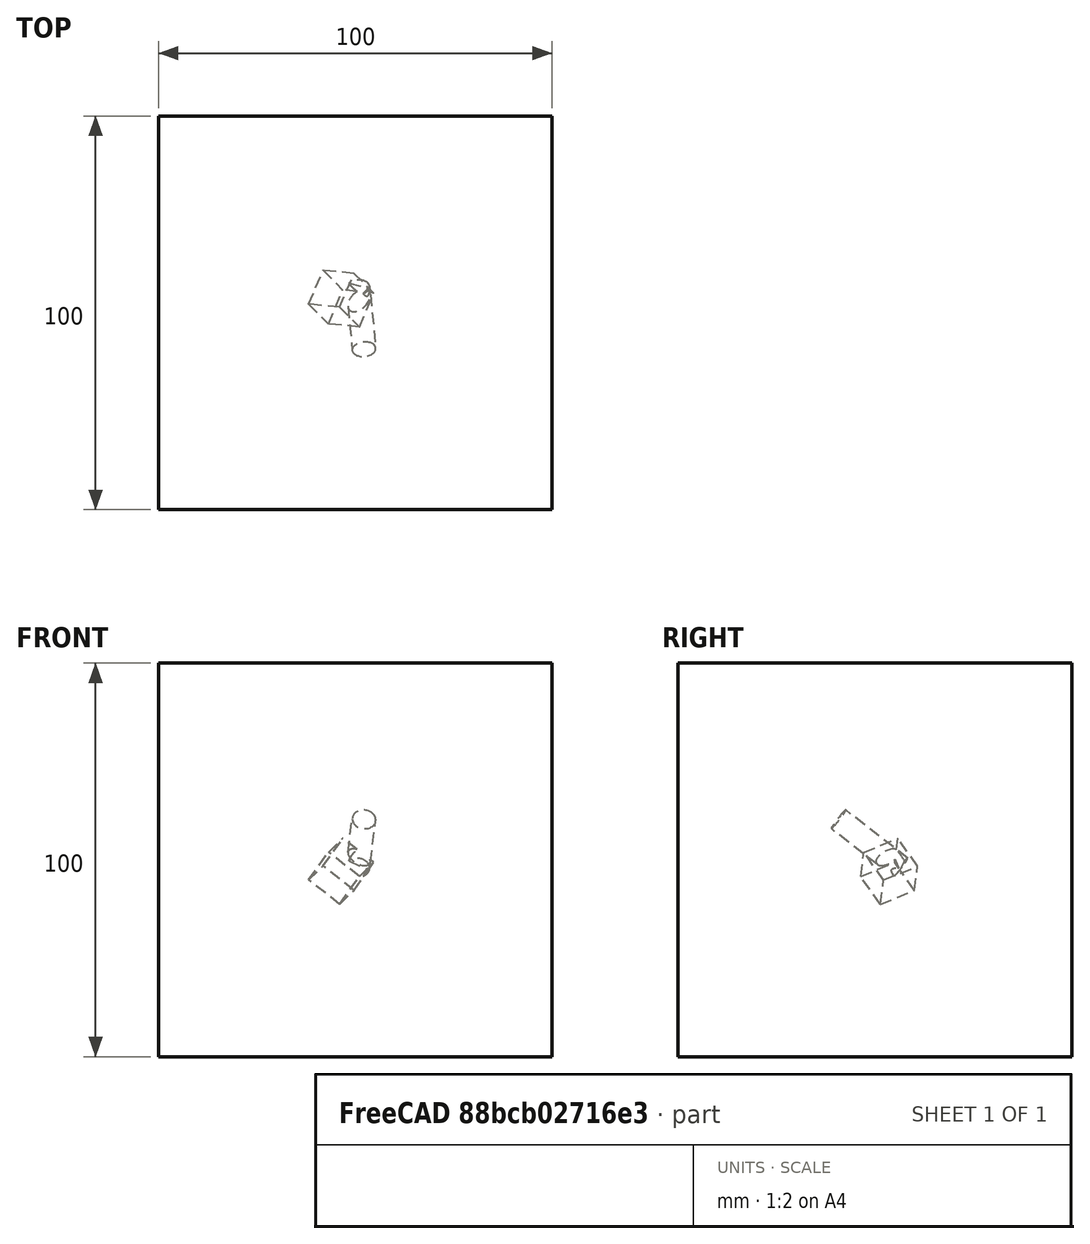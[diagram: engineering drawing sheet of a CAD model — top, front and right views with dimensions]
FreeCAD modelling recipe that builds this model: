
FCSTD DOCUMENT  (FreeCAD 0.21R33694 (Git))
Label: UnionTest
License: All rights reserved
objects: App::DocumentObjectGroupPython×1251, Part::FeaturePython×3, App::Part×2, Part::Fuse×1
note: 4 computed .brp shape members not serialized (recipe doc carries the construction recipe); baked Part::Feature solids carry a one-line shape summary decoded from their .brp

FEATURE [App::DocumentObjectGroupPython] HALFPI  # scripted group (container) (typed FeaturePython)
  name = HALFPI
  value = pi/2.
FEATURE [App::DocumentObjectGroupPython] PI  # scripted group (container) (typed FeaturePython)
  name = PI
  value = 1.*pi
FEATURE [App::DocumentObjectGroupPython] TWOPI  # scripted group (container) (typed FeaturePython)
  name = TWOPI
  value = 2.*pi
FEATURE [App::DocumentObjectGroupPython] Constants  # scripted group (container) (typed FeaturePython)
  Group = -> [HALFPI,PI,TWOPI]
FEATURE [App::DocumentObjectGroupPython] Variables  # scripted group (container) (typed FeaturePython)
FEATURE [App::DocumentObjectGroupPython] Quantities  # scripted group (container) (typed FeaturePython)
FEATURE [App::DocumentObjectGroupPython] Isotopes  # scripted group (container) (typed FeaturePython)
FEATURE [App::DocumentObjectGroupPython] Elements  # scripted group (container) (typed FeaturePython)
FEATURE [App::DocumentObjectGroupPython] Matrix  # scripted group (container) (typed FeaturePython)
FEATURE [App::DocumentObjectGroupPython] Surfaces  # scripted group (container) (typed FeaturePython)
FEATURE [App::DocumentObjectGroupPython] Opticals  # scripted group (container) (typed FeaturePython)
  Group = -> [Matrix,Surfaces]
FEATURE [App::DocumentObjectGroupPython] G4Isotopes  # scripted group (container) (typed FeaturePython)
FEATURE [App::DocumentObjectGroupPython] H_element  # scripted group (container) (typed FeaturePython)
  Z = 1
  atom_value = 1.008
  formula = H
  name = H_element
FEATURE [App::DocumentObjectGroupPython] He_element  # scripted group (container) (typed FeaturePython)
  Z = 2
  atom_value = 4.0026
  formula = He
  name = He_element
FEATURE [App::DocumentObjectGroupPython] Li_element  # scripted group (container) (typed FeaturePython)
  Z = 3
  atom_value = 6.94
  formula = Li
  name = Li_element
FEATURE [App::DocumentObjectGroupPython] Be_element  # scripted group (container) (typed FeaturePython)
  Z = 4
  atom_value = 9.01218
  formula = Be
  name = Be_element
FEATURE [App::DocumentObjectGroupPython] B_element  # scripted group (container) (typed FeaturePython)
  Z = 5
  atom_value = 10.81
  formula = B
  name = B_element
FEATURE [App::DocumentObjectGroupPython] C_element  # scripted group (container) (typed FeaturePython)
  Z = 6
  atom_value = 12.011
  formula = C
  name = C_element
FEATURE [App::DocumentObjectGroupPython] N_element  # scripted group (container) (typed FeaturePython)
  Z = 7
  atom_value = 14.007
  formula = N
  name = N_element
FEATURE [App::DocumentObjectGroupPython] O_element  # scripted group (container) (typed FeaturePython)
  Z = 8
  atom_value = 15.999
  formula = O
  name = O_element
FEATURE [App::DocumentObjectGroupPython] F_element  # scripted group (container) (typed FeaturePython)
  Z = 9
  atom_value = 18.9984
  formula = F
  name = F_element
FEATURE [App::DocumentObjectGroupPython] Ne_element  # scripted group (container) (typed FeaturePython)
  Z = 10
  atom_value = 20.1797
  formula = Ne
  name = Ne_element
FEATURE [App::DocumentObjectGroupPython] Na_element  # scripted group (container) (typed FeaturePython)
  Z = 11
  atom_value = 22.9898
  formula = Na
  name = Na_element
FEATURE [App::DocumentObjectGroupPython] Mg_element  # scripted group (container) (typed FeaturePython)
  Z = 12
  atom_value = 24.305
  formula = Mg
  name = Mg_element
FEATURE [App::DocumentObjectGroupPython] Al_element  # scripted group (container) (typed FeaturePython)
  Z = 13
  atom_value = 26.9815
  formula = Al
  name = Al_element
FEATURE [App::DocumentObjectGroupPython] Si_element  # scripted group (container) (typed FeaturePython)
  Z = 14
  atom_value = 28.085
  formula = Si
  name = Si_element
FEATURE [App::DocumentObjectGroupPython] P_element  # scripted group (container) (typed FeaturePython)
  Z = 15
  atom_value = 30.9738
  formula = P
  name = P_element
FEATURE [App::DocumentObjectGroupPython] S_element  # scripted group (container) (typed FeaturePython)
  Z = 16
  atom_value = 32.06
  formula = S
  name = S_element
FEATURE [App::DocumentObjectGroupPython] Cl_element  # scripted group (container) (typed FeaturePython)
  Z = 17
  atom_value = 35.45
  formula = Cl
  name = Cl_element
FEATURE [App::DocumentObjectGroupPython] Ar_element  # scripted group (container) (typed FeaturePython)
  Z = 18
  atom_value = 39.95
  formula = Ar
  name = Ar_element
FEATURE [App::DocumentObjectGroupPython] K_element  # scripted group (container) (typed FeaturePython)
  Z = 19
  atom_value = 39.0983
  formula = K
  name = K_element
FEATURE [App::DocumentObjectGroupPython] Ca_element  # scripted group (container) (typed FeaturePython)
  Z = 20
  atom_value = 40.078
  formula = Ca
  name = Ca_element
FEATURE [App::DocumentObjectGroupPython] Sc_element  # scripted group (container) (typed FeaturePython)
  Z = 21
  atom_value = 44.9559
  formula = Sc
  name = Sc_element
FEATURE [App::DocumentObjectGroupPython] Ti_element  # scripted group (container) (typed FeaturePython)
  Z = 22
  atom_value = 47.867
  formula = Ti
  name = Ti_element
FEATURE [App::DocumentObjectGroupPython] V_element  # scripted group (container) (typed FeaturePython)
  Z = 23
  atom_value = 50.9415
  formula = V
  name = V_element
FEATURE [App::DocumentObjectGroupPython] Cr_element  # scripted group (container) (typed FeaturePython)
  Z = 24
  atom_value = 51.9961
  formula = Cr
  name = Cr_element
FEATURE [App::DocumentObjectGroupPython] Mn_element  # scripted group (container) (typed FeaturePython)
  Z = 25
  atom_value = 54.938
  formula = Mn
  name = Mn_element
FEATURE [App::DocumentObjectGroupPython] Fe_element  # scripted group (container) (typed FeaturePython)
  Z = 26
  atom_value = 55.845
  formula = Fe
  name = Fe_element
FEATURE [App::DocumentObjectGroupPython] Co_element  # scripted group (container) (typed FeaturePython)
  Z = 27
  atom_value = 58.9332
  formula = Co
  name = Co_element
FEATURE [App::DocumentObjectGroupPython] Ni_element  # scripted group (container) (typed FeaturePython)
  Z = 28
  atom_value = 58.6934
  formula = Ni
  name = Ni_element
FEATURE [App::DocumentObjectGroupPython] Cu_element  # scripted group (container) (typed FeaturePython)
  Z = 29
  atom_value = 63.546
  formula = Cu
  name = Cu_element
FEATURE [App::DocumentObjectGroupPython] Zn_element  # scripted group (container) (typed FeaturePython)
  Z = 30
  atom_value = 65.38
  formula = Zn
  name = Zn_element
FEATURE [App::DocumentObjectGroupPython] Ga_element  # scripted group (container) (typed FeaturePython)
  Z = 31
  atom_value = 69.723
  formula = Ga
  name = Ga_element
FEATURE [App::DocumentObjectGroupPython] Ge_element  # scripted group (container) (typed FeaturePython)
  Z = 32
  atom_value = 72.63
  formula = Ge
  name = Ge_element
FEATURE [App::DocumentObjectGroupPython] As_element  # scripted group (container) (typed FeaturePython)
  Z = 33
  atom_value = 74.9216
  formula = As
  name = As_element
FEATURE [App::DocumentObjectGroupPython] Se_element  # scripted group (container) (typed FeaturePython)
  Z = 34
  atom_value = 78.971
  formula = Se
  name = Se_element
FEATURE [App::DocumentObjectGroupPython] Br_element  # scripted group (container) (typed FeaturePython)
  Z = 35
  atom_value = 79.904
  formula = Br
  name = Br_element
FEATURE [App::DocumentObjectGroupPython] Kr_element  # scripted group (container) (typed FeaturePython)
  Z = 36
  atom_value = 83.798
  formula = Kr
  name = Kr_element
FEATURE [App::DocumentObjectGroupPython] Rb_element  # scripted group (container) (typed FeaturePython)
  Z = 37
  atom_value = 85.4678
  formula = Rb
  name = Rb_element
FEATURE [App::DocumentObjectGroupPython] Sr_element  # scripted group (container) (typed FeaturePython)
  Z = 38
  atom_value = 87.62
  formula = Sr
  name = Sr_element
FEATURE [App::DocumentObjectGroupPython] Y_element  # scripted group (container) (typed FeaturePython)
  Z = 39
  atom_value = 88.9058
  formula = Y
  name = Y_element
FEATURE [App::DocumentObjectGroupPython] Zr_element  # scripted group (container) (typed FeaturePython)
  Z = 40
  atom_value = 91.224
  formula = Zr
  name = Zr_element
FEATURE [App::DocumentObjectGroupPython] Nb_element  # scripted group (container) (typed FeaturePython)
  Z = 41
  atom_value = 92.9064
  formula = Nb
  name = Nb_element
FEATURE [App::DocumentObjectGroupPython] Mo_element  # scripted group (container) (typed FeaturePython)
  Z = 42
  atom_value = 95.95
  formula = Mo
  name = Mo_element
FEATURE [App::DocumentObjectGroupPython] Tc_element  # scripted group (container) (typed FeaturePython)
  Z = 43
  atom_value = 97
  formula = Tc
  name = Tc_element
FEATURE [App::DocumentObjectGroupPython] Ru_element  # scripted group (container) (typed FeaturePython)
  Z = 44
  atom_value = 101.07
  formula = Ru
  name = Ru_element
FEATURE [App::DocumentObjectGroupPython] Rh_element  # scripted group (container) (typed FeaturePython)
  Z = 45
  atom_value = 102.905
  formula = Rh
  name = Rh_element
FEATURE [App::DocumentObjectGroupPython] Pd_element  # scripted group (container) (typed FeaturePython)
  Z = 46
  atom_value = 106.42
  formula = Pd
  name = Pd_element
FEATURE [App::DocumentObjectGroupPython] Ag_element  # scripted group (container) (typed FeaturePython)
  Z = 47
  atom_value = 107.868
  formula = Ag
  name = Ag_element
FEATURE [App::DocumentObjectGroupPython] Cd_element  # scripted group (container) (typed FeaturePython)
  Z = 48
  atom_value = 112.414
  formula = Cd
  name = Cd_element
FEATURE [App::DocumentObjectGroupPython] In_element  # scripted group (container) (typed FeaturePython)
  Z = 49
  atom_value = 114.818
  formula = In
  name = In_element
FEATURE [App::DocumentObjectGroupPython] Sn_element  # scripted group (container) (typed FeaturePython)
  Z = 50
  atom_value = 118.71
  formula = Sn
  name = Sn_element
FEATURE [App::DocumentObjectGroupPython] Sb_element  # scripted group (container) (typed FeaturePython)
  Z = 51
  atom_value = 121.76
  formula = Sb
  name = Sb_element
FEATURE [App::DocumentObjectGroupPython] Te_element  # scripted group (container) (typed FeaturePython)
  Z = 52
  atom_value = 127.6
  formula = Te
  name = Te_element
FEATURE [App::DocumentObjectGroupPython] I_element  # scripted group (container) (typed FeaturePython)
  Z = 53
  atom_value = 126.904
  formula = I
  name = I_element
FEATURE [App::DocumentObjectGroupPython] Xe_element  # scripted group (container) (typed FeaturePython)
  Z = 54
  atom_value = 131.293
  formula = Xe
  name = Xe_element
FEATURE [App::DocumentObjectGroupPython] Cs_element  # scripted group (container) (typed FeaturePython)
  Z = 55
  atom_value = 132.905
  formula = Cs
  name = Cs_element
FEATURE [App::DocumentObjectGroupPython] Ba_element  # scripted group (container) (typed FeaturePython)
  Z = 56
  atom_value = 137.327
  formula = Ba
  name = Ba_element
FEATURE [App::DocumentObjectGroupPython] La_element  # scripted group (container) (typed FeaturePython)
  Z = 57
  atom_value = 138.905
  formula = La
  name = La_element
FEATURE [App::DocumentObjectGroupPython] Ce_element  # scripted group (container) (typed FeaturePython)
  Z = 58
  atom_value = 140.116
  formula = Ce
  name = Ce_element
FEATURE [App::DocumentObjectGroupPython] Pr_element  # scripted group (container) (typed FeaturePython)
  Z = 59
  atom_value = 140.908
  formula = Pr
  name = Pr_element
FEATURE [App::DocumentObjectGroupPython] Nd_element  # scripted group (container) (typed FeaturePython)
  Z = 60
  atom_value = 144.242
  formula = Nd
  name = Nd_element
FEATURE [App::DocumentObjectGroupPython] Pm_element  # scripted group (container) (typed FeaturePython)
  Z = 61
  atom_value = 145
  formula = Pm
  name = Pm_element
FEATURE [App::DocumentObjectGroupPython] Sm_element  # scripted group (container) (typed FeaturePython)
  Z = 62
  atom_value = 150.36
  formula = Sm
  name = Sm_element
FEATURE [App::DocumentObjectGroupPython] Eu_element  # scripted group (container) (typed FeaturePython)
  Z = 63
  atom_value = 151.964
  formula = Eu
  name = Eu_element
FEATURE [App::DocumentObjectGroupPython] Gd_element  # scripted group (container) (typed FeaturePython)
  Z = 64
  atom_value = 157.25
  formula = Gd
  name = Gd_element
FEATURE [App::DocumentObjectGroupPython] Tb_element  # scripted group (container) (typed FeaturePython)
  Z = 65
  atom_value = 158.925
  formula = Tb
  name = Tb_element
FEATURE [App::DocumentObjectGroupPython] Dy_element  # scripted group (container) (typed FeaturePython)
  Z = 66
  atom_value = 162.5
  formula = Dy
  name = Dy_element
FEATURE [App::DocumentObjectGroupPython] Ho_element  # scripted group (container) (typed FeaturePython)
  Z = 67
  atom_value = 164.93
  formula = Ho
  name = Ho_element
FEATURE [App::DocumentObjectGroupPython] Er_element  # scripted group (container) (typed FeaturePython)
  Z = 68
  atom_value = 167.259
  formula = Er
  name = Er_element
FEATURE [App::DocumentObjectGroupPython] Tm_element  # scripted group (container) (typed FeaturePython)
  Z = 69
  atom_value = 168.934
  formula = Tm
  name = Tm_element
FEATURE [App::DocumentObjectGroupPython] Yb_element  # scripted group (container) (typed FeaturePython)
  Z = 70
  atom_value = 173.045
  formula = Yb
  name = Yb_element
FEATURE [App::DocumentObjectGroupPython] Lu_element  # scripted group (container) (typed FeaturePython)
  Z = 71
  atom_value = 174.967
  formula = Lu
  name = Lu_element
FEATURE [App::DocumentObjectGroupPython] Hf_element  # scripted group (container) (typed FeaturePython)
  Z = 72
  atom_value = 178.49
  formula = Hf
  name = Hf_element
FEATURE [App::DocumentObjectGroupPython] Ta_element  # scripted group (container) (typed FeaturePython)
  Z = 73
  atom_value = 180.948
  formula = Ta
  name = Ta_element
FEATURE [App::DocumentObjectGroupPython] W_element  # scripted group (container) (typed FeaturePython)
  Z = 74
  atom_value = 183.84
  formula = W
  name = W_element
FEATURE [App::DocumentObjectGroupPython] Re_element  # scripted group (container) (typed FeaturePython)
  Z = 75
  atom_value = 186.207
  formula = Re
  name = Re_element
FEATURE [App::DocumentObjectGroupPython] Os_element  # scripted group (container) (typed FeaturePython)
  Z = 76
  atom_value = 190.23
  formula = Os
  name = Os_element
FEATURE [App::DocumentObjectGroupPython] Ir_element  # scripted group (container) (typed FeaturePython)
  Z = 77
  atom_value = 192.217
  formula = Ir
  name = Ir_element
FEATURE [App::DocumentObjectGroupPython] Pt_element  # scripted group (container) (typed FeaturePython)
  Z = 78
  atom_value = 195.084
  formula = Pt
  name = Pt_element
FEATURE [App::DocumentObjectGroupPython] Au_element  # scripted group (container) (typed FeaturePython)
  Z = 79
  atom_value = 196.967
  formula = Au
  name = Au_element
FEATURE [App::DocumentObjectGroupPython] Hg_element  # scripted group (container) (typed FeaturePython)
  Z = 80
  atom_value = 200.592
  formula = Hg
  name = Hg_element
FEATURE [App::DocumentObjectGroupPython] Tl_element  # scripted group (container) (typed FeaturePython)
  Z = 81
  atom_value = 204.38
  formula = Tl
  name = Tl_element
FEATURE [App::DocumentObjectGroupPython] Pb_element  # scripted group (container) (typed FeaturePython)
  Z = 82
  atom_value = 207.2
  formula = Pb
  name = Pb_element
FEATURE [App::DocumentObjectGroupPython] Bi_element  # scripted group (container) (typed FeaturePython)
  Z = 83
  atom_value = 208.98
  formula = Bi
  name = Bi_element
FEATURE [App::DocumentObjectGroupPython] Po_element  # scripted group (container) (typed FeaturePython)
  Z = 84
  atom_value = 209
  formula = Po
  name = Po_element
FEATURE [App::DocumentObjectGroupPython] At_element  # scripted group (container) (typed FeaturePython)
  Z = 85
  atom_value = 210
  formula = At
  name = At_element
FEATURE [App::DocumentObjectGroupPython] Rn_element  # scripted group (container) (typed FeaturePython)
  Z = 86
  atom_value = 222
  formula = Rn
  name = Rn_element
FEATURE [App::DocumentObjectGroupPython] Fr_element  # scripted group (container) (typed FeaturePython)
  Z = 87
  atom_value = 223
  formula = Fr
  name = Fr_element
FEATURE [App::DocumentObjectGroupPython] Ra_element  # scripted group (container) (typed FeaturePython)
  Z = 88
  atom_value = 226
  formula = Ra
  name = Ra_element
FEATURE [App::DocumentObjectGroupPython] Ac_element  # scripted group (container) (typed FeaturePython)
  Z = 89
  atom_value = 227
  formula = Ac
  name = Ac_element
FEATURE [App::DocumentObjectGroupPython] Th_element  # scripted group (container) (typed FeaturePython)
  Z = 90
  atom_value = 232.038
  formula = Th
  name = Th_element
FEATURE [App::DocumentObjectGroupPython] Pa_element  # scripted group (container) (typed FeaturePython)
  Z = 91
  atom_value = 231.036
  formula = Pa
  name = Pa_element
FEATURE [App::DocumentObjectGroupPython] U_element  # scripted group (container) (typed FeaturePython)
  Z = 92
  atom_value = 238.029
  formula = U
  name = U_element
FEATURE [App::DocumentObjectGroupPython] Np_element  # scripted group (container) (typed FeaturePython)
  Z = 93
  atom_value = 237
  formula = Np
  name = Np_element
FEATURE [App::DocumentObjectGroupPython] Pu_element  # scripted group (container) (typed FeaturePython)
  Z = 94
  atom_value = 244
  formula = Pu
  name = Pu_element
FEATURE [App::DocumentObjectGroupPython] Am_element  # scripted group (container) (typed FeaturePython)
  Z = 95
  atom_value = 243
  formula = Am
  name = Am_element
FEATURE [App::DocumentObjectGroupPython] Cm_element  # scripted group (container) (typed FeaturePython)
  Z = 96
  atom_value = 247
  formula = Cm
  name = Cm_element
FEATURE [App::DocumentObjectGroupPython] Bk_element  # scripted group (container) (typed FeaturePython)
  Z = 97
  atom_value = 247
  formula = Bk
  name = Bk_element
FEATURE [App::DocumentObjectGroupPython] Cf_element  # scripted group (container) (typed FeaturePython)
  Z = 98
  atom_value = 251
  formula = Cf
  name = Cf_element
FEATURE [App::DocumentObjectGroupPython] G4Elements  # scripted group (container) (typed FeaturePython)
  Group = -> [H_element,He_element,Li_element,Be_element,B_element,C_element,N_element,O_element,F_element,Ne_element,Na_element,Mg_element,Al_element,Si_element,P_element,S_element,Cl_element,Ar_element,K_element,Ca_element,Sc_element,Ti_element,V_element,Cr_element,Mn_element,Fe_element,Co_element,Ni_element,Cu_element,Zn_element,Ga_element,Ge_element,As_element,Se_element,Br_element,Kr_element,Rb_element,+61 more]
FEATURE [App::DocumentObjectGroupPython] H_element001  label="H_element : 0.101"  # scripted group (container) (typed FeaturePython)
  n = 0.101327
FEATURE [App::DocumentObjectGroupPython] C_element001  label="C_element : 0.775"  # scripted group (container) (typed FeaturePython)
  n = 0.7755
FEATURE [App::DocumentObjectGroupPython] N_element001  label="N_element : 0.035"  # scripted group (container) (typed FeaturePython)
  n = 0.035057
FEATURE [App::DocumentObjectGroupPython] O_element001  label="O_element : 0.052"  # scripted group (container) (typed FeaturePython)
  n = 0.0523159
FEATURE [App::DocumentObjectGroupPython] F_element001  label="F_element : 0.017"  # scripted group (container) (typed FeaturePython)
  n = 0.017422
FEATURE [App::DocumentObjectGroupPython] Ca_element001  label="Ca_element : 0.018"  # scripted group (container) (typed FeaturePython)
  n = 0.018378
FEATURE [App::DocumentObjectGroupPython] G4_A_150_TISSUE  label="G4_A-150_TISSUE"  # scripted group (container) (typed FeaturePython)
  Dunit = g/cm3
  Dvalue = 1.127
  Group = -> [H_element001,C_element001,N_element001,O_element001,F_element001,Ca_element001]
  conduct = 2
  density = 1
  expand = 3
  formula = G4_A-150_TISSUE
  name = G4_A-150_TISSUE
  specific = 4
FEATURE [App::DocumentObjectGroupPython] C_element002  label="C_element : 3"  # scripted group (container) (typed FeaturePython)
  n = 3
  ref = C_element
FEATURE [App::DocumentObjectGroupPython] H_element002  label="H_element : 6"  # scripted group (container) (typed FeaturePython)
  n = 6
  ref = H_element
FEATURE [App::DocumentObjectGroupPython] O_element002  label="O_element : 1"  # scripted group (container) (typed FeaturePython)
  n = 1
  ref = O_element
FEATURE [App::DocumentObjectGroupPython] G4_ACETONE  # scripted group (container) (typed FeaturePython)
  Dunit = g/cm3
  Dvalue = 0.7899
  Group = -> [C_element002,H_element002,O_element002]
  conduct = 2
  density = 1
  expand = 3
  formula = G4_ACETONE
  name = G4_ACETONE
  specific = 4
FEATURE [App::DocumentObjectGroupPython] C_element003  label="C_element : 2"  # scripted group (container) (typed FeaturePython)
  n = 2
  ref = C_element
FEATURE [App::DocumentObjectGroupPython] H_element003  label="H_element : 2"  # scripted group (container) (typed FeaturePython)
  n = 2
  ref = H_element
FEATURE [App::DocumentObjectGroupPython] G4_ACETYLENE  # scripted group (container) (typed FeaturePython)
  Dunit = g/cm3
  Dvalue = 0.0010967
  Group = -> [C_element003,H_element003]
  conduct = 2
  density = 1
  expand = 3
  formula = G4_ACETYLENE
  name = G4_ACETYLENE
  specific = 4
FEATURE [App::DocumentObjectGroupPython] C_element004  label="C_element : 5"  # scripted group (container) (typed FeaturePython)
  n = 5
  ref = C_element
FEATURE [App::DocumentObjectGroupPython] H_element004  label="H_element : 5"  # scripted group (container) (typed FeaturePython)
  n = 5
  ref = H_element
FEATURE [App::DocumentObjectGroupPython] N_element002  label="N_element : 5"  # scripted group (container) (typed FeaturePython)
  n = 5
  ref = N_element
FEATURE [App::DocumentObjectGroupPython] G4_ADENINE  # scripted group (container) (typed FeaturePython)
  Dunit = g/cm3
  Dvalue = 1.6
  Group = -> [C_element004,H_element004,N_element002]
  conduct = 2
  density = 1
  expand = 3
  formula = G4_ADENINE
  name = G4_ADENINE
  specific = 4
FEATURE [App::DocumentObjectGroupPython] H_element005  label="H_element : 0.114"  # scripted group (container) (typed FeaturePython)
  n = 0.114
FEATURE [App::DocumentObjectGroupPython] C_element005  label="C_element : 0.598"  # scripted group (container) (typed FeaturePython)
  n = 0.598
FEATURE [App::DocumentObjectGroupPython] N_element003  label="N_element : 0.007"  # scripted group (container) (typed FeaturePython)
  n = 0.007
FEATURE [App::DocumentObjectGroupPython] O_element003  label="O_element : 0.278"  # scripted group (container) (typed FeaturePython)
  n = 0.278
FEATURE [App::DocumentObjectGroupPython] Na_element001  label="Na_element : 0.001"  # scripted group (container) (typed FeaturePython)
  n = 0.001
FEATURE [App::DocumentObjectGroupPython] S_element001  label="S_element : 0.001"  # scripted group (container) (typed FeaturePython)
  n = 0.001
FEATURE [App::DocumentObjectGroupPython] Cl_element001  label="Cl_element : 0.001"  # scripted group (container) (typed FeaturePython)
  n = 0.001
FEATURE [App::DocumentObjectGroupPython] G4_ADIPOSE_TISSUE_ICRP  # scripted group (container) (typed FeaturePython)
  Dunit = g/cm3
  Dvalue = 0.95
  Group = -> [H_element005,C_element005,N_element003,O_element003,Na_element001,S_element001,Cl_element001]
  conduct = 2
  density = 1
  expand = 3
  formula = G4_ADIPOSE_TISSUE_ICRP
  name = G4_ADIPOSE_TISSUE_ICRP
  specific = 4
FEATURE [App::DocumentObjectGroupPython] C_element006  label="C_element : 0.000"  # scripted group (container) (typed FeaturePython)
  n = 0.000124
FEATURE [App::DocumentObjectGroupPython] N_element004  label="N_element : 0.755"  # scripted group (container) (typed FeaturePython)
  n = 0.755268
FEATURE [App::DocumentObjectGroupPython] O_element004  label="O_element : 0.232"  # scripted group (container) (typed FeaturePython)
  n = 0.231781
FEATURE [App::DocumentObjectGroupPython] Ar_element001  label="Ar_element : 0.013"  # scripted group (container) (typed FeaturePython)
  n = 0.012827
FEATURE [App::DocumentObjectGroupPython] G4_AIR  # scripted group (container) (typed FeaturePython)
  Dunit = g/cm3
  Dvalue = 0.00120479
  Group = -> [C_element006,N_element004,O_element004,Ar_element001]
  conduct = 2
  density = 1
  expand = 3
  formula = G4_AIR
  name = G4_AIR
  specific = 4
FEATURE [App::DocumentObjectGroupPython] C_element007  label="C_element : 006"  # scripted group (container) (typed FeaturePython)
  n = 3
  ref = C_element
FEATURE [App::DocumentObjectGroupPython] H_element006  label="H_element : 7"  # scripted group (container) (typed FeaturePython)
  n = 7
  ref = H_element
FEATURE [App::DocumentObjectGroupPython] N_element005  label="N_element : 1"  # scripted group (container) (typed FeaturePython)
  n = 1
  ref = N_element
FEATURE [App::DocumentObjectGroupPython] O_element005  label="O_element : 2"  # scripted group (container) (typed FeaturePython)
  n = 2
  ref = O_element
FEATURE [App::DocumentObjectGroupPython] G4_ALANINE  # scripted group (container) (typed FeaturePython)
  Dunit = g/cm3
  Dvalue = 1.42
  Group = -> [C_element007,H_element006,N_element005,O_element005]
  conduct = 2
  density = 1
  expand = 3
  formula = G4_ALANINE
  name = G4_ALANINE
  specific = 4
FEATURE [App::DocumentObjectGroupPython] Al_element001  label="Al_element : 2"  # scripted group (container) (typed FeaturePython)
  n = 2
  ref = Al_element
FEATURE [App::DocumentObjectGroupPython] O_element006  label="O_element : 3"  # scripted group (container) (typed FeaturePython)
  n = 3
  ref = O_element
FEATURE [App::DocumentObjectGroupPython] G4_ALUMINUM_OXIDE  # scripted group (container) (typed FeaturePython)
  Dunit = g/cm3
  Dvalue = 3.97
  Group = -> [Al_element001,O_element006]
  conduct = 2
  density = 1
  expand = 3
  formula = G4_ALUMINUM_OXIDE
  name = G4_ALUMINUM_OXIDE
  specific = 4
FEATURE [App::DocumentObjectGroupPython] H_element007  label="H_element : 0.106"  # scripted group (container) (typed FeaturePython)
  n = 0.10593
FEATURE [App::DocumentObjectGroupPython] C_element008  label="C_element : 0.789"  # scripted group (container) (typed FeaturePython)
  n = 0.788974
FEATURE [App::DocumentObjectGroupPython] O_element007  label="O_element : 0.105"  # scripted group (container) (typed FeaturePython)
  n = 0.105096
FEATURE [App::DocumentObjectGroupPython] G4_AMBER  # scripted group (container) (typed FeaturePython)
  Dunit = g/cm3
  Dvalue = 1.1
  Group = -> [H_element007,C_element008,O_element007]
  conduct = 2
  density = 1
  expand = 3
  formula = G4_AMBER
  name = G4_AMBER
  specific = 4
FEATURE [App::DocumentObjectGroupPython] N_element006  label="N_element : 006"  # scripted group (container) (typed FeaturePython)
  n = 1
  ref = N_element
FEATURE [App::DocumentObjectGroupPython] H_element008  label="H_element : 3"  # scripted group (container) (typed FeaturePython)
  n = 3
  ref = H_element
FEATURE [App::DocumentObjectGroupPython] G4_AMMONIA  # scripted group (container) (typed FeaturePython)
  Dunit = g/cm3
  Dvalue = 0.000826019
  Group = -> [N_element006,H_element008]
  conduct = 2
  density = 1
  expand = 3
  formula = G4_AMMONIA
  name = G4_AMMONIA
  specific = 4
FEATURE [App::DocumentObjectGroupPython] C_element009  label="C_element : 6"  # scripted group (container) (typed FeaturePython)
  n = 6
  ref = C_element
FEATURE [App::DocumentObjectGroupPython] H_element009  label="H_element : 008"  # scripted group (container) (typed FeaturePython)
  n = 7
  ref = H_element
FEATURE [App::DocumentObjectGroupPython] N_element007  label="N_element : 007"  # scripted group (container) (typed FeaturePython)
  n = 1
  ref = N_element
FEATURE [App::DocumentObjectGroupPython] G4_ANILINE  # scripted group (container) (typed FeaturePython)
  Dunit = g/cm3
  Dvalue = 1.0235
  Group = -> [C_element009,H_element009,N_element007]
  conduct = 2
  density = 1
  expand = 3
  formula = G4_ANILINE
  name = G4_ANILINE
  specific = 4
FEATURE [App::DocumentObjectGroupPython] C_element010  label="C_element : 14"  # scripted group (container) (typed FeaturePython)
  n = 14
  ref = C_element
FEATURE [App::DocumentObjectGroupPython] H_element010  label="H_element : 10"  # scripted group (container) (typed FeaturePython)
  n = 10
  ref = H_element
FEATURE [App::DocumentObjectGroupPython] G4_ANTHRACENE  # scripted group (container) (typed FeaturePython)
  Dunit = g/cm3
  Dvalue = 1.283
  Group = -> [C_element010,H_element010]
  conduct = 2
  density = 1
  expand = 3
  formula = G4_ANTHRACENE
  name = G4_ANTHRACENE
  specific = 4
FEATURE [App::DocumentObjectGroupPython] H_element011  label="H_element : 0.065"  # scripted group (container) (typed FeaturePython)
  n = 0.0654709
FEATURE [App::DocumentObjectGroupPython] C_element011  label="C_element : 0.537"  # scripted group (container) (typed FeaturePython)
  n = 0.536944
FEATURE [App::DocumentObjectGroupPython] N_element008  label="N_element : 0.021"  # scripted group (container) (typed FeaturePython)
  n = 0.0215
FEATURE [App::DocumentObjectGroupPython] O_element008  label="O_element : 0.032"  # scripted group (container) (typed FeaturePython)
  n = 0.032085
FEATURE [App::DocumentObjectGroupPython] F_element002  label="F_element : 0.167"  # scripted group (container) (typed FeaturePython)
  n = 0.167411
FEATURE [App::DocumentObjectGroupPython] Ca_element002  label="Ca_element : 0.177"  # scripted group (container) (typed FeaturePython)
  n = 0.176589
FEATURE [App::DocumentObjectGroupPython] G4_B_100_BONE  label="G4_B-100_BONE"  # scripted group (container) (typed FeaturePython)
  Dunit = g/cm3
  Dvalue = 1.45
  Group = -> [H_element011,C_element011,N_element008,O_element008,F_element002,Ca_element002]
  conduct = 2
  density = 1
  expand = 3
  formula = G4_B-100_BONE
  name = G4_B-100_BONE
  specific = 4
FEATURE [App::DocumentObjectGroupPython] H_element012  label="H_element : 0.057"  # scripted group (container) (typed FeaturePython)
  n = 0.057441
FEATURE [App::DocumentObjectGroupPython] C_element012  label="C_element : 0.790"  # scripted group (container) (typed FeaturePython)
  n = 0.774591
FEATURE [App::DocumentObjectGroupPython] O_element009  label="O_element : 0.168"  # scripted group (container) (typed FeaturePython)
  n = 0.167968
FEATURE [App::DocumentObjectGroupPython] G4_BAKELITE  # scripted group (container) (typed FeaturePython)
  Dunit = g/cm3
  Dvalue = 1.25
  Group = -> [H_element012,C_element012,O_element009]
  conduct = 2
  density = 1
  expand = 3
  formula = G4_BAKELITE
  name = G4_BAKELITE
  specific = 4
FEATURE [App::DocumentObjectGroupPython] Ba_element001  label="Ba_element : 1"  # scripted group (container) (typed FeaturePython)
  n = 1
  ref = Ba_element
FEATURE [App::DocumentObjectGroupPython] F_element003  label="F_element : 2"  # scripted group (container) (typed FeaturePython)
  n = 2
  ref = F_element
FEATURE [App::DocumentObjectGroupPython] G4_BARIUM_FLUORIDE  # scripted group (container) (typed FeaturePython)
  Dunit = g/cm3
  Dvalue = 4.89
  Group = -> [Ba_element001,F_element003]
  conduct = 2
  density = 1
  expand = 3
  formula = G4_BARIUM_FLUORIDE
  name = G4_BARIUM_FLUORIDE
  specific = 4
FEATURE [App::DocumentObjectGroupPython] Ba_element002  label="Ba_element : 002"  # scripted group (container) (typed FeaturePython)
  n = 1
  ref = Ba_element
FEATURE [App::DocumentObjectGroupPython] S_element002  label="S_element : 1"  # scripted group (container) (typed FeaturePython)
  n = 1
  ref = S_element
FEATURE [App::DocumentObjectGroupPython] O_element010  label="O_element : 4"  # scripted group (container) (typed FeaturePython)
  n = 4
  ref = O_element
FEATURE [App::DocumentObjectGroupPython] G4_BARIUM_SULFATE  # scripted group (container) (typed FeaturePython)
  Dunit = g/cm3
  Dvalue = 4.5
  Group = -> [Ba_element002,S_element002,O_element010]
  conduct = 2
  density = 1
  expand = 3
  formula = G4_BARIUM_SULFATE
  name = G4_BARIUM_SULFATE
  specific = 4
FEATURE [App::DocumentObjectGroupPython] C_element013  label="C_element : 007"  # scripted group (container) (typed FeaturePython)
  n = 6
  ref = C_element
FEATURE [App::DocumentObjectGroupPython] H_element013  label="H_element : 009"  # scripted group (container) (typed FeaturePython)
  n = 6
  ref = H_element
FEATURE [App::DocumentObjectGroupPython] G4_BENZENE  # scripted group (container) (typed FeaturePython)
  Dunit = g/cm3
  Dvalue = 0.87865
  Group = -> [C_element013,H_element013]
  conduct = 2
  density = 1
  expand = 3
  formula = G4_BENZENE
  name = G4_BENZENE
  specific = 4
FEATURE [App::DocumentObjectGroupPython] Be_element001  label="Be_element : 1"  # scripted group (container) (typed FeaturePython)
  n = 1
  ref = Be_element
FEATURE [App::DocumentObjectGroupPython] O_element011  label="O_element : 005"  # scripted group (container) (typed FeaturePython)
  n = 1
  ref = O_element
FEATURE [App::DocumentObjectGroupPython] G4_BERYLLIUM_OXIDE  # scripted group (container) (typed FeaturePython)
  Dunit = g/cm3
  Dvalue = 3.01
  Group = -> [Be_element001,O_element011]
  conduct = 2
  density = 1
  expand = 3
  formula = G4_BERYLLIUM_OXIDE
  name = G4_BERYLLIUM_OXIDE
  specific = 4
FEATURE [App::DocumentObjectGroupPython] Bi_element001  label="Bi_element : 4"  # scripted group (container) (typed FeaturePython)
  n = 4
  ref = Bi_element
FEATURE [App::DocumentObjectGroupPython] Ge_element001  label="Ge_element : 3"  # scripted group (container) (typed FeaturePython)
  n = 3
  ref = Ge_element
FEATURE [App::DocumentObjectGroupPython] O_element012  label="O_element : 12"  # scripted group (container) (typed FeaturePython)
  n = 12
  ref = O_element
FEATURE [App::DocumentObjectGroupPython] G4_BGO  # scripted group (container) (typed FeaturePython)
  Dunit = g/cm3
  Dvalue = 7.13
  Group = -> [Bi_element001,Ge_element001,O_element012]
  conduct = 2
  density = 1
  expand = 3
  formula = G4_BGO
  name = G4_BGO
  specific = 4
FEATURE [App::DocumentObjectGroupPython] H_element014  label="H_element : 0.102"  # scripted group (container) (typed FeaturePython)
  n = 0.102
FEATURE [App::DocumentObjectGroupPython] C_element014  label="C_element : 0.110"  # scripted group (container) (typed FeaturePython)
  n = 0.11
FEATURE [App::DocumentObjectGroupPython] N_element009  label="N_element : 0.033"  # scripted group (container) (typed FeaturePython)
  n = 0.033
FEATURE [App::DocumentObjectGroupPython] O_element013  label="O_element : 0.745"  # scripted group (container) (typed FeaturePython)
  n = 0.745
FEATURE [App::DocumentObjectGroupPython] Na_element002  label="Na_element : 0.002"  # scripted group (container) (typed FeaturePython)
  n = 0.001
FEATURE [App::DocumentObjectGroupPython] P_element001  label="P_element : 0.001"  # scripted group (container) (typed FeaturePython)
  n = 0.001
FEATURE [App::DocumentObjectGroupPython] S_element003  label="S_element : 0.002"  # scripted group (container) (typed FeaturePython)
  n = 0.002
FEATURE [App::DocumentObjectGroupPython] Cl_element002  label="Cl_element : 0.003"  # scripted group (container) (typed FeaturePython)
  n = 0.003
FEATURE [App::DocumentObjectGroupPython] K_element001  label="K_element : 0.002"  # scripted group (container) (typed FeaturePython)
  n = 0.002
FEATURE [App::DocumentObjectGroupPython] Fe_element001  label="Fe_element : 0.001"  # scripted group (container) (typed FeaturePython)
  n = 0.001
FEATURE [App::DocumentObjectGroupPython] G4_BLOOD_ICRP  # scripted group (container) (typed FeaturePython)
  Dunit = g/cm3
  Dvalue = 1.06
  Group = -> [H_element014,C_element014,N_element009,O_element013,Na_element002,P_element001,S_element003,Cl_element002,K_element001,Fe_element001]
  conduct = 2
  density = 1
  expand = 3
  formula = G4_BLOOD_ICRP
  name = G4_BLOOD_ICRP
  specific = 4
FEATURE [App::DocumentObjectGroupPython] H_element015  label="H_element : 0.064"  # scripted group (container) (typed FeaturePython)
  n = 0.064
FEATURE [App::DocumentObjectGroupPython] C_element015  label="C_element : 0.278"  # scripted group (container) (typed FeaturePython)
  n = 0.278
FEATURE [App::DocumentObjectGroupPython] N_element010  label="N_element : 0.027"  # scripted group (container) (typed FeaturePython)
  n = 0.027
FEATURE [App::DocumentObjectGroupPython] O_element014  label="O_element : 0.410"  # scripted group (container) (typed FeaturePython)
  n = 0.41
FEATURE [App::DocumentObjectGroupPython] Mg_element001  label="Mg_element : 0.002"  # scripted group (container) (typed FeaturePython)
  n = 0.002
FEATURE [App::DocumentObjectGroupPython] P_element002  label="P_element : 0.070"  # scripted group (container) (typed FeaturePython)
  n = 0.07
FEATURE [App::DocumentObjectGroupPython] S_element004  label="S_element : 0.003"  # scripted group (container) (typed FeaturePython)
  n = 0.002
FEATURE [App::DocumentObjectGroupPython] Ca_element003  label="Ca_element : 0.147"  # scripted group (container) (typed FeaturePython)
  n = 0.147
FEATURE [App::DocumentObjectGroupPython] G4_BONE_COMPACT_ICRU  # scripted group (container) (typed FeaturePython)
  Dunit = g/cm3
  Dvalue = 1.85
  Group = -> [H_element015,C_element015,N_element010,O_element014,Mg_element001,P_element002,S_element004,Ca_element003]
  conduct = 2
  density = 1
  expand = 3
  formula = G4_BONE_COMPACT_ICRU
  name = G4_BONE_COMPACT_ICRU
  specific = 4
FEATURE [App::DocumentObjectGroupPython] H_element016  label="H_element : 0.034"  # scripted group (container) (typed FeaturePython)
  n = 0.034
FEATURE [App::DocumentObjectGroupPython] C_element016  label="C_element : 0.155"  # scripted group (container) (typed FeaturePython)
  n = 0.155
FEATURE [App::DocumentObjectGroupPython] N_element011  label="N_element : 0.042"  # scripted group (container) (typed FeaturePython)
  n = 0.042
FEATURE [App::DocumentObjectGroupPython] O_element015  label="O_element : 0.435"  # scripted group (container) (typed FeaturePython)
  n = 0.435
FEATURE [App::DocumentObjectGroupPython] Na_element003  label="Na_element : 0.003"  # scripted group (container) (typed FeaturePython)
  n = 0.001
FEATURE [App::DocumentObjectGroupPython] Mg_element002  label="Mg_element : 0.003"  # scripted group (container) (typed FeaturePython)
  n = 0.002
FEATURE [App::DocumentObjectGroupPython] P_element003  label="P_element : 0.103"  # scripted group (container) (typed FeaturePython)
  n = 0.103
FEATURE [App::DocumentObjectGroupPython] S_element005  label="S_element : 0.004"  # scripted group (container) (typed FeaturePython)
  n = 0.003
FEATURE [App::DocumentObjectGroupPython] Ca_element004  label="Ca_element : 0.225"  # scripted group (container) (typed FeaturePython)
  n = 0.225
FEATURE [App::DocumentObjectGroupPython] G4_BONE_CORTICAL_ICRP  # scripted group (container) (typed FeaturePython)
  Dunit = g/cm3
  Dvalue = 1.92
  Group = -> [H_element016,C_element016,N_element011,O_element015,Na_element003,Mg_element002,P_element003,S_element005,Ca_element004]
  conduct = 2
  density = 1
  expand = 3
  formula = G4_BONE_CORTICAL_ICRP
  name = G4_BONE_CORTICAL_ICRP
  specific = 4
FEATURE [App::DocumentObjectGroupPython] B_element001  label="B_element : 4"  # scripted group (container) (typed FeaturePython)
  n = 4
  ref = B_element
FEATURE [App::DocumentObjectGroupPython] C_element017  label="C_element : 1"  # scripted group (container) (typed FeaturePython)
  n = 1
  ref = C_element
FEATURE [App::DocumentObjectGroupPython] G4_BORON_CARBIDE  # scripted group (container) (typed FeaturePython)
  Dunit = g/cm3
  Dvalue = 2.52
  Group = -> [B_element001,C_element017]
  conduct = 2
  density = 1
  expand = 3
  formula = G4_BORON_CARBIDE
  name = G4_BORON_CARBIDE
  specific = 4
FEATURE [App::DocumentObjectGroupPython] B_element002  label="B_element : 2"  # scripted group (container) (typed FeaturePython)
  n = 2
  ref = B_element
FEATURE [App::DocumentObjectGroupPython] O_element016  label="O_element : 006"  # scripted group (container) (typed FeaturePython)
  n = 3
  ref = O_element
FEATURE [App::DocumentObjectGroupPython] G4_BORON_OXIDE  # scripted group (container) (typed FeaturePython)
  Dunit = g/cm3
  Dvalue = 1.812
  Group = -> [B_element002,O_element016]
  conduct = 2
  density = 1
  expand = 3
  formula = G4_BORON_OXIDE
  name = G4_BORON_OXIDE
  specific = 4
FEATURE [App::DocumentObjectGroupPython] H_element017  label="H_element : 0.107"  # scripted group (container) (typed FeaturePython)
  n = 0.107
FEATURE [App::DocumentObjectGroupPython] C_element018  label="C_element : 0.145"  # scripted group (container) (typed FeaturePython)
  n = 0.145
FEATURE [App::DocumentObjectGroupPython] N_element012  label="N_element : 0.022"  # scripted group (container) (typed FeaturePython)
  n = 0.022
FEATURE [App::DocumentObjectGroupPython] O_element017  label="O_element : 0.712"  # scripted group (container) (typed FeaturePython)
  n = 0.712
FEATURE [App::DocumentObjectGroupPython] Na_element004  label="Na_element : 0.004"  # scripted group (container) (typed FeaturePython)
  n = 0.002
FEATURE [App::DocumentObjectGroupPython] P_element004  label="P_element : 0.004"  # scripted group (container) (typed FeaturePython)
  n = 0.004
FEATURE [App::DocumentObjectGroupPython] S_element006  label="S_element : 0.005"  # scripted group (container) (typed FeaturePython)
  n = 0.002
FEATURE [App::DocumentObjectGroupPython] Cl_element003  label="Cl_element : 0.004"  # scripted group (container) (typed FeaturePython)
  n = 0.003
FEATURE [App::DocumentObjectGroupPython] K_element002  label="K_element : 0.003"  # scripted group (container) (typed FeaturePython)
  n = 0.003
FEATURE [App::DocumentObjectGroupPython] G4_BRAIN_ICRP  # scripted group (container) (typed FeaturePython)
  Dunit = g/cm3
  Dvalue = 1.04
  Group = -> [H_element017,C_element018,N_element012,O_element017,Na_element004,P_element004,S_element006,Cl_element003,K_element002]
  conduct = 2
  density = 1
  expand = 3
  formula = G4_BRAIN_ICRP
  name = G4_BRAIN_ICRP
  specific = 4
FEATURE [App::DocumentObjectGroupPython] C_element019  label="C_element : 4"  # scripted group (container) (typed FeaturePython)
  n = 4
  ref = C_element
FEATURE [App::DocumentObjectGroupPython] H_element018  label="H_element : 010"  # scripted group (container) (typed FeaturePython)
  n = 10
  ref = H_element
FEATURE [App::DocumentObjectGroupPython] G4_BUTANE  # scripted group (container) (typed FeaturePython)
  Dunit = g/cm3
  Dvalue = 0.00249343
  Group = -> [C_element019,H_element018]
  conduct = 2
  density = 1
  expand = 3
  formula = G4_BUTANE
  name = G4_BUTANE
  specific = 4
FEATURE [App::DocumentObjectGroupPython] C_element020  label="C_element : 008"  # scripted group (container) (typed FeaturePython)
  n = 4
  ref = C_element
FEATURE [App::DocumentObjectGroupPython] H_element019  label="H_element : 011"  # scripted group (container) (typed FeaturePython)
  n = 10
  ref = H_element
FEATURE [App::DocumentObjectGroupPython] O_element018  label="O_element : 007"  # scripted group (container) (typed FeaturePython)
  n = 1
  ref = O_element
FEATURE [App::DocumentObjectGroupPython] G4_N_BUTYL_ALCOHOL  label="G4_N-BUTYL_ALCOHOL"  # scripted group (container) (typed FeaturePython)
  Dunit = g/cm3
  Dvalue = 0.8098
  Group = -> [C_element020,H_element019,O_element018]
  conduct = 2
  density = 1
  expand = 3
  formula = G4_N-BUTYL_ALCOHOL
  name = G4_N-BUTYL_ALCOHOL
  specific = 4
FEATURE [App::DocumentObjectGroupPython] H_element020  label="H_element : 0.025"  # scripted group (container) (typed FeaturePython)
  n = 0.02468
FEATURE [App::DocumentObjectGroupPython] C_element021  label="C_element : 0.502"  # scripted group (container) (typed FeaturePython)
  n = 0.501611
FEATURE [App::DocumentObjectGroupPython] O_element019  label="O_element : 0.005"  # scripted group (container) (typed FeaturePython)
  n = 0.004527
FEATURE [App::DocumentObjectGroupPython] F_element004  label="F_element : 0.465"  # scripted group (container) (typed FeaturePython)
  n = 0.465209
FEATURE [App::DocumentObjectGroupPython] Si_element001  label="Si_element : 0.004"  # scripted group (container) (typed FeaturePython)
  n = 0.003973
FEATURE [App::DocumentObjectGroupPython] G4_C_552  label="G4_C-552"  # scripted group (container) (typed FeaturePython)
  Dunit = g/cm3
  Dvalue = 1.76
  Group = -> [H_element020,C_element021,O_element019,F_element004,Si_element001]
  conduct = 2
  density = 1
  expand = 3
  formula = G4_C-552
  name = G4_C-552
  specific = 4
FEATURE [App::DocumentObjectGroupPython] Cd_element001  label="Cd_element : 1"  # scripted group (container) (typed FeaturePython)
  n = 1
  ref = Cd_element
FEATURE [App::DocumentObjectGroupPython] Te_element001  label="Te_element : 1"  # scripted group (container) (typed FeaturePython)
  n = 1
  ref = Te_element
FEATURE [App::DocumentObjectGroupPython] G4_CADMIUM_TELLURIDE  # scripted group (container) (typed FeaturePython)
  Dunit = g/cm3
  Dvalue = 6.2
  Group = -> [Cd_element001,Te_element001]
  conduct = 2
  density = 1
  expand = 3
  formula = G4_CADMIUM_TELLURIDE
  name = G4_CADMIUM_TELLURIDE
  specific = 4
FEATURE [App::DocumentObjectGroupPython] Cd_element002  label="Cd_element : 002"  # scripted group (container) (typed FeaturePython)
  n = 1
  ref = Cd_element
FEATURE [App::DocumentObjectGroupPython] W_element001  label="W_element : 1"  # scripted group (container) (typed FeaturePython)
  n = 1
  ref = W_element
FEATURE [App::DocumentObjectGroupPython] O_element020  label="O_element : 008"  # scripted group (container) (typed FeaturePython)
  n = 4
  ref = O_element
FEATURE [App::DocumentObjectGroupPython] G4_CADMIUM_TUNGSTATE  # scripted group (container) (typed FeaturePython)
  Dunit = g/cm3
  Dvalue = 7.9
  Group = -> [Cd_element002,W_element001,O_element020]
  conduct = 2
  density = 1
  expand = 3
  formula = G4_CADMIUM_TUNGSTATE
  name = G4_CADMIUM_TUNGSTATE
  specific = 4
FEATURE [App::DocumentObjectGroupPython] Ca_element005  label="Ca_element : 1"  # scripted group (container) (typed FeaturePython)
  n = 1
  ref = Ca_element
FEATURE [App::DocumentObjectGroupPython] C_element022  label="C_element : 009"  # scripted group (container) (typed FeaturePython)
  n = 1
  ref = C_element
FEATURE [App::DocumentObjectGroupPython] O_element021  label="O_element : 009"  # scripted group (container) (typed FeaturePython)
  n = 3
  ref = O_element
FEATURE [App::DocumentObjectGroupPython] G4_CALCIUM_CARBONATE  # scripted group (container) (typed FeaturePython)
  Dunit = g/cm3
  Dvalue = 2.8
  Group = -> [Ca_element005,C_element022,O_element021]
  conduct = 2
  density = 1
  expand = 3
  formula = G4_CALCIUM_CARBONATE
  name = G4_CALCIUM_CARBONATE
  specific = 4
FEATURE [App::DocumentObjectGroupPython] Ca_element006  label="Ca_element : 002"  # scripted group (container) (typed FeaturePython)
  n = 1
  ref = Ca_element
FEATURE [App::DocumentObjectGroupPython] F_element005  label="F_element : 003"  # scripted group (container) (typed FeaturePython)
  n = 2
  ref = F_element
FEATURE [App::DocumentObjectGroupPython] G4_CALCIUM_FLUORIDE  # scripted group (container) (typed FeaturePython)
  Dunit = g/cm3
  Dvalue = 3.18
  Group = -> [Ca_element006,F_element005]
  conduct = 2
  density = 1
  expand = 3
  formula = G4_CALCIUM_FLUORIDE
  name = G4_CALCIUM_FLUORIDE
  specific = 4
FEATURE [App::DocumentObjectGroupPython] Ca_element007  label="Ca_element : 003"  # scripted group (container) (typed FeaturePython)
  n = 1
  ref = Ca_element
FEATURE [App::DocumentObjectGroupPython] O_element022  label="O_element : 010"  # scripted group (container) (typed FeaturePython)
  n = 1
  ref = O_element
FEATURE [App::DocumentObjectGroupPython] G4_CALCIUM_OXIDE  # scripted group (container) (typed FeaturePython)
  Dunit = g/cm3
  Dvalue = 3.3
  Group = -> [Ca_element007,O_element022]
  conduct = 2
  density = 1
  expand = 3
  formula = G4_CALCIUM_OXIDE
  name = G4_CALCIUM_OXIDE
  specific = 4
FEATURE [App::DocumentObjectGroupPython] Ca_element008  label="Ca_element : 004"  # scripted group (container) (typed FeaturePython)
  n = 1
  ref = Ca_element
FEATURE [App::DocumentObjectGroupPython] S_element007  label="S_element : 002"  # scripted group (container) (typed FeaturePython)
  n = 1
  ref = S_element
FEATURE [App::DocumentObjectGroupPython] O_element023  label="O_element : 011"  # scripted group (container) (typed FeaturePython)
  n = 4
  ref = O_element
FEATURE [App::DocumentObjectGroupPython] G4_CALCIUM_SULFATE  # scripted group (container) (typed FeaturePython)
  Dunit = g/cm3
  Dvalue = 2.96
  Group = -> [Ca_element008,S_element007,O_element023]
  conduct = 2
  density = 1
  expand = 3
  formula = G4_CALCIUM_SULFATE
  name = G4_CALCIUM_SULFATE
  specific = 4
FEATURE [App::DocumentObjectGroupPython] Ca_element009  label="Ca_element : 005"  # scripted group (container) (typed FeaturePython)
  n = 1
  ref = Ca_element
FEATURE [App::DocumentObjectGroupPython] W_element002  label="W_element : 002"  # scripted group (container) (typed FeaturePython)
  n = 1
  ref = W_element
FEATURE [App::DocumentObjectGroupPython] O_element024  label="O_element : 012"  # scripted group (container) (typed FeaturePython)
  n = 4
  ref = O_element
FEATURE [App::DocumentObjectGroupPython] G4_CALCIUM_TUNGSTATE  # scripted group (container) (typed FeaturePython)
  Dunit = g/cm3
  Dvalue = 6.062
  Group = -> [Ca_element009,W_element002,O_element024]
  conduct = 2
  density = 1
  expand = 3
  formula = G4_CALCIUM_TUNGSTATE
  name = G4_CALCIUM_TUNGSTATE
  specific = 4
FEATURE [App::DocumentObjectGroupPython] C_element023  label="C_element : 010"  # scripted group (container) (typed FeaturePython)
  n = 1
  ref = C_element
FEATURE [App::DocumentObjectGroupPython] O_element025  label="O_element : 013"  # scripted group (container) (typed FeaturePython)
  n = 2
  ref = O_element
FEATURE [App::DocumentObjectGroupPython] G4_CARBON_DIOXIDE  # scripted group (container) (typed FeaturePython)
  Dunit = g/cm3
  Dvalue = 0.00184212
  Group = -> [C_element023,O_element025]
  conduct = 2
  density = 1
  expand = 3
  formula = G4_CARBON_DIOXIDE
  name = G4_CARBON_DIOXIDE
  specific = 4
FEATURE [App::DocumentObjectGroupPython] C_element024  label="C_element : 011"  # scripted group (container) (typed FeaturePython)
  n = 1
  ref = C_element
FEATURE [App::DocumentObjectGroupPython] Cl_element004  label="Cl_element : 4"  # scripted group (container) (typed FeaturePython)
  n = 4
  ref = Cl_element
FEATURE [App::DocumentObjectGroupPython] G4_CARBON_TETRACHLORIDE  # scripted group (container) (typed FeaturePython)
  Dunit = g/cm3
  Dvalue = 1.594
  Group = -> [C_element024,Cl_element004]
  conduct = 2
  density = 1
  expand = 3
  formula = G4_CARBON_TETRACHLORIDE
  name = G4_CARBON_TETRACHLORIDE
  specific = 4
FEATURE [App::DocumentObjectGroupPython] C_element025  label="C_element : 012"  # scripted group (container) (typed FeaturePython)
  n = 6
  ref = C_element
FEATURE [App::DocumentObjectGroupPython] H_element021  label="H_element : 012"  # scripted group (container) (typed FeaturePython)
  n = 10
  ref = H_element
FEATURE [App::DocumentObjectGroupPython] O_element026  label="O_element : 5"  # scripted group (container) (typed FeaturePython)
  n = 5
  ref = O_element
FEATURE [App::DocumentObjectGroupPython] G4_CELLULOSE_CELLOPHANE  # scripted group (container) (typed FeaturePython)
  Dunit = g/cm3
  Dvalue = 1.42
  Group = -> [C_element025,H_element021,O_element026]
  conduct = 2
  density = 1
  expand = 3
  formula = G4_CELLULOSE_CELLOPHANE
  name = G4_CELLULOSE_CELLOPHANE
  specific = 4
FEATURE [App::DocumentObjectGroupPython] H_element022  label="H_element : 0.067"  # scripted group (container) (typed FeaturePython)
  n = 0.067125
FEATURE [App::DocumentObjectGroupPython] C_element026  label="C_element : 0.545"  # scripted group (container) (typed FeaturePython)
  n = 0.545403
FEATURE [App::DocumentObjectGroupPython] O_element027  label="O_element : 0.387"  # scripted group (container) (typed FeaturePython)
  n = 0.387472
FEATURE [App::DocumentObjectGroupPython] G4_CELLULOSE_BUTYRATE  # scripted group (container) (typed FeaturePython)
  Dunit = g/cm3
  Dvalue = 1.2
  Group = -> [H_element022,C_element026,O_element027]
  conduct = 2
  density = 1
  expand = 3
  formula = G4_CELLULOSE_BUTYRATE
  name = G4_CELLULOSE_BUTYRATE
  specific = 4
FEATURE [App::DocumentObjectGroupPython] H_element023  label="H_element : 0.029"  # scripted group (container) (typed FeaturePython)
  n = 0.029216
FEATURE [App::DocumentObjectGroupPython] C_element027  label="C_element : 0.271"  # scripted group (container) (typed FeaturePython)
  n = 0.271296
FEATURE [App::DocumentObjectGroupPython] N_element013  label="N_element : 0.121"  # scripted group (container) (typed FeaturePython)
  n = 0.121276
FEATURE [App::DocumentObjectGroupPython] O_element028  label="O_element : 0.578"  # scripted group (container) (typed FeaturePython)
  n = 0.578212
FEATURE [App::DocumentObjectGroupPython] G4_CELLULOSE_NITRATE  # scripted group (container) (typed FeaturePython)
  Dunit = g/cm3
  Dvalue = 1.49
  Group = -> [H_element023,C_element027,N_element013,O_element028]
  conduct = 2
  density = 1
  expand = 3
  formula = G4_CELLULOSE_NITRATE
  name = G4_CELLULOSE_NITRATE
  specific = 4
FEATURE [App::DocumentObjectGroupPython] H_element024  label="H_element : 0.108"  # scripted group (container) (typed FeaturePython)
  n = 0.107596
FEATURE [App::DocumentObjectGroupPython] N_element014  label="N_element : 0.001"  # scripted group (container) (typed FeaturePython)
  n = 0.0008
FEATURE [App::DocumentObjectGroupPython] O_element029  label="O_element : 0.875"  # scripted group (container) (typed FeaturePython)
  n = 0.874976
FEATURE [App::DocumentObjectGroupPython] S_element008  label="S_element : 0.015"  # scripted group (container) (typed FeaturePython)
  n = 0.014627
FEATURE [App::DocumentObjectGroupPython] Ce_element001  label="Ce_element : 0.002"  # scripted group (container) (typed FeaturePython)
  n = 0.002001
FEATURE [App::DocumentObjectGroupPython] G4_CERIC_SULFATE  # scripted group (container) (typed FeaturePython)
  Dunit = g/cm3
  Dvalue = 1.03
  Group = -> [H_element024,N_element014,O_element029,S_element008,Ce_element001]
  conduct = 2
  density = 1
  expand = 3
  formula = G4_CERIC_SULFATE
  name = G4_CERIC_SULFATE
  specific = 4
FEATURE [App::DocumentObjectGroupPython] Cs_element001  label="Cs_element : 1"  # scripted group (container) (typed FeaturePython)
  n = 1
  ref = Cs_element
FEATURE [App::DocumentObjectGroupPython] F_element006  label="F_element : 1"  # scripted group (container) (typed FeaturePython)
  n = 1
  ref = F_element
FEATURE [App::DocumentObjectGroupPython] G4_CESIUM_FLUORIDE  # scripted group (container) (typed FeaturePython)
  Dunit = g/cm3
  Dvalue = 4.115
  Group = -> [Cs_element001,F_element006]
  conduct = 2
  density = 1
  expand = 3
  formula = G4_CESIUM_FLUORIDE
  name = G4_CESIUM_FLUORIDE
  specific = 4
FEATURE [App::DocumentObjectGroupPython] Cs_element002  label="Cs_element : 002"  # scripted group (container) (typed FeaturePython)
  n = 1
  ref = Cs_element
FEATURE [App::DocumentObjectGroupPython] I_element001  label="I_element : 1"  # scripted group (container) (typed FeaturePython)
  n = 1
  ref = I_element
FEATURE [App::DocumentObjectGroupPython] G4_CESIUM_IODIDE  # scripted group (container) (typed FeaturePython)
  Dunit = g/cm3
  Dvalue = 4.51
  Group = -> [Cs_element002,I_element001]
  conduct = 2
  density = 1
  expand = 3
  formula = G4_CESIUM_IODIDE
  name = G4_CESIUM_IODIDE
  specific = 4
FEATURE [App::DocumentObjectGroupPython] C_element028  label="C_element : 013"  # scripted group (container) (typed FeaturePython)
  n = 6
  ref = C_element
FEATURE [App::DocumentObjectGroupPython] H_element025  label="H_element : 013"  # scripted group (container) (typed FeaturePython)
  n = 5
  ref = H_element
FEATURE [App::DocumentObjectGroupPython] Cl_element005  label="Cl_element : 1"  # scripted group (container) (typed FeaturePython)
  n = 1
  ref = Cl_element
FEATURE [App::DocumentObjectGroupPython] G4_CHLOROBENZENE  # scripted group (container) (typed FeaturePython)
  Dunit = g/cm3
  Dvalue = 1.1058
  Group = -> [C_element028,H_element025,Cl_element005]
  conduct = 2
  density = 1
  expand = 3
  formula = G4_CHLOROBENZENE
  name = G4_CHLOROBENZENE
  specific = 4
FEATURE [App::DocumentObjectGroupPython] C_element029  label="C_element : 014"  # scripted group (container) (typed FeaturePython)
  n = 1
  ref = C_element
FEATURE [App::DocumentObjectGroupPython] H_element026  label="H_element : 1"  # scripted group (container) (typed FeaturePython)
  n = 1
  ref = H_element
FEATURE [App::DocumentObjectGroupPython] Cl_element006  label="Cl_element : 3"  # scripted group (container) (typed FeaturePython)
  n = 3
  ref = Cl_element
FEATURE [App::DocumentObjectGroupPython] G4_CHLOROFORM  # scripted group (container) (typed FeaturePython)
  Dunit = g/cm3
  Dvalue = 1.4832
  Group = -> [C_element029,H_element026,Cl_element006]
  conduct = 2
  density = 1
  expand = 3
  formula = G4_CHLOROFORM
  name = G4_CHLOROFORM
  specific = 4
FEATURE [App::DocumentObjectGroupPython] H_element027  label="H_element : 0.010"  # scripted group (container) (typed FeaturePython)
  n = 0.01
FEATURE [App::DocumentObjectGroupPython] C_element030  label="C_element : 0.001"  # scripted group (container) (typed FeaturePython)
  n = 0.001
FEATURE [App::DocumentObjectGroupPython] O_element030  label="O_element : 0.529"  # scripted group (container) (typed FeaturePython)
  n = 0.529107
FEATURE [App::DocumentObjectGroupPython] Na_element005  label="Na_element : 0.016"  # scripted group (container) (typed FeaturePython)
  n = 0.016
FEATURE [App::DocumentObjectGroupPython] Mg_element003  label="Mg_element : 0.004"  # scripted group (container) (typed FeaturePython)
  n = 0.002
FEATURE [App::DocumentObjectGroupPython] Al_element002  label="Al_element : 0.034"  # scripted group (container) (typed FeaturePython)
  n = 0.033872
FEATURE [App::DocumentObjectGroupPython] Si_element002  label="Si_element : 0.337"  # scripted group (container) (typed FeaturePython)
  n = 0.337021
FEATURE [App::DocumentObjectGroupPython] K_element003  label="K_element : 0.013"  # scripted group (container) (typed FeaturePython)
  n = 0.013
FEATURE [App::DocumentObjectGroupPython] Ca_element010  label="Ca_element : 0.044"  # scripted group (container) (typed FeaturePython)
  n = 0.044
FEATURE [App::DocumentObjectGroupPython] Fe_element002  label="Fe_element : 0.014"  # scripted group (container) (typed FeaturePython)
  n = 0.014
FEATURE [App::DocumentObjectGroupPython] G4_CONCRETE  # scripted group (container) (typed FeaturePython)
  Dunit = g/cm3
  Dvalue = 2.3
  Group = -> [H_element027,C_element030,O_element030,Na_element005,Mg_element003,Al_element002,Si_element002,K_element003,Ca_element010,Fe_element002]
  conduct = 2
  density = 1
  expand = 3
  formula = G4_CONCRETE
  name = G4_CONCRETE
  specific = 4
FEATURE [App::DocumentObjectGroupPython] C_element031  label="C_element : 015"  # scripted group (container) (typed FeaturePython)
  n = 6
  ref = C_element
FEATURE [App::DocumentObjectGroupPython] H_element028  label="H_element : 12"  # scripted group (container) (typed FeaturePython)
  n = 12
  ref = H_element
FEATURE [App::DocumentObjectGroupPython] G4_CYCLOHEXANE  # scripted group (container) (typed FeaturePython)
  Dunit = g/cm3
  Dvalue = 0.779
  Group = -> [C_element031,H_element028]
  conduct = 2
  density = 1
  expand = 3
  formula = G4_CYCLOHEXANE
  name = G4_CYCLOHEXANE
  specific = 4
FEATURE [App::DocumentObjectGroupPython] C_element032  label="C_element : 016"  # scripted group (container) (typed FeaturePython)
  n = 6
  ref = C_element
FEATURE [App::DocumentObjectGroupPython] H_element029  label="H_element : 4"  # scripted group (container) (typed FeaturePython)
  n = 4
  ref = H_element
FEATURE [App::DocumentObjectGroupPython] Cl_element007  label="Cl_element : 2"  # scripted group (container) (typed FeaturePython)
  n = 2
  ref = Cl_element
FEATURE [App::DocumentObjectGroupPython] G4_1_2_DICHLOROBENZENE  label="G4_1.2-DICHLOROBENZENE"  # scripted group (container) (typed FeaturePython)
  Dunit = g/cm3
  Dvalue = 1.3048
  Group = -> [C_element032,H_element029,Cl_element007]
  conduct = 2
  density = 1
  expand = 3
  formula = G4_1.2-DICHLOROBENZENE
  name = G4_1.2-DICHLOROBENZENE
  specific = 4
FEATURE [App::DocumentObjectGroupPython] C_element033  label="C_element : 017"  # scripted group (container) (typed FeaturePython)
  n = 4
  ref = C_element
FEATURE [App::DocumentObjectGroupPython] H_element030  label="H_element : 8"  # scripted group (container) (typed FeaturePython)
  n = 8
  ref = H_element
FEATURE [App::DocumentObjectGroupPython] O_element031  label="O_element : 014"  # scripted group (container) (typed FeaturePython)
  n = 1
  ref = O_element
FEATURE [App::DocumentObjectGroupPython] Cl_element008  label="Cl_element : 005"  # scripted group (container) (typed FeaturePython)
  n = 2
  ref = Cl_element
FEATURE [App::DocumentObjectGroupPython] G4_DICHLORODIETHYL_ETHER  # scripted group (container) (typed FeaturePython)
  Dunit = g/cm3
  Dvalue = 1.2199
  Group = -> [C_element033,H_element030,O_element031,Cl_element008]
  conduct = 2
  density = 1
  expand = 3
  formula = G4_DICHLORODIETHYL_ETHER
  name = G4_DICHLORODIETHYL_ETHER
  specific = 4
FEATURE [App::DocumentObjectGroupPython] C_element034  label="C_element : 018"  # scripted group (container) (typed FeaturePython)
  n = 2
  ref = C_element
FEATURE [App::DocumentObjectGroupPython] H_element031  label="H_element : 014"  # scripted group (container) (typed FeaturePython)
  n = 4
  ref = H_element
FEATURE [App::DocumentObjectGroupPython] Cl_element009  label="Cl_element : 006"  # scripted group (container) (typed FeaturePython)
  n = 2
  ref = Cl_element
FEATURE [App::DocumentObjectGroupPython] G4_1_2_DICHLOROETHANE  label="G4_1.2-DICHLOROETHANE"  # scripted group (container) (typed FeaturePython)
  Dunit = g/cm3
  Dvalue = 1.2351
  Group = -> [C_element034,H_element031,Cl_element009]
  conduct = 2
  density = 1
  expand = 3
  formula = G4_1.2-DICHLOROETHANE
  name = G4_1.2-DICHLOROETHANE
  specific = 4
FEATURE [App::DocumentObjectGroupPython] C_element035  label="C_element : 019"  # scripted group (container) (typed FeaturePython)
  n = 4
  ref = C_element
FEATURE [App::DocumentObjectGroupPython] H_element032  label="H_element : 015"  # scripted group (container) (typed FeaturePython)
  n = 10
  ref = H_element
FEATURE [App::DocumentObjectGroupPython] O_element032  label="O_element : 015"  # scripted group (container) (typed FeaturePython)
  n = 1
  ref = O_element
FEATURE [App::DocumentObjectGroupPython] G4_DIETHYL_ETHER  # scripted group (container) (typed FeaturePython)
  Dunit = g/cm3
  Dvalue = 0.71378
  Group = -> [C_element035,H_element032,O_element032]
  conduct = 2
  density = 1
  expand = 3
  formula = G4_DIETHYL_ETHER
  name = G4_DIETHYL_ETHER
  specific = 4
FEATURE [App::DocumentObjectGroupPython] C_element036  label="C_element : 020"  # scripted group (container) (typed FeaturePython)
  n = 3
  ref = C_element
FEATURE [App::DocumentObjectGroupPython] H_element033  label="H_element : 016"  # scripted group (container) (typed FeaturePython)
  n = 7
  ref = H_element
FEATURE [App::DocumentObjectGroupPython] N_element015  label="N_element : 008"  # scripted group (container) (typed FeaturePython)
  n = 1
  ref = N_element
FEATURE [App::DocumentObjectGroupPython] O_element033  label="O_element : 016"  # scripted group (container) (typed FeaturePython)
  n = 1
  ref = O_element
FEATURE [App::DocumentObjectGroupPython] G4_N_N_DIMETHYL_FORMAMIDE  label="G4_N.N-DIMETHYL_FORMAMIDE"  # scripted group (container) (typed FeaturePython)
  Dunit = g/cm3
  Dvalue = 0.9487
  Group = -> [C_element036,H_element033,N_element015,O_element033]
  conduct = 2
  density = 1
  expand = 3
  formula = G4_N.N-DIMETHYL_FORMAMIDE
  name = G4_N.N-DIMETHYL_FORMAMIDE
  specific = 4
FEATURE [App::DocumentObjectGroupPython] C_element037  label="C_element : 021"  # scripted group (container) (typed FeaturePython)
  n = 2
  ref = C_element
FEATURE [App::DocumentObjectGroupPython] H_element034  label="H_element : 017"  # scripted group (container) (typed FeaturePython)
  n = 6
  ref = H_element
FEATURE [App::DocumentObjectGroupPython] O_element034  label="O_element : 017"  # scripted group (container) (typed FeaturePython)
  n = 1
  ref = O_element
FEATURE [App::DocumentObjectGroupPython] S_element009  label="S_element : 003"  # scripted group (container) (typed FeaturePython)
  n = 1
  ref = S_element
FEATURE [App::DocumentObjectGroupPython] G4_DIMETHYL_SULFOXIDE  # scripted group (container) (typed FeaturePython)
  Dunit = g/cm3
  Dvalue = 1.1014
  Group = -> [C_element037,H_element034,O_element034,S_element009]
  conduct = 2
  density = 1
  expand = 3
  formula = G4_DIMETHYL_SULFOXIDE
  name = G4_DIMETHYL_SULFOXIDE
  specific = 4
FEATURE [App::DocumentObjectGroupPython] C_element038  label="C_element : 022"  # scripted group (container) (typed FeaturePython)
  n = 2
  ref = C_element
FEATURE [App::DocumentObjectGroupPython] H_element035  label="H_element : 018"  # scripted group (container) (typed FeaturePython)
  n = 6
  ref = H_element
FEATURE [App::DocumentObjectGroupPython] G4_ETHANE  # scripted group (container) (typed FeaturePython)
  Dunit = g/cm3
  Dvalue = 0.00125324
  Group = -> [C_element038,H_element035]
  conduct = 2
  density = 1
  expand = 3
  formula = G4_ETHANE
  name = G4_ETHANE
  specific = 4
FEATURE [App::DocumentObjectGroupPython] C_element039  label="C_element : 023"  # scripted group (container) (typed FeaturePython)
  n = 2
  ref = C_element
FEATURE [App::DocumentObjectGroupPython] H_element036  label="H_element : 019"  # scripted group (container) (typed FeaturePython)
  n = 6
  ref = H_element
FEATURE [App::DocumentObjectGroupPython] O_element035  label="O_element : 018"  # scripted group (container) (typed FeaturePython)
  n = 1
  ref = O_element
FEATURE [App::DocumentObjectGroupPython] G4_ETHYL_ALCOHOL  # scripted group (container) (typed FeaturePython)
  Dunit = g/cm3
  Dvalue = 0.7893
  Group = -> [C_element039,H_element036,O_element035]
  conduct = 2
  density = 1
  expand = 3
  formula = G4_ETHYL_ALCOHOL
  name = G4_ETHYL_ALCOHOL
  specific = 4
FEATURE [App::DocumentObjectGroupPython] H_element037  label="H_element : 0.090"  # scripted group (container) (typed FeaturePython)
  n = 0.090027
FEATURE [App::DocumentObjectGroupPython] C_element040  label="C_element : 0.585"  # scripted group (container) (typed FeaturePython)
  n = 0.585182
FEATURE [App::DocumentObjectGroupPython] O_element036  label="O_element : 0.325"  # scripted group (container) (typed FeaturePython)
  n = 0.324791
FEATURE [App::DocumentObjectGroupPython] G4_ETHYL_CELLULOSE  # scripted group (container) (typed FeaturePython)
  Dunit = g/cm3
  Dvalue = 1.13
  Group = -> [H_element037,C_element040,O_element036]
  conduct = 2
  density = 1
  expand = 3
  formula = G4_ETHYL_CELLULOSE
  name = G4_ETHYL_CELLULOSE
  specific = 4
FEATURE [App::DocumentObjectGroupPython] C_element041  label="C_element : 024"  # scripted group (container) (typed FeaturePython)
  n = 2
  ref = C_element
FEATURE [App::DocumentObjectGroupPython] H_element038  label="H_element : 020"  # scripted group (container) (typed FeaturePython)
  n = 4
  ref = H_element
FEATURE [App::DocumentObjectGroupPython] G4_ETHYLENE  # scripted group (container) (typed FeaturePython)
  Dunit = g/cm3
  Dvalue = 0.00117497
  Group = -> [C_element041,H_element038]
  conduct = 2
  density = 1
  expand = 3
  formula = G4_ETHYLENE
  name = G4_ETHYLENE
  specific = 4
FEATURE [App::DocumentObjectGroupPython] H_element039  label="H_element : 0.096"  # scripted group (container) (typed FeaturePython)
  n = 0.096
FEATURE [App::DocumentObjectGroupPython] C_element042  label="C_element : 0.195"  # scripted group (container) (typed FeaturePython)
  n = 0.195
FEATURE [App::DocumentObjectGroupPython] N_element016  label="N_element : 0.057"  # scripted group (container) (typed FeaturePython)
  n = 0.057
FEATURE [App::DocumentObjectGroupPython] O_element037  label="O_element : 0.646"  # scripted group (container) (typed FeaturePython)
  n = 0.646
FEATURE [App::DocumentObjectGroupPython] Na_element006  label="Na_element : 0.017"  # scripted group (container) (typed FeaturePython)
  n = 0.001
FEATURE [App::DocumentObjectGroupPython] P_element005  label="P_element : 0.104"  # scripted group (container) (typed FeaturePython)
  n = 0.001
FEATURE [App::DocumentObjectGroupPython] S_element010  label="S_element : 0.016"  # scripted group (container) (typed FeaturePython)
  n = 0.003
FEATURE [App::DocumentObjectGroupPython] Cl_element010  label="Cl_element : 0.005"  # scripted group (container) (typed FeaturePython)
  n = 0.001
FEATURE [App::DocumentObjectGroupPython] G4_EYE_LENS_ICRP  # scripted group (container) (typed FeaturePython)
  Dunit = g/cm3
  Dvalue = 1.07
  Group = -> [H_element039,C_element042,N_element016,O_element037,Na_element006,P_element005,S_element010,Cl_element010]
  conduct = 2
  density = 1
  expand = 3
  formula = G4_EYE_LENS_ICRP
  name = G4_EYE_LENS_ICRP
  specific = 4
FEATURE [App::DocumentObjectGroupPython] Fe_element003  label="Fe_element : 2"  # scripted group (container) (typed FeaturePython)
  n = 2
  ref = Fe_element
FEATURE [App::DocumentObjectGroupPython] O_element038  label="O_element : 019"  # scripted group (container) (typed FeaturePython)
  n = 3
  ref = O_element
FEATURE [App::DocumentObjectGroupPython] G4_FERRIC_OXIDE  # scripted group (container) (typed FeaturePython)
  Dunit = g/cm3
  Dvalue = 5.2
  Group = -> [Fe_element003,O_element038]
  conduct = 2
  density = 1
  expand = 3
  formula = G4_FERRIC_OXIDE
  name = G4_FERRIC_OXIDE
  specific = 4
FEATURE [App::DocumentObjectGroupPython] Fe_element004  label="Fe_element : 1"  # scripted group (container) (typed FeaturePython)
  n = 1
  ref = Fe_element
FEATURE [App::DocumentObjectGroupPython] B_element003  label="B_element : 1"  # scripted group (container) (typed FeaturePython)
  n = 1
  ref = B_element
FEATURE [App::DocumentObjectGroupPython] G4_FERROBORIDE  # scripted group (container) (typed FeaturePython)
  Dunit = g/cm3
  Dvalue = 7.15
  Group = -> [Fe_element004,B_element003]
  conduct = 2
  density = 1
  expand = 3
  formula = G4_FERROBORIDE
  name = G4_FERROBORIDE
  specific = 4
FEATURE [App::DocumentObjectGroupPython] Fe_element005  label="Fe_element : 003"  # scripted group (container) (typed FeaturePython)
  n = 1
  ref = Fe_element
FEATURE [App::DocumentObjectGroupPython] O_element039  label="O_element : 020"  # scripted group (container) (typed FeaturePython)
  n = 1
  ref = O_element
FEATURE [App::DocumentObjectGroupPython] G4_FERROUS_OXIDE  # scripted group (container) (typed FeaturePython)
  Dunit = g/cm3
  Dvalue = 5.7
  Group = -> [Fe_element005,O_element039]
  conduct = 2
  density = 1
  expand = 3
  formula = G4_FERROUS_OXIDE
  name = G4_FERROUS_OXIDE
  specific = 4
FEATURE [App::DocumentObjectGroupPython] H_element040  label="H_element : 0.115"  # scripted group (container) (typed FeaturePython)
  n = 0.108259
FEATURE [App::DocumentObjectGroupPython] N_element017  label="N_element : 0.000"  # scripted group (container) (typed FeaturePython)
  n = 2.7e-05
FEATURE [App::DocumentObjectGroupPython] O_element040  label="O_element : 0.879"  # scripted group (container) (typed FeaturePython)
  n = 0.878636
FEATURE [App::DocumentObjectGroupPython] Na_element007  label="Na_element : 0.000"  # scripted group (container) (typed FeaturePython)
  n = 2.2e-05
FEATURE [App::DocumentObjectGroupPython] S_element011  label="S_element : 0.013"  # scripted group (container) (typed FeaturePython)
  n = 0.012968
FEATURE [App::DocumentObjectGroupPython] Cl_element011  label="Cl_element : 0.000"  # scripted group (container) (typed FeaturePython)
  n = 3.4e-05
FEATURE [App::DocumentObjectGroupPython] Fe_element006  label="Fe_element : 0.000"  # scripted group (container) (typed FeaturePython)
  n = 5.4e-05
FEATURE [App::DocumentObjectGroupPython] G4_FERROUS_SULFATE  # scripted group (container) (typed FeaturePython)
  Dunit = g/cm3
  Dvalue = 1.024
  Group = -> [H_element040,N_element017,O_element040,Na_element007,S_element011,Cl_element011,Fe_element006]
  conduct = 2
  density = 1
  expand = 3
  formula = G4_FERROUS_SULFATE
  name = G4_FERROUS_SULFATE
  specific = 4
FEATURE [App::DocumentObjectGroupPython] C_element043  label="C_element : 0.099"  # scripted group (container) (typed FeaturePython)
  n = 0.099335
FEATURE [App::DocumentObjectGroupPython] F_element007  label="F_element : 0.314"  # scripted group (container) (typed FeaturePython)
  n = 0.314247
FEATURE [App::DocumentObjectGroupPython] Cl_element012  label="Cl_element : 0.586"  # scripted group (container) (typed FeaturePython)
  n = 0.586418
FEATURE [App::DocumentObjectGroupPython] G4_FREON_12  label="G4_FREON-12"  # scripted group (container) (typed FeaturePython)
  Dunit = g/cm3
  Dvalue = 1.12
  Group = -> [C_element043,F_element007,Cl_element012]
  conduct = 2
  density = 1
  expand = 3
  formula = G4_FREON-12
  name = G4_FREON-12
  specific = 4
FEATURE [App::DocumentObjectGroupPython] C_element044  label="C_element : 0.057"  # scripted group (container) (typed FeaturePython)
  n = 0.057245
FEATURE [App::DocumentObjectGroupPython] F_element008  label="F_element : 0.181"  # scripted group (container) (typed FeaturePython)
  n = 0.181096
FEATURE [App::DocumentObjectGroupPython] Br_element001  label="Br_element : 0.762"  # scripted group (container) (typed FeaturePython)
  n = 0.761659
FEATURE [App::DocumentObjectGroupPython] G4_FREON_12B2  label="G4_FREON-12B2"  # scripted group (container) (typed FeaturePython)
  Dunit = g/cm3
  Dvalue = 1.8
  Group = -> [C_element044,F_element008,Br_element001]
  conduct = 2
  density = 1
  expand = 3
  formula = G4_FREON-12B2
  name = G4_FREON-12B2
  specific = 4
FEATURE [App::DocumentObjectGroupPython] C_element045  label="C_element : 0.115"  # scripted group (container) (typed FeaturePython)
  n = 0.114983
FEATURE [App::DocumentObjectGroupPython] F_element009  label="F_element : 0.546"  # scripted group (container) (typed FeaturePython)
  n = 0.545621
FEATURE [App::DocumentObjectGroupPython] Cl_element013  label="Cl_element : 0.339"  # scripted group (container) (typed FeaturePython)
  n = 0.339396
FEATURE [App::DocumentObjectGroupPython] G4_FREON_13  label="G4_FREON-13"  # scripted group (container) (typed FeaturePython)
  Dunit = g/cm3
  Dvalue = 0.95
  Group = -> [C_element045,F_element009,Cl_element013]
  conduct = 2
  density = 1
  expand = 3
  formula = G4_FREON-13
  name = G4_FREON-13
  specific = 4
FEATURE [App::DocumentObjectGroupPython] C_element046  label="C_element : 025"  # scripted group (container) (typed FeaturePython)
  n = 1
  ref = C_element
FEATURE [App::DocumentObjectGroupPython] F_element010  label="F_element : 3"  # scripted group (container) (typed FeaturePython)
  n = 3
  ref = F_element
FEATURE [App::DocumentObjectGroupPython] Br_element002  label="Br_element : 1"  # scripted group (container) (typed FeaturePython)
  n = 1
  ref = Br_element
FEATURE [App::DocumentObjectGroupPython] G4_FREON_13B1  label="G4_FREON-13B1"  # scripted group (container) (typed FeaturePython)
  Dunit = g/cm3
  Dvalue = 1.5
  Group = -> [C_element046,F_element010,Br_element002]
  conduct = 2
  density = 1
  expand = 3
  formula = G4_FREON-13B1
  name = G4_FREON-13B1
  specific = 4
FEATURE [App::DocumentObjectGroupPython] C_element047  label="C_element : 0.061"  # scripted group (container) (typed FeaturePython)
  n = 0.061309
FEATURE [App::DocumentObjectGroupPython] F_element011  label="F_element : 0.291"  # scripted group (container) (typed FeaturePython)
  n = 0.290924
FEATURE [App::DocumentObjectGroupPython] I_element002  label="I_element : 0.648"  # scripted group (container) (typed FeaturePython)
  n = 0.647767
FEATURE [App::DocumentObjectGroupPython] G4_FREON_13I1  label="G4_FREON-13I1"  # scripted group (container) (typed FeaturePython)
  Dunit = g/cm3
  Dvalue = 1.8
  Group = -> [C_element047,F_element011,I_element002]
  conduct = 2
  density = 1
  expand = 3
  formula = G4_FREON-13I1
  name = G4_FREON-13I1
  specific = 4
FEATURE [App::DocumentObjectGroupPython] Gd_element001  label="Gd_element : 2"  # scripted group (container) (typed FeaturePython)
  n = 2
  ref = Gd_element
FEATURE [App::DocumentObjectGroupPython] O_element041  label="O_element : 021"  # scripted group (container) (typed FeaturePython)
  n = 2
  ref = O_element
FEATURE [App::DocumentObjectGroupPython] S_element012  label="S_element : 004"  # scripted group (container) (typed FeaturePython)
  n = 1
  ref = S_element
FEATURE [App::DocumentObjectGroupPython] G4_GADOLINIUM_OXYSULFIDE  # scripted group (container) (typed FeaturePython)
  Dunit = g/cm3
  Dvalue = 7.44
  Group = -> [Gd_element001,O_element041,S_element012]
  conduct = 2
  density = 1
  expand = 3
  formula = G4_GADOLINIUM_OXYSULFIDE
  name = G4_GADOLINIUM_OXYSULFIDE
  specific = 4
FEATURE [App::DocumentObjectGroupPython] Ga_element001  label="Ga_element : 1"  # scripted group (container) (typed FeaturePython)
  n = 1
  ref = Ga_element
FEATURE [App::DocumentObjectGroupPython] As_element001  label="As_element : 1"  # scripted group (container) (typed FeaturePython)
  n = 1
  ref = As_element
FEATURE [App::DocumentObjectGroupPython] G4_GALLIUM_ARSENIDE  # scripted group (container) (typed FeaturePython)
  Dunit = g/cm3
  Dvalue = 5.31
  Group = -> [Ga_element001,As_element001]
  conduct = 2
  density = 1
  expand = 3
  formula = G4_GALLIUM_ARSENIDE
  name = G4_GALLIUM_ARSENIDE
  specific = 4
FEATURE [App::DocumentObjectGroupPython] H_element041  label="H_element : 0.081"  # scripted group (container) (typed FeaturePython)
  n = 0.08118
FEATURE [App::DocumentObjectGroupPython] C_element048  label="C_element : 0.416"  # scripted group (container) (typed FeaturePython)
  n = 0.41606
FEATURE [App::DocumentObjectGroupPython] N_element018  label="N_element : 0.111"  # scripted group (container) (typed FeaturePython)
  n = 0.11124
FEATURE [App::DocumentObjectGroupPython] O_element042  label="O_element : 0.381"  # scripted group (container) (typed FeaturePython)
  n = 0.38064
FEATURE [App::DocumentObjectGroupPython] S_element013  label="S_element : 0.011"  # scripted group (container) (typed FeaturePython)
  n = 0.01088
FEATURE [App::DocumentObjectGroupPython] G4_GEL_PHOTO_EMULSION  # scripted group (container) (typed FeaturePython)
  Dunit = g/cm3
  Dvalue = 1.2914
  Group = -> [H_element041,C_element048,N_element018,O_element042,S_element013]
  conduct = 2
  density = 1
  expand = 3
  formula = G4_GEL_PHOTO_EMULSION
  name = G4_GEL_PHOTO_EMULSION
  specific = 4
FEATURE [App::DocumentObjectGroupPython] B_element004  label="B_element : 0.040"  # scripted group (container) (typed FeaturePython)
  n = 0.0400639
FEATURE [App::DocumentObjectGroupPython] O_element043  label="O_element : 0.540"  # scripted group (container) (typed FeaturePython)
  n = 0.539561
FEATURE [App::DocumentObjectGroupPython] Na_element008  label="Na_element : 0.028"  # scripted group (container) (typed FeaturePython)
  n = 0.0281909
FEATURE [App::DocumentObjectGroupPython] Al_element003  label="Al_element : 0.012"  # scripted group (container) (typed FeaturePython)
  n = 0.011644
FEATURE [App::DocumentObjectGroupPython] Si_element003  label="Si_element : 0.377"  # scripted group (container) (typed FeaturePython)
  n = 0.377219
FEATURE [App::DocumentObjectGroupPython] K_element004  label="K_element : 0.014"  # scripted group (container) (typed FeaturePython)
  n = 0.00332099
FEATURE [App::DocumentObjectGroupPython] G4_Pyrex_Glass  # scripted group (container) (typed FeaturePython)
  Dunit = g/cm3
  Dvalue = 2.23
  Group = -> [B_element004,O_element043,Na_element008,Al_element003,Si_element003,K_element004]
  conduct = 2
  density = 1
  expand = 3
  formula = G4_Pyrex_Glass
  name = G4_Pyrex_Glass
  specific = 4
FEATURE [App::DocumentObjectGroupPython] O_element044  label="O_element : 0.156"  # scripted group (container) (typed FeaturePython)
  n = 0.156453
FEATURE [App::DocumentObjectGroupPython] Si_element004  label="Si_element : 0.081"  # scripted group (container) (typed FeaturePython)
  n = 0.080866
FEATURE [App::DocumentObjectGroupPython] Ti_element001  label="Ti_element : 0.008"  # scripted group (container) (typed FeaturePython)
  n = 0.008092
FEATURE [App::DocumentObjectGroupPython] As_element002  label="As_element : 0.003"  # scripted group (container) (typed FeaturePython)
  n = 0.002651
FEATURE [App::DocumentObjectGroupPython] Pb_element001  label="Pb_element : 0.752"  # scripted group (container) (typed FeaturePython)
  n = 0.751938
FEATURE [App::DocumentObjectGroupPython] G4_GLASS_LEAD  # scripted group (container) (typed FeaturePython)
  Dunit = g/cm3
  Dvalue = 6.22
  Group = -> [O_element044,Si_element004,Ti_element001,As_element002,Pb_element001]
  conduct = 2
  density = 1
  expand = 3
  formula = G4_GLASS_LEAD
  name = G4_GLASS_LEAD
  specific = 4
FEATURE [App::DocumentObjectGroupPython] O_element045  label="O_element : 0.460"  # scripted group (container) (typed FeaturePython)
  n = 0.4598
FEATURE [App::DocumentObjectGroupPython] Na_element009  label="Na_element : 0.096"  # scripted group (container) (typed FeaturePython)
  n = 0.0964411
FEATURE [App::DocumentObjectGroupPython] Si_element005  label="Si_element : 0.378"  # scripted group (container) (typed FeaturePython)
  n = 0.336553
FEATURE [App::DocumentObjectGroupPython] Ca_element011  label="Ca_element : 0.107"  # scripted group (container) (typed FeaturePython)
  n = 0.107205
FEATURE [App::DocumentObjectGroupPython] G4_GLASS_PLATE  # scripted group (container) (typed FeaturePython)
  Dunit = g/cm3
  Dvalue = 2.4
  Group = -> [O_element045,Na_element009,Si_element005,Ca_element011]
  conduct = 2
  density = 1
  expand = 3
  formula = G4_GLASS_PLATE
  name = G4_GLASS_PLATE
  specific = 4
FEATURE [App::DocumentObjectGroupPython] C_element049  label="C_element : 026"  # scripted group (container) (typed FeaturePython)
  n = 5
  ref = C_element
FEATURE [App::DocumentObjectGroupPython] H_element042  label="H_element : 021"  # scripted group (container) (typed FeaturePython)
  n = 10
  ref = H_element
FEATURE [App::DocumentObjectGroupPython] N_element019  label="N_element : 2"  # scripted group (container) (typed FeaturePython)
  n = 2
  ref = N_element
FEATURE [App::DocumentObjectGroupPython] O_element046  label="O_element : 022"  # scripted group (container) (typed FeaturePython)
  n = 3
  ref = O_element
FEATURE [App::DocumentObjectGroupPython] G4_GLUTAMINE  # scripted group (container) (typed FeaturePython)
  Dunit = g/cm3
  Dvalue = 1.46
  Group = -> [C_element049,H_element042,N_element019,O_element046]
  conduct = 2
  density = 1
  expand = 3
  formula = G4_GLUTAMINE
  name = G4_GLUTAMINE
  specific = 4
FEATURE [App::DocumentObjectGroupPython] C_element050  label="C_element : 027"  # scripted group (container) (typed FeaturePython)
  n = 3
  ref = C_element
FEATURE [App::DocumentObjectGroupPython] H_element043  label="H_element : 022"  # scripted group (container) (typed FeaturePython)
  n = 8
  ref = H_element
FEATURE [App::DocumentObjectGroupPython] O_element047  label="O_element : 023"  # scripted group (container) (typed FeaturePython)
  n = 3
  ref = O_element
FEATURE [App::DocumentObjectGroupPython] G4_GLYCEROL  # scripted group (container) (typed FeaturePython)
  Dunit = g/cm3
  Dvalue = 1.2613
  Group = -> [C_element050,H_element043,O_element047]
  conduct = 2
  density = 1
  expand = 3
  formula = G4_GLYCEROL
  name = G4_GLYCEROL
  specific = 4
FEATURE [App::DocumentObjectGroupPython] C_element051  label="C_element : 028"  # scripted group (container) (typed FeaturePython)
  n = 5
  ref = C_element
FEATURE [App::DocumentObjectGroupPython] H_element044  label="H_element : 023"  # scripted group (container) (typed FeaturePython)
  n = 5
  ref = H_element
FEATURE [App::DocumentObjectGroupPython] N_element020  label="N_element : 009"  # scripted group (container) (typed FeaturePython)
  n = 5
  ref = N_element
FEATURE [App::DocumentObjectGroupPython] O_element048  label="O_element : 024"  # scripted group (container) (typed FeaturePython)
  n = 1
  ref = O_element
FEATURE [App::DocumentObjectGroupPython] G4_GUANINE  # scripted group (container) (typed FeaturePython)
  Dunit = g/cm3
  Dvalue = 2.2
  Group = -> [C_element051,H_element044,N_element020,O_element048]
  conduct = 2
  density = 1
  expand = 3
  formula = G4_GUANINE
  name = G4_GUANINE
  specific = 4
FEATURE [App::DocumentObjectGroupPython] Ca_element012  label="Ca_element : 006"  # scripted group (container) (typed FeaturePython)
  n = 1
  ref = Ca_element
FEATURE [App::DocumentObjectGroupPython] S_element014  label="S_element : 005"  # scripted group (container) (typed FeaturePython)
  n = 1
  ref = S_element
FEATURE [App::DocumentObjectGroupPython] O_element049  label="O_element : 6"  # scripted group (container) (typed FeaturePython)
  n = 6
  ref = O_element
FEATURE [App::DocumentObjectGroupPython] H_element045  label="H_element : 024"  # scripted group (container) (typed FeaturePython)
  n = 4
  ref = H_element
FEATURE [App::DocumentObjectGroupPython] G4_GYPSUM  # scripted group (container) (typed FeaturePython)
  Dunit = g/cm3
  Dvalue = 2.32
  Group = -> [Ca_element012,S_element014,O_element049,H_element045]
  conduct = 2
  density = 1
  expand = 3
  formula = G4_GYPSUM
  name = G4_GYPSUM
  specific = 4
FEATURE [App::DocumentObjectGroupPython] C_element052  label="C_element : 7"  # scripted group (container) (typed FeaturePython)
  n = 7
  ref = C_element
FEATURE [App::DocumentObjectGroupPython] H_element046  label="H_element : 16"  # scripted group (container) (typed FeaturePython)
  n = 16
  ref = H_element
FEATURE [App::DocumentObjectGroupPython] G4_N_HEPTANE  label="G4_N-HEPTANE"  # scripted group (container) (typed FeaturePython)
  Dunit = g/cm3
  Dvalue = 0.68376
  Group = -> [C_element052,H_element046]
  conduct = 2
  density = 1
  expand = 3
  formula = G4_N-HEPTANE
  name = G4_N-HEPTANE
  specific = 4
FEATURE [App::DocumentObjectGroupPython] C_element053  label="C_element : 029"  # scripted group (container) (typed FeaturePython)
  n = 6
  ref = C_element
FEATURE [App::DocumentObjectGroupPython] H_element047  label="H_element : 14"  # scripted group (container) (typed FeaturePython)
  n = 14
  ref = H_element
FEATURE [App::DocumentObjectGroupPython] G4_N_HEXANE  label="G4_N-HEXANE"  # scripted group (container) (typed FeaturePython)
  Dunit = g/cm3
  Dvalue = 0.6603
  Group = -> [C_element053,H_element047]
  conduct = 2
  density = 1
  expand = 3
  formula = G4_N-HEXANE
  name = G4_N-HEXANE
  specific = 4
FEATURE [App::DocumentObjectGroupPython] C_element054  label="C_element : 22"  # scripted group (container) (typed FeaturePython)
  n = 22
  ref = C_element
FEATURE [App::DocumentObjectGroupPython] H_element048  label="H_element : 025"  # scripted group (container) (typed FeaturePython)
  n = 10
  ref = H_element
FEATURE [App::DocumentObjectGroupPython] N_element021  label="N_element : 010"  # scripted group (container) (typed FeaturePython)
  n = 2
  ref = N_element
FEATURE [App::DocumentObjectGroupPython] O_element050  label="O_element : 025"  # scripted group (container) (typed FeaturePython)
  n = 5
  ref = O_element
FEATURE [App::DocumentObjectGroupPython] G4_KAPTON  # scripted group (container) (typed FeaturePython)
  Dunit = g/cm3
  Dvalue = 1.42
  Group = -> [C_element054,H_element048,N_element021,O_element050]
  conduct = 2
  density = 1
  expand = 3
  formula = G4_KAPTON
  name = G4_KAPTON
  specific = 4
FEATURE [App::DocumentObjectGroupPython] La_element001  label="La_element : 1"  # scripted group (container) (typed FeaturePython)
  n = 1
  ref = La_element
FEATURE [App::DocumentObjectGroupPython] Br_element003  label="Br_element : 002"  # scripted group (container) (typed FeaturePython)
  n = 1
  ref = Br_element
FEATURE [App::DocumentObjectGroupPython] O_element051  label="O_element : 026"  # scripted group (container) (typed FeaturePython)
  n = 1
  ref = O_element
FEATURE [App::DocumentObjectGroupPython] G4_LANTHANUM_OXYBROMIDE  # scripted group (container) (typed FeaturePython)
  Dunit = g/cm3
  Dvalue = 6.28
  Group = -> [La_element001,Br_element003,O_element051]
  conduct = 2
  density = 1
  expand = 3
  formula = G4_LANTHANUM_OXYBROMIDE
  name = G4_LANTHANUM_OXYBROMIDE
  specific = 4
FEATURE [App::DocumentObjectGroupPython] La_element002  label="La_element : 2"  # scripted group (container) (typed FeaturePython)
  n = 2
  ref = La_element
FEATURE [App::DocumentObjectGroupPython] O_element052  label="O_element : 027"  # scripted group (container) (typed FeaturePython)
  n = 2
  ref = O_element
FEATURE [App::DocumentObjectGroupPython] S_element015  label="S_element : 006"  # scripted group (container) (typed FeaturePython)
  n = 1
  ref = S_element
FEATURE [App::DocumentObjectGroupPython] G4_LANTHANUM_OXYSULFIDE  # scripted group (container) (typed FeaturePython)
  Dunit = g/cm3
  Dvalue = 5.86
  Group = -> [La_element002,O_element052,S_element015]
  conduct = 2
  density = 1
  expand = 3
  formula = G4_LANTHANUM_OXYSULFIDE
  name = G4_LANTHANUM_OXYSULFIDE
  specific = 4
FEATURE [App::DocumentObjectGroupPython] O_element053  label="O_element : 0.072"  # scripted group (container) (typed FeaturePython)
  n = 0.071682
FEATURE [App::DocumentObjectGroupPython] Pb_element002  label="Pb_element : 0.928"  # scripted group (container) (typed FeaturePython)
  n = 0.928318
FEATURE [App::DocumentObjectGroupPython] G4_LEAD_OXIDE  # scripted group (container) (typed FeaturePython)
  Dunit = g/cm3
  Dvalue = 9.53
  Group = -> [O_element053,Pb_element002]
  conduct = 2
  density = 1
  expand = 3
  formula = G4_LEAD_OXIDE
  name = G4_LEAD_OXIDE
  specific = 4
FEATURE [App::DocumentObjectGroupPython] Li_element001  label="Li_element : 1"  # scripted group (container) (typed FeaturePython)
  n = 1
  ref = Li_element
FEATURE [App::DocumentObjectGroupPython] N_element022  label="N_element : 011"  # scripted group (container) (typed FeaturePython)
  n = 1
  ref = N_element
FEATURE [App::DocumentObjectGroupPython] H_element049  label="H_element : 026"  # scripted group (container) (typed FeaturePython)
  n = 2
  ref = H_element
FEATURE [App::DocumentObjectGroupPython] G4_LITHIUM_AMIDE  # scripted group (container) (typed FeaturePython)
  Dunit = g/cm3
  Dvalue = 1.178
  Group = -> [Li_element001,N_element022,H_element049]
  conduct = 2
  density = 1
  expand = 3
  formula = G4_LITHIUM_AMIDE
  name = G4_LITHIUM_AMIDE
  specific = 4
FEATURE [App::DocumentObjectGroupPython] Li_element002  label="Li_element : 2"  # scripted group (container) (typed FeaturePython)
  n = 2
  ref = Li_element
FEATURE [App::DocumentObjectGroupPython] C_element055  label="C_element : 030"  # scripted group (container) (typed FeaturePython)
  n = 1
  ref = C_element
FEATURE [App::DocumentObjectGroupPython] O_element054  label="O_element : 028"  # scripted group (container) (typed FeaturePython)
  n = 3
  ref = O_element
FEATURE [App::DocumentObjectGroupPython] G4_LITHIUM_CARBONATE  # scripted group (container) (typed FeaturePython)
  Dunit = g/cm3
  Dvalue = 2.11
  Group = -> [Li_element002,C_element055,O_element054]
  conduct = 2
  density = 1
  expand = 3
  formula = G4_LITHIUM_CARBONATE
  name = G4_LITHIUM_CARBONATE
  specific = 4
FEATURE [App::DocumentObjectGroupPython] Li_element003  label="Li_element : 003"  # scripted group (container) (typed FeaturePython)
  n = 1
  ref = Li_element
FEATURE [App::DocumentObjectGroupPython] F_element012  label="F_element : 004"  # scripted group (container) (typed FeaturePython)
  n = 1
  ref = F_element
FEATURE [App::DocumentObjectGroupPython] G4_LITHIUM_FLUORIDE  # scripted group (container) (typed FeaturePython)
  Dunit = g/cm3
  Dvalue = 2.635
  Group = -> [Li_element003,F_element012]
  conduct = 2
  density = 1
  expand = 3
  formula = G4_LITHIUM_FLUORIDE
  name = G4_LITHIUM_FLUORIDE
  specific = 4
FEATURE [App::DocumentObjectGroupPython] Li_element004  label="Li_element : 004"  # scripted group (container) (typed FeaturePython)
  n = 1
  ref = Li_element
FEATURE [App::DocumentObjectGroupPython] H_element050  label="H_element : 027"  # scripted group (container) (typed FeaturePython)
  n = 1
  ref = H_element
FEATURE [App::DocumentObjectGroupPython] G4_LITHIUM_HYDRIDE  # scripted group (container) (typed FeaturePython)
  Dunit = g/cm3
  Dvalue = 0.82
  Group = -> [Li_element004,H_element050]
  conduct = 2
  density = 1
  expand = 3
  formula = G4_LITHIUM_HYDRIDE
  name = G4_LITHIUM_HYDRIDE
  specific = 4
FEATURE [App::DocumentObjectGroupPython] Li_element005  label="Li_element : 005"  # scripted group (container) (typed FeaturePython)
  n = 1
  ref = Li_element
FEATURE [App::DocumentObjectGroupPython] I_element003  label="I_element : 002"  # scripted group (container) (typed FeaturePython)
  n = 1
  ref = I_element
FEATURE [App::DocumentObjectGroupPython] G4_LITHIUM_IODIDE  # scripted group (container) (typed FeaturePython)
  Dunit = g/cm3
  Dvalue = 3.494
  Group = -> [Li_element005,I_element003]
  conduct = 2
  density = 1
  expand = 3
  formula = G4_LITHIUM_IODIDE
  name = G4_LITHIUM_IODIDE
  specific = 4
FEATURE [App::DocumentObjectGroupPython] Li_element006  label="Li_element : 006"  # scripted group (container) (typed FeaturePython)
  n = 2
  ref = Li_element
FEATURE [App::DocumentObjectGroupPython] O_element055  label="O_element : 029"  # scripted group (container) (typed FeaturePython)
  n = 1
  ref = O_element
FEATURE [App::DocumentObjectGroupPython] G4_LITHIUM_OXIDE  # scripted group (container) (typed FeaturePython)
  Dunit = g/cm3
  Dvalue = 2.013
  Group = -> [Li_element006,O_element055]
  conduct = 2
  density = 1
  expand = 3
  formula = G4_LITHIUM_OXIDE
  name = G4_LITHIUM_OXIDE
  specific = 4
FEATURE [App::DocumentObjectGroupPython] Li_element007  label="Li_element : 007"  # scripted group (container) (typed FeaturePython)
  n = 2
  ref = Li_element
FEATURE [App::DocumentObjectGroupPython] B_element005  label="B_element : 005"  # scripted group (container) (typed FeaturePython)
  n = 4
  ref = B_element
FEATURE [App::DocumentObjectGroupPython] O_element056  label="O_element : 7"  # scripted group (container) (typed FeaturePython)
  n = 7
  ref = O_element
FEATURE [App::DocumentObjectGroupPython] G4_LITHIUM_TETRABORATE  # scripted group (container) (typed FeaturePython)
  Dunit = g/cm3
  Dvalue = 2.44
  Group = -> [Li_element007,B_element005,O_element056]
  conduct = 2
  density = 1
  expand = 3
  formula = G4_LITHIUM_TETRABORATE
  name = G4_LITHIUM_TETRABORATE
  specific = 4
FEATURE [App::DocumentObjectGroupPython] H_element051  label="H_element : 0.105"  # scripted group (container) (typed FeaturePython)
  n = 0.105
FEATURE [App::DocumentObjectGroupPython] C_element056  label="C_element : 0.083"  # scripted group (container) (typed FeaturePython)
  n = 0.083
FEATURE [App::DocumentObjectGroupPython] N_element023  label="N_element : 0.023"  # scripted group (container) (typed FeaturePython)
  n = 0.023
FEATURE [App::DocumentObjectGroupPython] O_element057  label="O_element : 0.779"  # scripted group (container) (typed FeaturePython)
  n = 0.779
FEATURE [App::DocumentObjectGroupPython] Na_element010  label="Na_element : 0.097"  # scripted group (container) (typed FeaturePython)
  n = 0.002
FEATURE [App::DocumentObjectGroupPython] P_element006  label="P_element : 0.105"  # scripted group (container) (typed FeaturePython)
  n = 0.001
FEATURE [App::DocumentObjectGroupPython] S_element016  label="S_element : 0.017"  # scripted group (container) (typed FeaturePython)
  n = 0.002
FEATURE [App::DocumentObjectGroupPython] Cl_element014  label="Cl_element : 0.587"  # scripted group (container) (typed FeaturePython)
  n = 0.003
FEATURE [App::DocumentObjectGroupPython] K_element005  label="K_element : 0.015"  # scripted group (container) (typed FeaturePython)
  n = 0.002
FEATURE [App::DocumentObjectGroupPython] G4_LUNG_ICRP  # scripted group (container) (typed FeaturePython)
  Dunit = g/cm3
  Dvalue = 1.04
  Group = -> [H_element051,C_element056,N_element023,O_element057,Na_element010,P_element006,S_element016,Cl_element014,K_element005]
  conduct = 2
  density = 1
  expand = 3
  formula = G4_LUNG_ICRP
  name = G4_LUNG_ICRP
  specific = 4
FEATURE [App::DocumentObjectGroupPython] H_element052  label="H_element : 0.116"  # scripted group (container) (typed FeaturePython)
  n = 0.114318
FEATURE [App::DocumentObjectGroupPython] C_element057  label="C_element : 0.656"  # scripted group (container) (typed FeaturePython)
  n = 0.655824
FEATURE [App::DocumentObjectGroupPython] O_element058  label="O_element : 0.092"  # scripted group (container) (typed FeaturePython)
  n = 0.0921831
FEATURE [App::DocumentObjectGroupPython] Mg_element004  label="Mg_element : 0.135"  # scripted group (container) (typed FeaturePython)
  n = 0.134792
FEATURE [App::DocumentObjectGroupPython] Ca_element013  label="Ca_element : 0.003"  # scripted group (container) (typed FeaturePython)
  n = 0.002883
FEATURE [App::DocumentObjectGroupPython] G4_M3_WAX  # scripted group (container) (typed FeaturePython)
  Dunit = g/cm3
  Dvalue = 1.05
  Group = -> [H_element052,C_element057,O_element058,Mg_element004,Ca_element013]
  conduct = 2
  density = 1
  expand = 3
  formula = G4_M3_WAX
  name = G4_M3_WAX
  specific = 4
FEATURE [App::DocumentObjectGroupPython] Mg_element005  label="Mg_element : 1"  # scripted group (container) (typed FeaturePython)
  n = 1
  ref = Mg_element
FEATURE [App::DocumentObjectGroupPython] C_element058  label="C_element : 031"  # scripted group (container) (typed FeaturePython)
  n = 1
  ref = C_element
FEATURE [App::DocumentObjectGroupPython] O_element059  label="O_element : 030"  # scripted group (container) (typed FeaturePython)
  n = 3
  ref = O_element
FEATURE [App::DocumentObjectGroupPython] G4_MAGNESIUM_CARBONATE  # scripted group (container) (typed FeaturePython)
  Dunit = g/cm3
  Dvalue = 2.958
  Group = -> [Mg_element005,C_element058,O_element059]
  conduct = 2
  density = 1
  expand = 3
  formula = G4_MAGNESIUM_CARBONATE
  name = G4_MAGNESIUM_CARBONATE
  specific = 4
FEATURE [App::DocumentObjectGroupPython] Mg_element006  label="Mg_element : 002"  # scripted group (container) (typed FeaturePython)
  n = 1
  ref = Mg_element
FEATURE [App::DocumentObjectGroupPython] F_element013  label="F_element : 005"  # scripted group (container) (typed FeaturePython)
  n = 2
  ref = F_element
FEATURE [App::DocumentObjectGroupPython] G4_MAGNESIUM_FLUORIDE  # scripted group (container) (typed FeaturePython)
  Dunit = g/cm3
  Dvalue = 3
  Group = -> [Mg_element006,F_element013]
  conduct = 2
  density = 1
  expand = 3
  formula = G4_MAGNESIUM_FLUORIDE
  name = G4_MAGNESIUM_FLUORIDE
  specific = 4
FEATURE [App::DocumentObjectGroupPython] Mg_element007  label="Mg_element : 003"  # scripted group (container) (typed FeaturePython)
  n = 1
  ref = Mg_element
FEATURE [App::DocumentObjectGroupPython] O_element060  label="O_element : 031"  # scripted group (container) (typed FeaturePython)
  n = 1
  ref = O_element
FEATURE [App::DocumentObjectGroupPython] G4_MAGNESIUM_OXIDE  # scripted group (container) (typed FeaturePython)
  Dunit = g/cm3
  Dvalue = 3.58
  Group = -> [Mg_element007,O_element060]
  conduct = 2
  density = 1
  expand = 3
  formula = G4_MAGNESIUM_OXIDE
  name = G4_MAGNESIUM_OXIDE
  specific = 4
FEATURE [App::DocumentObjectGroupPython] Mg_element008  label="Mg_element : 004"  # scripted group (container) (typed FeaturePython)
  n = 1
  ref = Mg_element
FEATURE [App::DocumentObjectGroupPython] B_element006  label="B_element : 006"  # scripted group (container) (typed FeaturePython)
  n = 4
  ref = B_element
FEATURE [App::DocumentObjectGroupPython] O_element061  label="O_element : 032"  # scripted group (container) (typed FeaturePython)
  n = 7
  ref = O_element
FEATURE [App::DocumentObjectGroupPython] G4_MAGNESIUM_TETRABORATE  # scripted group (container) (typed FeaturePython)
  Dunit = g/cm3
  Dvalue = 2.53
  Group = -> [Mg_element008,B_element006,O_element061]
  conduct = 2
  density = 1
  expand = 3
  formula = G4_MAGNESIUM_TETRABORATE
  name = G4_MAGNESIUM_TETRABORATE
  specific = 4
FEATURE [App::DocumentObjectGroupPython] Hg_element001  label="Hg_element : 1"  # scripted group (container) (typed FeaturePython)
  n = 1
  ref = Hg_element
FEATURE [App::DocumentObjectGroupPython] I_element004  label="I_element : 2"  # scripted group (container) (typed FeaturePython)
  n = 2
  ref = I_element
FEATURE [App::DocumentObjectGroupPython] G4_MERCURIC_IODIDE  # scripted group (container) (typed FeaturePython)
  Dunit = g/cm3
  Dvalue = 6.36
  Group = -> [Hg_element001,I_element004]
  conduct = 2
  density = 1
  expand = 3
  formula = G4_MERCURIC_IODIDE
  name = G4_MERCURIC_IODIDE
  specific = 4
FEATURE [App::DocumentObjectGroupPython] C_element059  label="C_element : 032"  # scripted group (container) (typed FeaturePython)
  n = 1
  ref = C_element
FEATURE [App::DocumentObjectGroupPython] H_element053  label="H_element : 028"  # scripted group (container) (typed FeaturePython)
  n = 4
  ref = H_element
FEATURE [App::DocumentObjectGroupPython] G4_METHANE  # scripted group (container) (typed FeaturePython)
  Dunit = g/cm3
  Dvalue = 0.000667151
  Group = -> [C_element059,H_element053]
  conduct = 2
  density = 1
  expand = 3
  formula = G4_METHANE
  name = G4_METHANE
  specific = 4
FEATURE [App::DocumentObjectGroupPython] C_element060  label="C_element : 033"  # scripted group (container) (typed FeaturePython)
  n = 1
  ref = C_element
FEATURE [App::DocumentObjectGroupPython] H_element054  label="H_element : 029"  # scripted group (container) (typed FeaturePython)
  n = 4
  ref = H_element
FEATURE [App::DocumentObjectGroupPython] O_element062  label="O_element : 033"  # scripted group (container) (typed FeaturePython)
  n = 1
  ref = O_element
FEATURE [App::DocumentObjectGroupPython] G4_METHANOL  # scripted group (container) (typed FeaturePython)
  Dunit = g/cm3
  Dvalue = 0.7914
  Group = -> [C_element060,H_element054,O_element062]
  conduct = 2
  density = 1
  expand = 3
  formula = G4_METHANOL
  name = G4_METHANOL
  specific = 4
FEATURE [App::DocumentObjectGroupPython] H_element055  label="H_element : 0.134"  # scripted group (container) (typed FeaturePython)
  n = 0.13404
FEATURE [App::DocumentObjectGroupPython] C_element061  label="C_element : 0.778"  # scripted group (container) (typed FeaturePython)
  n = 0.77796
FEATURE [App::DocumentObjectGroupPython] O_element063  label="O_element : 0.035"  # scripted group (container) (typed FeaturePython)
  n = 0.03502
FEATURE [App::DocumentObjectGroupPython] Mg_element009  label="Mg_element : 0.039"  # scripted group (container) (typed FeaturePython)
  n = 0.038594
FEATURE [App::DocumentObjectGroupPython] Ti_element002  label="Ti_element : 0.014"  # scripted group (container) (typed FeaturePython)
  n = 0.014386
FEATURE [App::DocumentObjectGroupPython] G4_MIX_D_WAX  # scripted group (container) (typed FeaturePython)
  Dunit = g/cm3
  Dvalue = 0.99
  Group = -> [H_element055,C_element061,O_element063,Mg_element009,Ti_element002]
  conduct = 2
  density = 1
  expand = 3
  formula = G4_MIX_D_WAX
  name = G4_MIX_D_WAX
  specific = 4
FEATURE [App::DocumentObjectGroupPython] H_element056  label="H_element : 0.135"  # scripted group (container) (typed FeaturePython)
  n = 0.081192
FEATURE [App::DocumentObjectGroupPython] C_element062  label="C_element : 0.583"  # scripted group (container) (typed FeaturePython)
  n = 0.583442
FEATURE [App::DocumentObjectGroupPython] N_element024  label="N_element : 0.018"  # scripted group (container) (typed FeaturePython)
  n = 0.017798
FEATURE [App::DocumentObjectGroupPython] O_element064  label="O_element : 0.186"  # scripted group (container) (typed FeaturePython)
  n = 0.186381
FEATURE [App::DocumentObjectGroupPython] Mg_element010  label="Mg_element : 0.130"  # scripted group (container) (typed FeaturePython)
  n = 0.130287
FEATURE [App::DocumentObjectGroupPython] Cl_element015  label="Cl_element : 0.588"  # scripted group (container) (typed FeaturePython)
  n = 0.0009
FEATURE [App::DocumentObjectGroupPython] G4_MS20_TISSUE  # scripted group (container) (typed FeaturePython)
  Dunit = g/cm3
  Dvalue = 1
  Group = -> [H_element056,C_element062,N_element024,O_element064,Mg_element010,Cl_element015]
  conduct = 2
  density = 1
  expand = 3
  formula = G4_MS20_TISSUE
  name = G4_MS20_TISSUE
  specific = 4
FEATURE [App::DocumentObjectGroupPython] H_element057  label="H_element : 0.136"  # scripted group (container) (typed FeaturePython)
  n = 0.102
FEATURE [App::DocumentObjectGroupPython] C_element063  label="C_element : 0.143"  # scripted group (container) (typed FeaturePython)
  n = 0.143
FEATURE [App::DocumentObjectGroupPython] N_element025  label="N_element : 0.034"  # scripted group (container) (typed FeaturePython)
  n = 0.034
FEATURE [App::DocumentObjectGroupPython] O_element065  label="O_element : 0.710"  # scripted group (container) (typed FeaturePython)
  n = 0.71
FEATURE [App::DocumentObjectGroupPython] Na_element011  label="Na_element : 0.098"  # scripted group (container) (typed FeaturePython)
  n = 0.001
FEATURE [App::DocumentObjectGroupPython] P_element007  label="P_element : 0.002"  # scripted group (container) (typed FeaturePython)
  n = 0.002
FEATURE [App::DocumentObjectGroupPython] S_element017  label="S_element : 0.018"  # scripted group (container) (typed FeaturePython)
  n = 0.003
FEATURE [App::DocumentObjectGroupPython] Cl_element016  label="Cl_element : 0.589"  # scripted group (container) (typed FeaturePython)
  n = 0.001
FEATURE [App::DocumentObjectGroupPython] K_element006  label="K_element : 0.004"  # scripted group (container) (typed FeaturePython)
  n = 0.004
FEATURE [App::DocumentObjectGroupPython] G4_MUSCLE_SKELETAL_ICRP  # scripted group (container) (typed FeaturePython)
  Dunit = g/cm3
  Dvalue = 1.05
  Group = -> [H_element057,C_element063,N_element025,O_element065,Na_element011,P_element007,S_element017,Cl_element016,K_element006]
  conduct = 2
  density = 1
  expand = 3
  formula = G4_MUSCLE_SKELETAL_ICRP
  name = G4_MUSCLE_SKELETAL_ICRP
  specific = 4
FEATURE [App::DocumentObjectGroupPython] H_element058  label="H_element : 0.137"  # scripted group (container) (typed FeaturePython)
  n = 0.102102
FEATURE [App::DocumentObjectGroupPython] C_element064  label="C_element : 0.123"  # scripted group (container) (typed FeaturePython)
  n = 0.123123
FEATURE [App::DocumentObjectGroupPython] N_element026  label="N_element : 0.756"  # scripted group (container) (typed FeaturePython)
  n = 0.035035
FEATURE [App::DocumentObjectGroupPython] O_element066  label="O_element : 0.730"  # scripted group (container) (typed FeaturePython)
  n = 0.72973
FEATURE [App::DocumentObjectGroupPython] Na_element012  label="Na_element : 0.099"  # scripted group (container) (typed FeaturePython)
  n = 0.001001
FEATURE [App::DocumentObjectGroupPython] P_element008  label="P_element : 0.106"  # scripted group (container) (typed FeaturePython)
  n = 0.002002
FEATURE [App::DocumentObjectGroupPython] S_element018  label="S_element : 0.019"  # scripted group (container) (typed FeaturePython)
  n = 0.004004
FEATURE [App::DocumentObjectGroupPython] K_element007  label="K_element : 0.016"  # scripted group (container) (typed FeaturePython)
  n = 0.003003
FEATURE [App::DocumentObjectGroupPython] G4_MUSCLE_STRIATED_ICRU  # scripted group (container) (typed FeaturePython)
  Dunit = g/cm3
  Dvalue = 1.04
  Group = -> [H_element058,C_element064,N_element026,O_element066,Na_element012,P_element008,S_element018,K_element007]
  conduct = 2
  density = 1
  expand = 3
  formula = G4_MUSCLE_STRIATED_ICRU
  name = G4_MUSCLE_STRIATED_ICRU
  specific = 4
FEATURE [App::DocumentObjectGroupPython] H_element059  label="H_element : 0.098"  # scripted group (container) (typed FeaturePython)
  n = 0.0982341
FEATURE [App::DocumentObjectGroupPython] C_element065  label="C_element : 0.156"  # scripted group (container) (typed FeaturePython)
  n = 0.156214
FEATURE [App::DocumentObjectGroupPython] N_element027  label="N_element : 0.757"  # scripted group (container) (typed FeaturePython)
  n = 0.035451
FEATURE [App::DocumentObjectGroupPython] O_element067  label="O_element : 0.880"  # scripted group (container) (typed FeaturePython)
  n = 0.710101
FEATURE [App::DocumentObjectGroupPython] G4_MUSCLE_WITH_SUCROSE  # scripted group (container) (typed FeaturePython)
  Dunit = g/cm3
  Dvalue = 1.11
  Group = -> [H_element059,C_element065,N_element027,O_element067]
  conduct = 2
  density = 1
  expand = 3
  formula = G4_MUSCLE_WITH_SUCROSE
  name = G4_MUSCLE_WITH_SUCROSE
  specific = 4
FEATURE [App::DocumentObjectGroupPython] H_element060  label="H_element : 0.138"  # scripted group (container) (typed FeaturePython)
  n = 0.101969
FEATURE [App::DocumentObjectGroupPython] C_element066  label="C_element : 0.120"  # scripted group (container) (typed FeaturePython)
  n = 0.120058
FEATURE [App::DocumentObjectGroupPython] N_element028  label="N_element : 0.758"  # scripted group (container) (typed FeaturePython)
  n = 0.035451
FEATURE [App::DocumentObjectGroupPython] O_element068  label="O_element : 0.743"  # scripted group (container) (typed FeaturePython)
  n = 0.742522
FEATURE [App::DocumentObjectGroupPython] G4_MUSCLE_WITHOUT_SUCROSE  # scripted group (container) (typed FeaturePython)
  Dunit = g/cm3
  Dvalue = 1.07
  Group = -> [H_element060,C_element066,N_element028,O_element068]
  conduct = 2
  density = 1
  expand = 3
  formula = G4_MUSCLE_WITHOUT_SUCROSE
  name = G4_MUSCLE_WITHOUT_SUCROSE
  specific = 4
FEATURE [App::DocumentObjectGroupPython] C_element067  label="C_element : 10"  # scripted group (container) (typed FeaturePython)
  n = 10
  ref = C_element
FEATURE [App::DocumentObjectGroupPython] H_element061  label="H_element : 030"  # scripted group (container) (typed FeaturePython)
  n = 8
  ref = H_element
FEATURE [App::DocumentObjectGroupPython] G4_NAPHTHALENE  # scripted group (container) (typed FeaturePython)
  Dunit = g/cm3
  Dvalue = 1.145
  Group = -> [C_element067,H_element061]
  conduct = 2
  density = 1
  expand = 3
  formula = G4_NAPHTHALENE
  name = G4_NAPHTHALENE
  specific = 4
FEATURE [App::DocumentObjectGroupPython] C_element068  label="C_element : 034"  # scripted group (container) (typed FeaturePython)
  n = 6
  ref = C_element
FEATURE [App::DocumentObjectGroupPython] H_element062  label="H_element : 031"  # scripted group (container) (typed FeaturePython)
  n = 5
  ref = H_element
FEATURE [App::DocumentObjectGroupPython] N_element029  label="N_element : 012"  # scripted group (container) (typed FeaturePython)
  n = 1
  ref = N_element
FEATURE [App::DocumentObjectGroupPython] O_element069  label="O_element : 034"  # scripted group (container) (typed FeaturePython)
  n = 2
  ref = O_element
FEATURE [App::DocumentObjectGroupPython] G4_NITROBENZENE  # scripted group (container) (typed FeaturePython)
  Dunit = g/cm3
  Dvalue = 1.19867
  Group = -> [C_element068,H_element062,N_element029,O_element069]
  conduct = 2
  density = 1
  expand = 3
  formula = G4_NITROBENZENE
  name = G4_NITROBENZENE
  specific = 4
FEATURE [App::DocumentObjectGroupPython] N_element030  label="N_element : 013"  # scripted group (container) (typed FeaturePython)
  n = 2
  ref = N_element
FEATURE [App::DocumentObjectGroupPython] O_element070  label="O_element : 035"  # scripted group (container) (typed FeaturePython)
  n = 1
  ref = O_element
FEATURE [App::DocumentObjectGroupPython] G4_NITROUS_OXIDE  # scripted group (container) (typed FeaturePython)
  Dunit = g/cm3
  Dvalue = 0.00183094
  Group = -> [N_element030,O_element070]
  conduct = 2
  density = 1
  expand = 3
  formula = G4_NITROUS_OXIDE
  name = G4_NITROUS_OXIDE
  specific = 4
FEATURE [App::DocumentObjectGroupPython] H_element063  label="H_element : 0.104"  # scripted group (container) (typed FeaturePython)
  n = 0.103509
FEATURE [App::DocumentObjectGroupPython] C_element069  label="C_element : 0.648"  # scripted group (container) (typed FeaturePython)
  n = 0.648416
FEATURE [App::DocumentObjectGroupPython] N_element031  label="N_element : 0.100"  # scripted group (container) (typed FeaturePython)
  n = 0.0995361
FEATURE [App::DocumentObjectGroupPython] O_element071  label="O_element : 0.149"  # scripted group (container) (typed FeaturePython)
  n = 0.148539
FEATURE [App::DocumentObjectGroupPython] G4_NYLON_8062  label="G4_NYLON-8062"  # scripted group (container) (typed FeaturePython)
  Dunit = g/cm3
  Dvalue = 1.08
  Group = -> [H_element063,C_element069,N_element031,O_element071]
  conduct = 2
  density = 1
  expand = 3
  formula = G4_NYLON-8062
  name = G4_NYLON-8062
  specific = 4
FEATURE [App::DocumentObjectGroupPython] C_element070  label="C_element : 035"  # scripted group (container) (typed FeaturePython)
  n = 6
  ref = C_element
FEATURE [App::DocumentObjectGroupPython] H_element064  label="H_element : 11"  # scripted group (container) (typed FeaturePython)
  n = 11
  ref = H_element
FEATURE [App::DocumentObjectGroupPython] N_element032  label="N_element : 014"  # scripted group (container) (typed FeaturePython)
  n = 1
  ref = N_element
FEATURE [App::DocumentObjectGroupPython] O_element072  label="O_element : 036"  # scripted group (container) (typed FeaturePython)
  n = 1
  ref = O_element
FEATURE [App::DocumentObjectGroupPython] G4_NYLON_6_6  label="G4_NYLON-6-6"  # scripted group (container) (typed FeaturePython)
  Dunit = g/cm3
  Dvalue = 1.14
  Group = -> [C_element070,H_element064,N_element032,O_element072]
  conduct = 2
  density = 1
  expand = 3
  formula = G4_NYLON-6-6
  name = G4_NYLON-6-6
  specific = 4
FEATURE [App::DocumentObjectGroupPython] H_element065  label="H_element : 0.139"  # scripted group (container) (typed FeaturePython)
  n = 0.107062
FEATURE [App::DocumentObjectGroupPython] C_element071  label="C_element : 0.680"  # scripted group (container) (typed FeaturePython)
  n = 0.680449
FEATURE [App::DocumentObjectGroupPython] N_element033  label="N_element : 0.099"  # scripted group (container) (typed FeaturePython)
  n = 0.099189
FEATURE [App::DocumentObjectGroupPython] O_element073  label="O_element : 0.113"  # scripted group (container) (typed FeaturePython)
  n = 0.1133
FEATURE [App::DocumentObjectGroupPython] G4_NYLON_6_10  label="G4_NYLON-6-10"  # scripted group (container) (typed FeaturePython)
  Dunit = g/cm3
  Dvalue = 1.14
  Group = -> [H_element065,C_element071,N_element033,O_element073]
  conduct = 2
  density = 1
  expand = 3
  formula = G4_NYLON-6-10
  name = G4_NYLON-6-10
  specific = 4
FEATURE [App::DocumentObjectGroupPython] H_element066  label="H_element : 0.140"  # scripted group (container) (typed FeaturePython)
  n = 0.115476
FEATURE [App::DocumentObjectGroupPython] C_element072  label="C_element : 0.721"  # scripted group (container) (typed FeaturePython)
  n = 0.720818
FEATURE [App::DocumentObjectGroupPython] N_element034  label="N_element : 0.076"  # scripted group (container) (typed FeaturePython)
  n = 0.0764169
FEATURE [App::DocumentObjectGroupPython] O_element074  label="O_element : 0.087"  # scripted group (container) (typed FeaturePython)
  n = 0.0872889
FEATURE [App::DocumentObjectGroupPython] G4_NYLON_11_RILSAN  label="G4_NYLON-11_RILSAN"  # scripted group (container) (typed FeaturePython)
  Dunit = g/cm3
  Dvalue = 1.425
  Group = -> [H_element066,C_element072,N_element034,O_element074]
  conduct = 2
  density = 1
  expand = 3
  formula = G4_NYLON-11_RILSAN
  name = G4_NYLON-11_RILSAN
  specific = 4
FEATURE [App::DocumentObjectGroupPython] C_element073  label="C_element : 8"  # scripted group (container) (typed FeaturePython)
  n = 8
  ref = C_element
FEATURE [App::DocumentObjectGroupPython] H_element067  label="H_element : 18"  # scripted group (container) (typed FeaturePython)
  n = 18
  ref = H_element
FEATURE [App::DocumentObjectGroupPython] G4_OCTANE  # scripted group (container) (typed FeaturePython)
  Dunit = g/cm3
  Dvalue = 0.7026
  Group = -> [C_element073,H_element067]
  conduct = 2
  density = 1
  expand = 3
  formula = G4_OCTANE
  name = G4_OCTANE
  specific = 4
FEATURE [App::DocumentObjectGroupPython] C_element074  label="C_element : 25"  # scripted group (container) (typed FeaturePython)
  n = 25
  ref = C_element
FEATURE [App::DocumentObjectGroupPython] H_element068  label="H_element : 52"  # scripted group (container) (typed FeaturePython)
  n = 52
  ref = H_element
FEATURE [App::DocumentObjectGroupPython] G4_PARAFFIN  # scripted group (container) (typed FeaturePython)
  Dunit = g/cm3
  Dvalue = 0.93
  Group = -> [C_element074,H_element068]
  conduct = 2
  density = 1
  expand = 3
  formula = G4_PARAFFIN
  name = G4_PARAFFIN
  specific = 4
FEATURE [App::DocumentObjectGroupPython] C_element075  label="C_element : 036"  # scripted group (container) (typed FeaturePython)
  n = 5
  ref = C_element
FEATURE [App::DocumentObjectGroupPython] H_element069  label="H_element : 032"  # scripted group (container) (typed FeaturePython)
  n = 12
  ref = H_element
FEATURE [App::DocumentObjectGroupPython] G4_N_PENTANE  label="G4_N-PENTANE"  # scripted group (container) (typed FeaturePython)
  Dunit = g/cm3
  Dvalue = 0.6262
  Group = -> [C_element075,H_element069]
  conduct = 2
  density = 1
  expand = 3
  formula = G4_N-PENTANE
  name = G4_N-PENTANE
  specific = 4
FEATURE [App::DocumentObjectGroupPython] H_element070  label="H_element : 0.014"  # scripted group (container) (typed FeaturePython)
  n = 0.0141
FEATURE [App::DocumentObjectGroupPython] C_element076  label="C_element : 0.072"  # scripted group (container) (typed FeaturePython)
  n = 0.072261
FEATURE [App::DocumentObjectGroupPython] N_element035  label="N_element : 0.019"  # scripted group (container) (typed FeaturePython)
  n = 0.01932
FEATURE [App::DocumentObjectGroupPython] O_element075  label="O_element : 0.066"  # scripted group (container) (typed FeaturePython)
  n = 0.066101
FEATURE [App::DocumentObjectGroupPython] S_element019  label="S_element : 0.020"  # scripted group (container) (typed FeaturePython)
  n = 0.00189
FEATURE [App::DocumentObjectGroupPython] Br_element004  label="Br_element : 0.349"  # scripted group (container) (typed FeaturePython)
  n = 0.349103
FEATURE [App::DocumentObjectGroupPython] Ag_element001  label="Ag_element : 0.474"  # scripted group (container) (typed FeaturePython)
  n = 0.474105
FEATURE [App::DocumentObjectGroupPython] I_element005  label="I_element : 0.003"  # scripted group (container) (typed FeaturePython)
  n = 0.00312
FEATURE [App::DocumentObjectGroupPython] G4_PHOTO_EMULSION  # scripted group (container) (typed FeaturePython)
  Dunit = g/cm3
  Dvalue = 3.815
  Group = -> [H_element070,C_element076,N_element035,O_element075,S_element019,Br_element004,Ag_element001,I_element005]
  conduct = 2
  density = 1
  expand = 3
  formula = G4_PHOTO_EMULSION
  name = G4_PHOTO_EMULSION
  specific = 4
FEATURE [App::DocumentObjectGroupPython] C_element077  label="C_element : 9"  # scripted group (container) (typed FeaturePython)
  n = 9
  ref = C_element
FEATURE [App::DocumentObjectGroupPython] H_element071  label="H_element : 033"  # scripted group (container) (typed FeaturePython)
  n = 10
  ref = H_element
FEATURE [App::DocumentObjectGroupPython] G4_PLASTIC_SC_VINYLTOLUENE  # scripted group (container) (typed FeaturePython)
  Dunit = g/cm3
  Dvalue = 1.032
  Group = -> [C_element077,H_element071]
  conduct = 2
  density = 1
  expand = 3
  formula = G4_PLASTIC_SC_VINYLTOLUENE
  name = G4_PLASTIC_SC_VINYLTOLUENE
  specific = 4
FEATURE [App::DocumentObjectGroupPython] Pu_element001  label="Pu_element : 1"  # scripted group (container) (typed FeaturePython)
  n = 1
  ref = Pu_element
FEATURE [App::DocumentObjectGroupPython] O_element076  label="O_element : 037"  # scripted group (container) (typed FeaturePython)
  n = 2
  ref = O_element
FEATURE [App::DocumentObjectGroupPython] G4_PLUTONIUM_DIOXIDE  # scripted group (container) (typed FeaturePython)
  Dunit = g/cm3
  Dvalue = 11.46
  Group = -> [Pu_element001,O_element076]
  conduct = 2
  density = 1
  expand = 3
  formula = G4_PLUTONIUM_DIOXIDE
  name = G4_PLUTONIUM_DIOXIDE
  specific = 4
FEATURE [App::DocumentObjectGroupPython] C_element078  label="C_element : 037"  # scripted group (container) (typed FeaturePython)
  n = 3
  ref = C_element
FEATURE [App::DocumentObjectGroupPython] H_element072  label="H_element : 034"  # scripted group (container) (typed FeaturePython)
  n = 3
  ref = H_element
FEATURE [App::DocumentObjectGroupPython] N_element036  label="N_element : 015"  # scripted group (container) (typed FeaturePython)
  n = 1
  ref = N_element
FEATURE [App::DocumentObjectGroupPython] G4_POLYACRYLONITRILE  # scripted group (container) (typed FeaturePython)
  Dunit = g/cm3
  Dvalue = 1.17
  Group = -> [C_element078,H_element072,N_element036]
  conduct = 2
  density = 1
  expand = 3
  formula = G4_POLYACRYLONITRILE
  name = G4_POLYACRYLONITRILE
  specific = 4
FEATURE [App::DocumentObjectGroupPython] C_element079  label="C_element : 16"  # scripted group (container) (typed FeaturePython)
  n = 16
  ref = C_element
FEATURE [App::DocumentObjectGroupPython] H_element073  label="H_element : 035"  # scripted group (container) (typed FeaturePython)
  n = 14
  ref = H_element
FEATURE [App::DocumentObjectGroupPython] O_element077  label="O_element : 038"  # scripted group (container) (typed FeaturePython)
  n = 3
  ref = O_element
FEATURE [App::DocumentObjectGroupPython] G4_POLYCARBONATE  # scripted group (container) (typed FeaturePython)
  Dunit = g/cm3
  Dvalue = 1.2
  Group = -> [C_element079,H_element073,O_element077]
  conduct = 2
  density = 1
  expand = 3
  formula = G4_POLYCARBONATE
  name = G4_POLYCARBONATE
  specific = 4
FEATURE [App::DocumentObjectGroupPython] C_element080  label="C_element : 038"  # scripted group (container) (typed FeaturePython)
  n = 8
  ref = C_element
FEATURE [App::DocumentObjectGroupPython] H_element074  label="H_element : 036"  # scripted group (container) (typed FeaturePython)
  n = 7
  ref = H_element
FEATURE [App::DocumentObjectGroupPython] Cl_element017  label="Cl_element : 007"  # scripted group (container) (typed FeaturePython)
  n = 1
  ref = Cl_element
FEATURE [App::DocumentObjectGroupPython] G4_POLYCHLOROSTYRENE  # scripted group (container) (typed FeaturePython)
  Dunit = g/cm3
  Dvalue = 1.3
  Group = -> [C_element080,H_element074,Cl_element017]
  conduct = 2
  density = 1
  expand = 3
  formula = G4_POLYCHLOROSTYRENE
  name = G4_POLYCHLOROSTYRENE
  specific = 4
FEATURE [App::DocumentObjectGroupPython] C_element081  label="C_element : 039"  # scripted group (container) (typed FeaturePython)
  n = 1
  ref = C_element
FEATURE [App::DocumentObjectGroupPython] H_element075  label="H_element : 037"  # scripted group (container) (typed FeaturePython)
  n = 2
  ref = H_element
FEATURE [App::DocumentObjectGroupPython] G4_POLYETHYLENE  # scripted group (container) (typed FeaturePython)
  Dunit = g/cm3
  Dvalue = 0.94
  Group = -> [C_element081,H_element075]
  conduct = 2
  density = 1
  expand = 3
  formula = G4_POLYETHYLENE
  name = G4_POLYETHYLENE
  specific = 4
FEATURE [App::DocumentObjectGroupPython] C_element082  label="C_element : 040"  # scripted group (container) (typed FeaturePython)
  n = 10
  ref = C_element
FEATURE [App::DocumentObjectGroupPython] H_element076  label="H_element : 038"  # scripted group (container) (typed FeaturePython)
  n = 8
  ref = H_element
FEATURE [App::DocumentObjectGroupPython] O_element078  label="O_element : 039"  # scripted group (container) (typed FeaturePython)
  n = 4
  ref = O_element
FEATURE [App::DocumentObjectGroupPython] G4_MYLAR  # scripted group (container) (typed FeaturePython)
  Dunit = g/cm3
  Dvalue = 1.4
  Group = -> [C_element082,H_element076,O_element078]
  conduct = 2
  density = 1
  expand = 3
  formula = G4_MYLAR
  name = G4_MYLAR
  specific = 4
FEATURE [App::DocumentObjectGroupPython] C_element083  label="C_element : 041"  # scripted group (container) (typed FeaturePython)
  n = 5
  ref = C_element
FEATURE [App::DocumentObjectGroupPython] H_element077  label="H_element : 039"  # scripted group (container) (typed FeaturePython)
  n = 8
  ref = H_element
FEATURE [App::DocumentObjectGroupPython] O_element079  label="O_element : 040"  # scripted group (container) (typed FeaturePython)
  n = 2
  ref = O_element
FEATURE [App::DocumentObjectGroupPython] G4_PLEXIGLASS  # scripted group (container) (typed FeaturePython)
  Dunit = g/cm3
  Dvalue = 1.19
  Group = -> [C_element083,H_element077,O_element079]
  conduct = 2
  density = 1
  expand = 3
  formula = G4_PLEXIGLASS
  name = G4_PLEXIGLASS
  specific = 4
FEATURE [App::DocumentObjectGroupPython] C_element084  label="C_element : 042"  # scripted group (container) (typed FeaturePython)
  n = 1
  ref = C_element
FEATURE [App::DocumentObjectGroupPython] H_element078  label="H_element : 040"  # scripted group (container) (typed FeaturePython)
  n = 2
  ref = H_element
FEATURE [App::DocumentObjectGroupPython] O_element080  label="O_element : 041"  # scripted group (container) (typed FeaturePython)
  n = 1
  ref = O_element
FEATURE [App::DocumentObjectGroupPython] G4_POLYOXYMETHYLENE  # scripted group (container) (typed FeaturePython)
  Dunit = g/cm3
  Dvalue = 1.425
  Group = -> [C_element084,H_element078,O_element080]
  conduct = 2
  density = 1
  expand = 3
  formula = G4_POLYOXYMETHYLENE
  name = G4_POLYOXYMETHYLENE
  specific = 4
FEATURE [App::DocumentObjectGroupPython] C_element085  label="C_element : 043"  # scripted group (container) (typed FeaturePython)
  n = 2
  ref = C_element
FEATURE [App::DocumentObjectGroupPython] H_element079  label="H_element : 041"  # scripted group (container) (typed FeaturePython)
  n = 4
  ref = H_element
FEATURE [App::DocumentObjectGroupPython] G4_POLYPROPYLENE  # scripted group (container) (typed FeaturePython)
  Dunit = g/cm3
  Dvalue = 0.9
  Group = -> [C_element085,H_element079]
  conduct = 2
  density = 1
  expand = 3
  formula = G4_POLYPROPYLENE
  name = G4_POLYPROPYLENE
  specific = 4
FEATURE [App::DocumentObjectGroupPython] C_element086  label="C_element : 044"  # scripted group (container) (typed FeaturePython)
  n = 8
  ref = C_element
FEATURE [App::DocumentObjectGroupPython] H_element080  label="H_element : 042"  # scripted group (container) (typed FeaturePython)
  n = 8
  ref = H_element
FEATURE [App::DocumentObjectGroupPython] G4_POLYSTYRENE  # scripted group (container) (typed FeaturePython)
  Dunit = g/cm3
  Dvalue = 1.06
  Group = -> [C_element086,H_element080]
  conduct = 2
  density = 1
  expand = 3
  formula = G4_POLYSTYRENE
  name = G4_POLYSTYRENE
  specific = 4
FEATURE [App::DocumentObjectGroupPython] C_element087  label="C_element : 045"  # scripted group (container) (typed FeaturePython)
  n = 2
  ref = C_element
FEATURE [App::DocumentObjectGroupPython] F_element014  label="F_element : 4"  # scripted group (container) (typed FeaturePython)
  n = 4
  ref = F_element
FEATURE [App::DocumentObjectGroupPython] G4_TEFLON  # scripted group (container) (typed FeaturePython)
  Dunit = g/cm3
  Dvalue = 2.2
  Group = -> [C_element087,F_element014]
  conduct = 2
  density = 1
  expand = 3
  formula = G4_TEFLON
  name = G4_TEFLON
  specific = 4
FEATURE [App::DocumentObjectGroupPython] C_element088  label="C_element : 046"  # scripted group (container) (typed FeaturePython)
  n = 2
  ref = C_element
FEATURE [App::DocumentObjectGroupPython] F_element015  label="F_element : 006"  # scripted group (container) (typed FeaturePython)
  n = 3
  ref = F_element
FEATURE [App::DocumentObjectGroupPython] Cl_element018  label="Cl_element : 008"  # scripted group (container) (typed FeaturePython)
  n = 1
  ref = Cl_element
FEATURE [App::DocumentObjectGroupPython] G4_POLYTRIFLUOROCHLOROETHYLENE  # scripted group (container) (typed FeaturePython)
  Dunit = g/cm3
  Dvalue = 2.1
  Group = -> [C_element088,F_element015,Cl_element018]
  conduct = 2
  density = 1
  expand = 3
  formula = G4_POLYTRIFLUOROCHLOROETHYLENE
  name = G4_POLYTRIFLUOROCHLOROETHYLENE
  specific = 4
FEATURE [App::DocumentObjectGroupPython] C_element089  label="C_element : 047"  # scripted group (container) (typed FeaturePython)
  n = 4
  ref = C_element
FEATURE [App::DocumentObjectGroupPython] H_element081  label="H_element : 043"  # scripted group (container) (typed FeaturePython)
  n = 6
  ref = H_element
FEATURE [App::DocumentObjectGroupPython] O_element081  label="O_element : 042"  # scripted group (container) (typed FeaturePython)
  n = 2
  ref = O_element
FEATURE [App::DocumentObjectGroupPython] G4_POLYVINYL_ACETATE  # scripted group (container) (typed FeaturePython)
  Dunit = g/cm3
  Dvalue = 1.19
  Group = -> [C_element089,H_element081,O_element081]
  conduct = 2
  density = 1
  expand = 3
  formula = G4_POLYVINYL_ACETATE
  name = G4_POLYVINYL_ACETATE
  specific = 4
FEATURE [App::DocumentObjectGroupPython] C_element090  label="C_element : 048"  # scripted group (container) (typed FeaturePython)
  n = 2
  ref = C_element
FEATURE [App::DocumentObjectGroupPython] H_element082  label="H_element : 044"  # scripted group (container) (typed FeaturePython)
  n = 4
  ref = H_element
FEATURE [App::DocumentObjectGroupPython] O_element082  label="O_element : 043"  # scripted group (container) (typed FeaturePython)
  n = 1
  ref = O_element
FEATURE [App::DocumentObjectGroupPython] G4_POLYVINYL_ALCOHOL  # scripted group (container) (typed FeaturePython)
  Dunit = g/cm3
  Dvalue = 1.3
  Group = -> [C_element090,H_element082,O_element082]
  conduct = 2
  density = 1
  expand = 3
  formula = G4_POLYVINYL_ALCOHOL
  name = G4_POLYVINYL_ALCOHOL
  specific = 4
FEATURE [App::DocumentObjectGroupPython] C_element091  label="C_element : 049"  # scripted group (container) (typed FeaturePython)
  n = 8
  ref = C_element
FEATURE [App::DocumentObjectGroupPython] H_element083  label="H_element : 045"  # scripted group (container) (typed FeaturePython)
  n = 14
  ref = H_element
FEATURE [App::DocumentObjectGroupPython] O_element083  label="O_element : 044"  # scripted group (container) (typed FeaturePython)
  n = 2
  ref = O_element
FEATURE [App::DocumentObjectGroupPython] G4_POLYVINYL_BUTYRAL  # scripted group (container) (typed FeaturePython)
  Dunit = g/cm3
  Dvalue = 1.12
  Group = -> [C_element091,H_element083,O_element083]
  conduct = 2
  density = 1
  expand = 3
  formula = G4_POLYVINYL_BUTYRAL
  name = G4_POLYVINYL_BUTYRAL
  specific = 4
FEATURE [App::DocumentObjectGroupPython] C_element092  label="C_element : 050"  # scripted group (container) (typed FeaturePython)
  n = 2
  ref = C_element
FEATURE [App::DocumentObjectGroupPython] H_element084  label="H_element : 046"  # scripted group (container) (typed FeaturePython)
  n = 3
  ref = H_element
FEATURE [App::DocumentObjectGroupPython] Cl_element019  label="Cl_element : 009"  # scripted group (container) (typed FeaturePython)
  n = 1
  ref = Cl_element
FEATURE [App::DocumentObjectGroupPython] G4_POLYVINYL_CHLORIDE  # scripted group (container) (typed FeaturePython)
  Dunit = g/cm3
  Dvalue = 1.3
  Group = -> [C_element092,H_element084,Cl_element019]
  conduct = 2
  density = 1
  expand = 3
  formula = G4_POLYVINYL_CHLORIDE
  name = G4_POLYVINYL_CHLORIDE
  specific = 4
FEATURE [App::DocumentObjectGroupPython] C_element093  label="C_element : 051"  # scripted group (container) (typed FeaturePython)
  n = 2
  ref = C_element
FEATURE [App::DocumentObjectGroupPython] H_element085  label="H_element : 047"  # scripted group (container) (typed FeaturePython)
  n = 2
  ref = H_element
FEATURE [App::DocumentObjectGroupPython] Cl_element020  label="Cl_element : 010"  # scripted group (container) (typed FeaturePython)
  n = 2
  ref = Cl_element
FEATURE [App::DocumentObjectGroupPython] G4_POLYVINYLIDENE_CHLORIDE  # scripted group (container) (typed FeaturePython)
  Dunit = g/cm3
  Dvalue = 1.7
  Group = -> [C_element093,H_element085,Cl_element020]
  conduct = 2
  density = 1
  expand = 3
  formula = G4_POLYVINYLIDENE_CHLORIDE
  name = G4_POLYVINYLIDENE_CHLORIDE
  specific = 4
FEATURE [App::DocumentObjectGroupPython] C_element094  label="C_element : 052"  # scripted group (container) (typed FeaturePython)
  n = 2
  ref = C_element
FEATURE [App::DocumentObjectGroupPython] H_element086  label="H_element : 048"  # scripted group (container) (typed FeaturePython)
  n = 2
  ref = H_element
FEATURE [App::DocumentObjectGroupPython] F_element016  label="F_element : 007"  # scripted group (container) (typed FeaturePython)
  n = 2
  ref = F_element
FEATURE [App::DocumentObjectGroupPython] G4_POLYVINYLIDENE_FLUORIDE  # scripted group (container) (typed FeaturePython)
  Dunit = g/cm3
  Dvalue = 1.76
  Group = -> [C_element094,H_element086,F_element016]
  conduct = 2
  density = 1
  expand = 3
  formula = G4_POLYVINYLIDENE_FLUORIDE
  name = G4_POLYVINYLIDENE_FLUORIDE
  specific = 4
FEATURE [App::DocumentObjectGroupPython] C_element095  label="C_element : 053"  # scripted group (container) (typed FeaturePython)
  n = 6
  ref = C_element
FEATURE [App::DocumentObjectGroupPython] H_element087  label="H_element : 9"  # scripted group (container) (typed FeaturePython)
  n = 9
  ref = H_element
FEATURE [App::DocumentObjectGroupPython] N_element037  label="N_element : 016"  # scripted group (container) (typed FeaturePython)
  n = 1
  ref = N_element
FEATURE [App::DocumentObjectGroupPython] O_element084  label="O_element : 045"  # scripted group (container) (typed FeaturePython)
  n = 1
  ref = O_element
FEATURE [App::DocumentObjectGroupPython] G4_POLYVINYL_PYRROLIDONE  # scripted group (container) (typed FeaturePython)
  Dunit = g/cm3
  Dvalue = 1.25
  Group = -> [C_element095,H_element087,N_element037,O_element084]
  conduct = 2
  density = 1
  expand = 3
  formula = G4_POLYVINYL_PYRROLIDONE
  name = G4_POLYVINYL_PYRROLIDONE
  specific = 4
FEATURE [App::DocumentObjectGroupPython] K_element008  label="K_element : 1"  # scripted group (container) (typed FeaturePython)
  n = 1
  ref = K_element
FEATURE [App::DocumentObjectGroupPython] I_element006  label="I_element : 003"  # scripted group (container) (typed FeaturePython)
  n = 1
  ref = I_element
FEATURE [App::DocumentObjectGroupPython] G4_POTASSIUM_IODIDE  # scripted group (container) (typed FeaturePython)
  Dunit = g/cm3
  Dvalue = 3.13
  Group = -> [K_element008,I_element006]
  conduct = 2
  density = 1
  expand = 3
  formula = G4_POTASSIUM_IODIDE
  name = G4_POTASSIUM_IODIDE
  specific = 4
FEATURE [App::DocumentObjectGroupPython] K_element009  label="K_element : 2"  # scripted group (container) (typed FeaturePython)
  n = 2
  ref = K_element
FEATURE [App::DocumentObjectGroupPython] O_element085  label="O_element : 046"  # scripted group (container) (typed FeaturePython)
  n = 1
  ref = O_element
FEATURE [App::DocumentObjectGroupPython] G4_POTASSIUM_OXIDE  # scripted group (container) (typed FeaturePython)
  Dunit = g/cm3
  Dvalue = 2.32
  Group = -> [K_element009,O_element085]
  conduct = 2
  density = 1
  expand = 3
  formula = G4_POTASSIUM_OXIDE
  name = G4_POTASSIUM_OXIDE
  specific = 4
FEATURE [App::DocumentObjectGroupPython] C_element096  label="C_element : 054"  # scripted group (container) (typed FeaturePython)
  n = 3
  ref = C_element
FEATURE [App::DocumentObjectGroupPython] H_element088  label="H_element : 049"  # scripted group (container) (typed FeaturePython)
  n = 8
  ref = H_element
FEATURE [App::DocumentObjectGroupPython] G4_PROPANE  # scripted group (container) (typed FeaturePython)
  Dunit = g/cm3
  Dvalue = 0.00187939
  Group = -> [C_element096,H_element088]
  conduct = 2
  density = 1
  expand = 3
  formula = G4_PROPANE
  name = G4_PROPANE
  specific = 4
FEATURE [App::DocumentObjectGroupPython] C_element097  label="C_element : 055"  # scripted group (container) (typed FeaturePython)
  n = 3
  ref = C_element
FEATURE [App::DocumentObjectGroupPython] H_element089  label="H_element : 050"  # scripted group (container) (typed FeaturePython)
  n = 8
  ref = H_element
FEATURE [App::DocumentObjectGroupPython] G4_lPROPANE  # scripted group (container) (typed FeaturePython)
  Dunit = g/cm3
  Dvalue = 0.43
  Group = -> [C_element097,H_element089]
  conduct = 2
  density = 1
  expand = 3
  formula = G4_lPROPANE
  name = G4_lPROPANE
  specific = 4
FEATURE [App::DocumentObjectGroupPython] C_element098  label="C_element : 056"  # scripted group (container) (typed FeaturePython)
  n = 3
  ref = C_element
FEATURE [App::DocumentObjectGroupPython] H_element090  label="H_element : 051"  # scripted group (container) (typed FeaturePython)
  n = 8
  ref = H_element
FEATURE [App::DocumentObjectGroupPython] O_element086  label="O_element : 047"  # scripted group (container) (typed FeaturePython)
  n = 1
  ref = O_element
FEATURE [App::DocumentObjectGroupPython] G4_N_PROPYL_ALCOHOL  label="G4_N-PROPYL_ALCOHOL"  # scripted group (container) (typed FeaturePython)
  Dunit = g/cm3
  Dvalue = 0.8035
  Group = -> [C_element098,H_element090,O_element086]
  conduct = 2
  density = 1
  expand = 3
  formula = G4_N-PROPYL_ALCOHOL
  name = G4_N-PROPYL_ALCOHOL
  specific = 4
FEATURE [App::DocumentObjectGroupPython] C_element099  label="C_element : 057"  # scripted group (container) (typed FeaturePython)
  n = 5
  ref = C_element
FEATURE [App::DocumentObjectGroupPython] H_element091  label="H_element : 052"  # scripted group (container) (typed FeaturePython)
  n = 5
  ref = H_element
FEATURE [App::DocumentObjectGroupPython] N_element038  label="N_element : 017"  # scripted group (container) (typed FeaturePython)
  n = 1
  ref = N_element
FEATURE [App::DocumentObjectGroupPython] G4_PYRIDINE  # scripted group (container) (typed FeaturePython)
  Dunit = g/cm3
  Dvalue = 0.9819
  Group = -> [C_element099,H_element091,N_element038]
  conduct = 2
  density = 1
  expand = 3
  formula = G4_PYRIDINE
  name = G4_PYRIDINE
  specific = 4
FEATURE [App::DocumentObjectGroupPython] H_element092  label="H_element : 0.144"  # scripted group (container) (typed FeaturePython)
  n = 0.143711
FEATURE [App::DocumentObjectGroupPython] C_element100  label="C_element : 0.856"  # scripted group (container) (typed FeaturePython)
  n = 0.856289
FEATURE [App::DocumentObjectGroupPython] G4_RUBBER_BUTYL  # scripted group (container) (typed FeaturePython)
  Dunit = g/cm3
  Dvalue = 0.92
  Group = -> [H_element092,C_element100]
  conduct = 2
  density = 1
  expand = 3
  formula = G4_RUBBER_BUTYL
  name = G4_RUBBER_BUTYL
  specific = 4
FEATURE [App::DocumentObjectGroupPython] H_element093  label="H_element : 0.118"  # scripted group (container) (typed FeaturePython)
  n = 0.118371
FEATURE [App::DocumentObjectGroupPython] C_element101  label="C_element : 0.882"  # scripted group (container) (typed FeaturePython)
  n = 0.881629
FEATURE [App::DocumentObjectGroupPython] G4_RUBBER_NATURAL  # scripted group (container) (typed FeaturePython)
  Dunit = g/cm3
  Dvalue = 0.92
  Group = -> [H_element093,C_element101]
  conduct = 2
  density = 1
  expand = 3
  formula = G4_RUBBER_NATURAL
  name = G4_RUBBER_NATURAL
  specific = 4
FEATURE [App::DocumentObjectGroupPython] H_element094  label="H_element : 0.145"  # scripted group (container) (typed FeaturePython)
  n = 0.05692
FEATURE [App::DocumentObjectGroupPython] C_element102  label="C_element : 0.543"  # scripted group (container) (typed FeaturePython)
  n = 0.542646
FEATURE [App::DocumentObjectGroupPython] Cl_element021  label="Cl_element : 0.400"  # scripted group (container) (typed FeaturePython)
  n = 0.400434
FEATURE [App::DocumentObjectGroupPython] G4_RUBBER_NEOPRENE  # scripted group (container) (typed FeaturePython)
  Dunit = g/cm3
  Dvalue = 1.23
  Group = -> [H_element094,C_element102,Cl_element021]
  conduct = 2
  density = 1
  expand = 3
  formula = G4_RUBBER_NEOPRENE
  name = G4_RUBBER_NEOPRENE
  specific = 4
FEATURE [App::DocumentObjectGroupPython] Si_element006  label="Si_element : 1"  # scripted group (container) (typed FeaturePython)
  n = 1
  ref = Si_element
FEATURE [App::DocumentObjectGroupPython] O_element087  label="O_element : 048"  # scripted group (container) (typed FeaturePython)
  n = 2
  ref = O_element
FEATURE [App::DocumentObjectGroupPython] G4_SILICON_DIOXIDE  # scripted group (container) (typed FeaturePython)
  Dunit = g/cm3
  Dvalue = 2.32
  Group = -> [Si_element006,O_element087]
  conduct = 2
  density = 1
  expand = 3
  formula = G4_SILICON_DIOXIDE
  name = G4_SILICON_DIOXIDE
  specific = 4
FEATURE [App::DocumentObjectGroupPython] Ag_element002  label="Ag_element : 1"  # scripted group (container) (typed FeaturePython)
  n = 1
  ref = Ag_element
FEATURE [App::DocumentObjectGroupPython] Br_element005  label="Br_element : 003"  # scripted group (container) (typed FeaturePython)
  n = 1
  ref = Br_element
FEATURE [App::DocumentObjectGroupPython] G4_SILVER_BROMIDE  # scripted group (container) (typed FeaturePython)
  Dunit = g/cm3
  Dvalue = 6.473
  Group = -> [Ag_element002,Br_element005]
  conduct = 2
  density = 1
  expand = 3
  formula = G4_SILVER_BROMIDE
  name = G4_SILVER_BROMIDE
  specific = 4
FEATURE [App::DocumentObjectGroupPython] Ag_element003  label="Ag_element : 002"  # scripted group (container) (typed FeaturePython)
  n = 1
  ref = Ag_element
FEATURE [App::DocumentObjectGroupPython] Cl_element022  label="Cl_element : 011"  # scripted group (container) (typed FeaturePython)
  n = 1
  ref = Cl_element
FEATURE [App::DocumentObjectGroupPython] G4_SILVER_CHLORIDE  # scripted group (container) (typed FeaturePython)
  Dunit = g/cm3
  Dvalue = 5.56
  Group = -> [Ag_element003,Cl_element022]
  conduct = 2
  density = 1
  expand = 3
  formula = G4_SILVER_CHLORIDE
  name = G4_SILVER_CHLORIDE
  specific = 4
FEATURE [App::DocumentObjectGroupPython] Br_element006  label="Br_element : 0.423"  # scripted group (container) (typed FeaturePython)
  n = 0.422895
FEATURE [App::DocumentObjectGroupPython] Ag_element004  label="Ag_element : 0.574"  # scripted group (container) (typed FeaturePython)
  n = 0.573748
FEATURE [App::DocumentObjectGroupPython] I_element007  label="I_element : 0.649"  # scripted group (container) (typed FeaturePython)
  n = 0.003357
FEATURE [App::DocumentObjectGroupPython] G4_SILVER_HALIDES  # scripted group (container) (typed FeaturePython)
  Dunit = g/cm3
  Dvalue = 6.47
  Group = -> [Br_element006,Ag_element004,I_element007]
  conduct = 2
  density = 1
  expand = 3
  formula = G4_SILVER_HALIDES
  name = G4_SILVER_HALIDES
  specific = 4
FEATURE [App::DocumentObjectGroupPython] Ag_element005  label="Ag_element : 003"  # scripted group (container) (typed FeaturePython)
  n = 1
  ref = Ag_element
FEATURE [App::DocumentObjectGroupPython] I_element008  label="I_element : 004"  # scripted group (container) (typed FeaturePython)
  n = 1
  ref = I_element
FEATURE [App::DocumentObjectGroupPython] G4_SILVER_IODIDE  # scripted group (container) (typed FeaturePython)
  Dunit = g/cm3
  Dvalue = 6.01
  Group = -> [Ag_element005,I_element008]
  conduct = 2
  density = 1
  expand = 3
  formula = G4_SILVER_IODIDE
  name = G4_SILVER_IODIDE
  specific = 4
FEATURE [App::DocumentObjectGroupPython] H_element095  label="H_element : 0.100"  # scripted group (container) (typed FeaturePython)
  n = 0.1
FEATURE [App::DocumentObjectGroupPython] C_element103  label="C_element : 0.204"  # scripted group (container) (typed FeaturePython)
  n = 0.204
FEATURE [App::DocumentObjectGroupPython] N_element039  label="N_element : 0.759"  # scripted group (container) (typed FeaturePython)
  n = 0.042
FEATURE [App::DocumentObjectGroupPython] O_element088  label="O_element : 0.645"  # scripted group (container) (typed FeaturePython)
  n = 0.645
FEATURE [App::DocumentObjectGroupPython] Na_element013  label="Na_element : 0.100"  # scripted group (container) (typed FeaturePython)
  n = 0.002
FEATURE [App::DocumentObjectGroupPython] P_element009  label="P_element : 0.107"  # scripted group (container) (typed FeaturePython)
  n = 0.001
FEATURE [App::DocumentObjectGroupPython] S_element020  label="S_element : 0.021"  # scripted group (container) (typed FeaturePython)
  n = 0.002
FEATURE [App::DocumentObjectGroupPython] Cl_element023  label="Cl_element : 0.590"  # scripted group (container) (typed FeaturePython)
  n = 0.003
FEATURE [App::DocumentObjectGroupPython] K_element010  label="K_element : 0.001"  # scripted group (container) (typed FeaturePython)
  n = 0.001
FEATURE [App::DocumentObjectGroupPython] G4_SKIN_ICRP  # scripted group (container) (typed FeaturePython)
  Dunit = g/cm3
  Dvalue = 1.09
  Group = -> [H_element095,C_element103,N_element039,O_element088,Na_element013,P_element009,S_element020,Cl_element023,K_element010]
  conduct = 2
  density = 1
  expand = 3
  formula = G4_SKIN_ICRP
  name = G4_SKIN_ICRP
  specific = 4
FEATURE [App::DocumentObjectGroupPython] Na_element014  label="Na_element : 2"  # scripted group (container) (typed FeaturePython)
  n = 2
  ref = Na_element
FEATURE [App::DocumentObjectGroupPython] C_element104  label="C_element : 058"  # scripted group (container) (typed FeaturePython)
  n = 1
  ref = C_element
FEATURE [App::DocumentObjectGroupPython] O_element089  label="O_element : 049"  # scripted group (container) (typed FeaturePython)
  n = 3
  ref = O_element
FEATURE [App::DocumentObjectGroupPython] G4_SODIUM_CARBONATE  # scripted group (container) (typed FeaturePython)
  Dunit = g/cm3
  Dvalue = 2.532
  Group = -> [Na_element014,C_element104,O_element089]
  conduct = 2
  density = 1
  expand = 3
  formula = G4_SODIUM_CARBONATE
  name = G4_SODIUM_CARBONATE
  specific = 4
FEATURE [App::DocumentObjectGroupPython] Na_element015  label="Na_element : 1"  # scripted group (container) (typed FeaturePython)
  n = 1
  ref = Na_element
FEATURE [App::DocumentObjectGroupPython] I_element009  label="I_element : 005"  # scripted group (container) (typed FeaturePython)
  n = 1
  ref = I_element
FEATURE [App::DocumentObjectGroupPython] G4_SODIUM_IODIDE  # scripted group (container) (typed FeaturePython)
  Dunit = g/cm3
  Dvalue = 3.667
  Group = -> [Na_element015,I_element009]
  conduct = 2
  density = 1
  expand = 3
  formula = G4_SODIUM_IODIDE
  name = G4_SODIUM_IODIDE
  specific = 4
FEATURE [App::DocumentObjectGroupPython] Na_element016  label="Na_element : 003"  # scripted group (container) (typed FeaturePython)
  n = 2
  ref = Na_element
FEATURE [App::DocumentObjectGroupPython] O_element090  label="O_element : 050"  # scripted group (container) (typed FeaturePython)
  n = 1
  ref = O_element
FEATURE [App::DocumentObjectGroupPython] G4_SODIUM_MONOXIDE  # scripted group (container) (typed FeaturePython)
  Dunit = g/cm3
  Dvalue = 2.27
  Group = -> [Na_element016,O_element090]
  conduct = 2
  density = 1
  expand = 3
  formula = G4_SODIUM_MONOXIDE
  name = G4_SODIUM_MONOXIDE
  specific = 4
FEATURE [App::DocumentObjectGroupPython] Na_element017  label="Na_element : 004"  # scripted group (container) (typed FeaturePython)
  n = 1
  ref = Na_element
FEATURE [App::DocumentObjectGroupPython] N_element040  label="N_element : 018"  # scripted group (container) (typed FeaturePython)
  n = 1
  ref = N_element
FEATURE [App::DocumentObjectGroupPython] O_element091  label="O_element : 051"  # scripted group (container) (typed FeaturePython)
  n = 3
  ref = O_element
FEATURE [App::DocumentObjectGroupPython] G4_SODIUM_NITRATE  # scripted group (container) (typed FeaturePython)
  Dunit = g/cm3
  Dvalue = 2.261
  Group = -> [Na_element017,N_element040,O_element091]
  conduct = 2
  density = 1
  expand = 3
  formula = G4_SODIUM_NITRATE
  name = G4_SODIUM_NITRATE
  specific = 4
FEATURE [App::DocumentObjectGroupPython] C_element105  label="C_element : 059"  # scripted group (container) (typed FeaturePython)
  n = 14
  ref = C_element
FEATURE [App::DocumentObjectGroupPython] H_element096  label="H_element : 053"  # scripted group (container) (typed FeaturePython)
  n = 12
  ref = H_element
FEATURE [App::DocumentObjectGroupPython] G4_STILBENE  # scripted group (container) (typed FeaturePython)
  Dunit = g/cm3
  Dvalue = 0.9707
  Group = -> [C_element105,H_element096]
  conduct = 2
  density = 1
  expand = 3
  formula = G4_STILBENE
  name = G4_STILBENE
  specific = 4
FEATURE [App::DocumentObjectGroupPython] C_element106  label="C_element : 12"  # scripted group (container) (typed FeaturePython)
  n = 12
  ref = C_element
FEATURE [App::DocumentObjectGroupPython] H_element097  label="H_element : 22"  # scripted group (container) (typed FeaturePython)
  n = 22
  ref = H_element
FEATURE [App::DocumentObjectGroupPython] O_element092  label="O_element : 11"  # scripted group (container) (typed FeaturePython)
  n = 11
  ref = O_element
FEATURE [App::DocumentObjectGroupPython] G4_SUCROSE  # scripted group (container) (typed FeaturePython)
  Dunit = g/cm3
  Dvalue = 1.5805
  Group = -> [C_element106,H_element097,O_element092]
  conduct = 2
  density = 1
  expand = 3
  formula = G4_SUCROSE
  name = G4_SUCROSE
  specific = 4
FEATURE [App::DocumentObjectGroupPython] C_element107  label="C_element : 18"  # scripted group (container) (typed FeaturePython)
  n = 18
  ref = C_element
FEATURE [App::DocumentObjectGroupPython] H_element098  label="H_element : 054"  # scripted group (container) (typed FeaturePython)
  n = 14
  ref = H_element
FEATURE [App::DocumentObjectGroupPython] G4_TERPHENYL  # scripted group (container) (typed FeaturePython)
  Dunit = g/cm3
  Dvalue = 1.24
  Group = -> [C_element107,H_element098]
  conduct = 2
  density = 1
  expand = 3
  formula = G4_TERPHENYL
  name = G4_TERPHENYL
  specific = 4
FEATURE [App::DocumentObjectGroupPython] H_element099  label="H_element : 0.146"  # scripted group (container) (typed FeaturePython)
  n = 0.106
FEATURE [App::DocumentObjectGroupPython] C_element108  label="C_element : 0.883"  # scripted group (container) (typed FeaturePython)
  n = 0.099
FEATURE [App::DocumentObjectGroupPython] N_element041  label="N_element : 0.020"  # scripted group (container) (typed FeaturePython)
  n = 0.02
FEATURE [App::DocumentObjectGroupPython] O_element093  label="O_element : 0.766"  # scripted group (container) (typed FeaturePython)
  n = 0.766
FEATURE [App::DocumentObjectGroupPython] Na_element018  label="Na_element : 0.101"  # scripted group (container) (typed FeaturePython)
  n = 0.002
FEATURE [App::DocumentObjectGroupPython] P_element010  label="P_element : 0.108"  # scripted group (container) (typed FeaturePython)
  n = 0.001
FEATURE [App::DocumentObjectGroupPython] S_element021  label="S_element : 0.022"  # scripted group (container) (typed FeaturePython)
  n = 0.002
FEATURE [App::DocumentObjectGroupPython] Cl_element024  label="Cl_element : 0.002"  # scripted group (container) (typed FeaturePython)
  n = 0.002
FEATURE [App::DocumentObjectGroupPython] K_element011  label="K_element : 0.017"  # scripted group (container) (typed FeaturePython)
  n = 0.002
FEATURE [App::DocumentObjectGroupPython] G4_TESTIS_ICRP  # scripted group (container) (typed FeaturePython)
  Dunit = g/cm3
  Dvalue = 1.04
  Group = -> [H_element099,C_element108,N_element041,O_element093,Na_element018,P_element010,S_element021,Cl_element024,K_element011]
  conduct = 2
  density = 1
  expand = 3
  formula = G4_TESTIS_ICRP
  name = G4_TESTIS_ICRP
  specific = 4
FEATURE [App::DocumentObjectGroupPython] C_element109  label="C_element : 060"  # scripted group (container) (typed FeaturePython)
  n = 2
  ref = C_element
FEATURE [App::DocumentObjectGroupPython] Cl_element025  label="Cl_element : 012"  # scripted group (container) (typed FeaturePython)
  n = 4
  ref = Cl_element
FEATURE [App::DocumentObjectGroupPython] G4_TETRACHLOROETHYLENE  # scripted group (container) (typed FeaturePython)
  Dunit = g/cm3
  Dvalue = 1.625
  Group = -> [C_element109,Cl_element025]
  conduct = 2
  density = 1
  expand = 3
  formula = G4_TETRACHLOROETHYLENE
  name = G4_TETRACHLOROETHYLENE
  specific = 4
FEATURE [App::DocumentObjectGroupPython] Tl_element001  label="Tl_element : 1"  # scripted group (container) (typed FeaturePython)
  n = 1
  ref = Tl_element
FEATURE [App::DocumentObjectGroupPython] Cl_element026  label="Cl_element : 013"  # scripted group (container) (typed FeaturePython)
  n = 1
  ref = Cl_element
FEATURE [App::DocumentObjectGroupPython] G4_THALLIUM_CHLORIDE  # scripted group (container) (typed FeaturePython)
  Dunit = g/cm3
  Dvalue = 7.004
  Group = -> [Tl_element001,Cl_element026]
  conduct = 2
  density = 1
  expand = 3
  formula = G4_THALLIUM_CHLORIDE
  name = G4_THALLIUM_CHLORIDE
  specific = 4
FEATURE [App::DocumentObjectGroupPython] H_element100  label="H_element : 0.147"  # scripted group (container) (typed FeaturePython)
  n = 0.105
FEATURE [App::DocumentObjectGroupPython] C_element110  label="C_element : 0.256"  # scripted group (container) (typed FeaturePython)
  n = 0.256
FEATURE [App::DocumentObjectGroupPython] N_element042  label="N_element : 0.760"  # scripted group (container) (typed FeaturePython)
  n = 0.027
FEATURE [App::DocumentObjectGroupPython] O_element094  label="O_element : 0.602"  # scripted group (container) (typed FeaturePython)
  n = 0.602
FEATURE [App::DocumentObjectGroupPython] Na_element019  label="Na_element : 0.102"  # scripted group (container) (typed FeaturePython)
  n = 0.001
FEATURE [App::DocumentObjectGroupPython] P_element011  label="P_element : 0.109"  # scripted group (container) (typed FeaturePython)
  n = 0.002
FEATURE [App::DocumentObjectGroupPython] S_element022  label="S_element : 0.023"  # scripted group (container) (typed FeaturePython)
  n = 0.003
FEATURE [App::DocumentObjectGroupPython] Cl_element027  label="Cl_element : 0.591"  # scripted group (container) (typed FeaturePython)
  n = 0.002
FEATURE [App::DocumentObjectGroupPython] K_element012  label="K_element : 0.018"  # scripted group (container) (typed FeaturePython)
  n = 0.002
FEATURE [App::DocumentObjectGroupPython] G4_TISSUE_SOFT_ICRP  # scripted group (container) (typed FeaturePython)
  Dunit = g/cm3
  Dvalue = 1.03
  Group = -> [H_element100,C_element110,N_element042,O_element094,Na_element019,P_element011,S_element022,Cl_element027,K_element012]
  conduct = 2
  density = 1
  expand = 3
  formula = G4_TISSUE_SOFT_ICRP
  name = G4_TISSUE_SOFT_ICRP
  specific = 4
FEATURE [App::DocumentObjectGroupPython] H_element101  label="H_element : 0.148"  # scripted group (container) (typed FeaturePython)
  n = 0.101
FEATURE [App::DocumentObjectGroupPython] C_element111  label="C_element : 0.111"  # scripted group (container) (typed FeaturePython)
  n = 0.111
FEATURE [App::DocumentObjectGroupPython] N_element043  label="N_element : 0.026"  # scripted group (container) (typed FeaturePython)
  n = 0.026
FEATURE [App::DocumentObjectGroupPython] O_element095  label="O_element : 0.762"  # scripted group (container) (typed FeaturePython)
  n = 0.762
FEATURE [App::DocumentObjectGroupPython] G4_TISSUE_SOFT_ICRU_4  label="G4_TISSUE_SOFT_ICRU-4"  # scripted group (container) (typed FeaturePython)
  Dunit = g/cm3
  Dvalue = 1
  Group = -> [H_element101,C_element111,N_element043,O_element095]
  conduct = 2
  density = 1
  expand = 3
  formula = G4_TISSUE_SOFT_ICRU-4
  name = G4_TISSUE_SOFT_ICRU-4
  specific = 4
FEATURE [App::DocumentObjectGroupPython] H_element102  label="H_element : 0.149"  # scripted group (container) (typed FeaturePython)
  n = 0.101869
FEATURE [App::DocumentObjectGroupPython] C_element112  label="C_element : 0.456"  # scripted group (container) (typed FeaturePython)
  n = 0.456179
FEATURE [App::DocumentObjectGroupPython] N_element044  label="N_element : 0.761"  # scripted group (container) (typed FeaturePython)
  n = 0.035172
FEATURE [App::DocumentObjectGroupPython] O_element096  label="O_element : 0.407"  # scripted group (container) (typed FeaturePython)
  n = 0.40678
FEATURE [App::DocumentObjectGroupPython] G4_TISSUE_METHANE  label="G4_TISSUE-METHANE"  # scripted group (container) (typed FeaturePython)
  Dunit = g/cm3
  Dvalue = 0.00106409
  Group = -> [H_element102,C_element112,N_element044,O_element096]
  conduct = 2
  density = 1
  expand = 3
  formula = G4_TISSUE-METHANE
  name = G4_TISSUE-METHANE
  specific = 4
FEATURE [App::DocumentObjectGroupPython] H_element103  label="H_element : 0.103"  # scripted group (container) (typed FeaturePython)
  n = 0.102672
FEATURE [App::DocumentObjectGroupPython] C_element113  label="C_element : 0.569"  # scripted group (container) (typed FeaturePython)
  n = 0.56894
FEATURE [App::DocumentObjectGroupPython] N_element045  label="N_element : 0.762"  # scripted group (container) (typed FeaturePython)
  n = 0.035022
FEATURE [App::DocumentObjectGroupPython] O_element097  label="O_element : 0.293"  # scripted group (container) (typed FeaturePython)
  n = 0.293366
FEATURE [App::DocumentObjectGroupPython] G4_TISSUE_PROPANE  label="G4_TISSUE-PROPANE"  # scripted group (container) (typed FeaturePython)
  Dunit = g/cm3
  Dvalue = 0.00182628
  Group = -> [H_element103,C_element113,N_element045,O_element097]
  conduct = 2
  density = 1
  expand = 3
  formula = G4_TISSUE-PROPANE
  name = G4_TISSUE-PROPANE
  specific = 4
FEATURE [App::DocumentObjectGroupPython] Ti_element003  label="Ti_element : 1"  # scripted group (container) (typed FeaturePython)
  n = 1
  ref = Ti_element
FEATURE [App::DocumentObjectGroupPython] O_element098  label="O_element : 052"  # scripted group (container) (typed FeaturePython)
  n = 2
  ref = O_element
FEATURE [App::DocumentObjectGroupPython] G4_TITANIUM_DIOXIDE  # scripted group (container) (typed FeaturePython)
  Dunit = g/cm3
  Dvalue = 4.26
  Group = -> [Ti_element003,O_element098]
  conduct = 2
  density = 1
  expand = 3
  formula = G4_TITANIUM_DIOXIDE
  name = G4_TITANIUM_DIOXIDE
  specific = 4
FEATURE [App::DocumentObjectGroupPython] C_element114  label="C_element : 061"  # scripted group (container) (typed FeaturePython)
  n = 7
  ref = C_element
FEATURE [App::DocumentObjectGroupPython] H_element104  label="H_element : 055"  # scripted group (container) (typed FeaturePython)
  n = 8
  ref = H_element
FEATURE [App::DocumentObjectGroupPython] G4_TOLUENE  # scripted group (container) (typed FeaturePython)
  Dunit = g/cm3
  Dvalue = 0.8669
  Group = -> [C_element114,H_element104]
  conduct = 2
  density = 1
  expand = 3
  formula = G4_TOLUENE
  name = G4_TOLUENE
  specific = 4
FEATURE [App::DocumentObjectGroupPython] C_element115  label="C_element : 062"  # scripted group (container) (typed FeaturePython)
  n = 2
  ref = C_element
FEATURE [App::DocumentObjectGroupPython] H_element105  label="H_element : 056"  # scripted group (container) (typed FeaturePython)
  n = 1
  ref = H_element
FEATURE [App::DocumentObjectGroupPython] Cl_element028  label="Cl_element : 014"  # scripted group (container) (typed FeaturePython)
  n = 3
  ref = Cl_element
FEATURE [App::DocumentObjectGroupPython] G4_TRICHLOROETHYLENE  # scripted group (container) (typed FeaturePython)
  Dunit = g/cm3
  Dvalue = 1.46
  Group = -> [C_element115,H_element105,Cl_element028]
  conduct = 2
  density = 1
  expand = 3
  formula = G4_TRICHLOROETHYLENE
  name = G4_TRICHLOROETHYLENE
  specific = 4
FEATURE [App::DocumentObjectGroupPython] C_element116  label="C_element : 063"  # scripted group (container) (typed FeaturePython)
  n = 6
  ref = C_element
FEATURE [App::DocumentObjectGroupPython] H_element106  label="H_element : 15"  # scripted group (container) (typed FeaturePython)
  n = 15
  ref = H_element
FEATURE [App::DocumentObjectGroupPython] O_element099  label="O_element : 053"  # scripted group (container) (typed FeaturePython)
  n = 4
  ref = O_element
FEATURE [App::DocumentObjectGroupPython] P_element012  label="P_element : 1"  # scripted group (container) (typed FeaturePython)
  n = 1
  ref = P_element
FEATURE [App::DocumentObjectGroupPython] G4_TRIETHYL_PHOSPHATE  # scripted group (container) (typed FeaturePython)
  Dunit = g/cm3
  Dvalue = 1.07
  Group = -> [C_element116,H_element106,O_element099,P_element012]
  conduct = 2
  density = 1
  expand = 3
  formula = G4_TRIETHYL_PHOSPHATE
  name = G4_TRIETHYL_PHOSPHATE
  specific = 4
FEATURE [App::DocumentObjectGroupPython] W_element003  label="W_element : 003"  # scripted group (container) (typed FeaturePython)
  n = 1
  ref = W_element
FEATURE [App::DocumentObjectGroupPython] F_element017  label="F_element : 6"  # scripted group (container) (typed FeaturePython)
  n = 6
  ref = F_element
FEATURE [App::DocumentObjectGroupPython] G4_TUNGSTEN_HEXAFLUORIDE  # scripted group (container) (typed FeaturePython)
  Dunit = g/cm3
  Dvalue = 2.4
  Group = -> [W_element003,F_element017]
  conduct = 2
  density = 1
  expand = 3
  formula = G4_TUNGSTEN_HEXAFLUORIDE
  name = G4_TUNGSTEN_HEXAFLUORIDE
  specific = 4
FEATURE [App::DocumentObjectGroupPython] U_element001  label="U_element : 1"  # scripted group (container) (typed FeaturePython)
  n = 1
  ref = U_element
FEATURE [App::DocumentObjectGroupPython] C_element117  label="C_element : 064"  # scripted group (container) (typed FeaturePython)
  n = 2
  ref = C_element
FEATURE [App::DocumentObjectGroupPython] G4_URANIUM_DICARBIDE  # scripted group (container) (typed FeaturePython)
  Dunit = g/cm3
  Dvalue = 11.28
  Group = -> [U_element001,C_element117]
  conduct = 2
  density = 1
  expand = 3
  formula = G4_URANIUM_DICARBIDE
  name = G4_URANIUM_DICARBIDE
  specific = 4
FEATURE [App::DocumentObjectGroupPython] U_element002  label="U_element : 002"  # scripted group (container) (typed FeaturePython)
  n = 1
  ref = U_element
FEATURE [App::DocumentObjectGroupPython] C_element118  label="C_element : 065"  # scripted group (container) (typed FeaturePython)
  n = 1
  ref = C_element
FEATURE [App::DocumentObjectGroupPython] G4_URANIUM_MONOCARBIDE  # scripted group (container) (typed FeaturePython)
  Dunit = g/cm3
  Dvalue = 13.63
  Group = -> [U_element002,C_element118]
  conduct = 2
  density = 1
  expand = 3
  formula = G4_URANIUM_MONOCARBIDE
  name = G4_URANIUM_MONOCARBIDE
  specific = 4
FEATURE [App::DocumentObjectGroupPython] U_element003  label="U_element : 003"  # scripted group (container) (typed FeaturePython)
  n = 1
  ref = U_element
FEATURE [App::DocumentObjectGroupPython] O_element100  label="O_element : 054"  # scripted group (container) (typed FeaturePython)
  n = 2
  ref = O_element
FEATURE [App::DocumentObjectGroupPython] G4_URANIUM_OXIDE  # scripted group (container) (typed FeaturePython)
  Dunit = g/cm3
  Dvalue = 10.96
  Group = -> [U_element003,O_element100]
  conduct = 2
  density = 1
  expand = 3
  formula = G4_URANIUM_OXIDE
  name = G4_URANIUM_OXIDE
  specific = 4
FEATURE [App::DocumentObjectGroupPython] C_element119  label="C_element : 066"  # scripted group (container) (typed FeaturePython)
  n = 1
  ref = C_element
FEATURE [App::DocumentObjectGroupPython] H_element107  label="H_element : 057"  # scripted group (container) (typed FeaturePython)
  n = 4
  ref = H_element
FEATURE [App::DocumentObjectGroupPython] N_element046  label="N_element : 019"  # scripted group (container) (typed FeaturePython)
  n = 2
  ref = N_element
FEATURE [App::DocumentObjectGroupPython] O_element101  label="O_element : 055"  # scripted group (container) (typed FeaturePython)
  n = 1
  ref = O_element
FEATURE [App::DocumentObjectGroupPython] G4_UREA  # scripted group (container) (typed FeaturePython)
  Dunit = g/cm3
  Dvalue = 1.323
  Group = -> [C_element119,H_element107,N_element046,O_element101]
  conduct = 2
  density = 1
  expand = 3
  formula = G4_UREA
  name = G4_UREA
  specific = 4
FEATURE [App::DocumentObjectGroupPython] C_element120  label="C_element : 067"  # scripted group (container) (typed FeaturePython)
  n = 5
  ref = C_element
FEATURE [App::DocumentObjectGroupPython] H_element108  label="H_element : 058"  # scripted group (container) (typed FeaturePython)
  n = 11
  ref = H_element
FEATURE [App::DocumentObjectGroupPython] N_element047  label="N_element : 020"  # scripted group (container) (typed FeaturePython)
  n = 1
  ref = N_element
FEATURE [App::DocumentObjectGroupPython] O_element102  label="O_element : 056"  # scripted group (container) (typed FeaturePython)
  n = 2
  ref = O_element
FEATURE [App::DocumentObjectGroupPython] G4_VALINE  # scripted group (container) (typed FeaturePython)
  Dunit = g/cm3
  Dvalue = 1.23
  Group = -> [C_element120,H_element108,N_element047,O_element102]
  conduct = 2
  density = 1
  expand = 3
  formula = G4_VALINE
  name = G4_VALINE
  specific = 4
FEATURE [App::DocumentObjectGroupPython] H_element109  label="H_element : 0.009"  # scripted group (container) (typed FeaturePython)
  n = 0.009417
FEATURE [App::DocumentObjectGroupPython] C_element121  label="C_element : 0.281"  # scripted group (container) (typed FeaturePython)
  n = 0.280555
FEATURE [App::DocumentObjectGroupPython] F_element018  label="F_element : 0.710"  # scripted group (container) (typed FeaturePython)
  n = 0.710028
FEATURE [App::DocumentObjectGroupPython] G4_VITON  # scripted group (container) (typed FeaturePython)
  Dunit = g/cm3
  Dvalue = 1.8
  Group = -> [H_element109,C_element121,F_element018]
  conduct = 2
  density = 1
  expand = 3
  formula = G4_VITON
  name = G4_VITON
  specific = 4
FEATURE [App::DocumentObjectGroupPython] H_element110  label="H_element : 059"  # scripted group (container) (typed FeaturePython)
  n = 2
  ref = H_element
FEATURE [App::DocumentObjectGroupPython] O_element103  label="O_element : 057"  # scripted group (container) (typed FeaturePython)
  n = 1
  ref = O_element
FEATURE [App::DocumentObjectGroupPython] G4_WATER  # scripted group (container) (typed FeaturePython)
  Dunit = g/cm3
  Dvalue = 1
  Group = -> [H_element110,O_element103]
  conduct = 2
  density = 1
  expand = 3
  formula = G4_WATER
  name = G4_WATER
  specific = 4
FEATURE [App::DocumentObjectGroupPython] H_element111  label="H_element : 060"  # scripted group (container) (typed FeaturePython)
  n = 2
  ref = H_element
FEATURE [App::DocumentObjectGroupPython] O_element104  label="O_element : 058"  # scripted group (container) (typed FeaturePython)
  n = 1
  ref = O_element
FEATURE [App::DocumentObjectGroupPython] G4_WATER_VAPOR  # scripted group (container) (typed FeaturePython)
  Dunit = g/cm3
  Dvalue = 0.000756182
  Group = -> [H_element111,O_element104]
  conduct = 2
  density = 1
  expand = 3
  formula = G4_WATER_VAPOR
  name = G4_WATER_VAPOR
  specific = 4
FEATURE [App::DocumentObjectGroupPython] C_element122  label="C_element : 068"  # scripted group (container) (typed FeaturePython)
  n = 8
  ref = C_element
FEATURE [App::DocumentObjectGroupPython] H_element112  label="H_element : 061"  # scripted group (container) (typed FeaturePython)
  n = 10
  ref = H_element
FEATURE [App::DocumentObjectGroupPython] G4_XYLENE  # scripted group (container) (typed FeaturePython)
  Dunit = g/cm3
  Dvalue = 0.87
  Group = -> [C_element122,H_element112]
  conduct = 2
  density = 1
  expand = 3
  formula = G4_XYLENE
  name = G4_XYLENE
  specific = 4
FEATURE [App::DocumentObjectGroupPython] C_element123  label="C_element : 069"  # scripted group (container) (typed FeaturePython)
  n = 1
  ref = C_element
FEATURE [App::DocumentObjectGroupPython] G4_GRAPHITE  # scripted group (container) (typed FeaturePython)
  Dunit = g/cm3
  Dvalue = 2.21
  Group = -> [C_element123]
  conduct = 2
  density = 1
  expand = 3
  formula = G4_GRAPHITE
  name = G4_GRAPHITE
  specific = 4
FEATURE [App::DocumentObjectGroupPython] NIST  # scripted group (container) (typed FeaturePython)
  Group = -> [G4_A_150_TISSUE,G4_ACETONE,G4_ACETYLENE,G4_ADENINE,G4_ADIPOSE_TISSUE_ICRP,G4_AIR,G4_ALANINE,G4_ALUMINUM_OXIDE,G4_AMBER,G4_AMMONIA,G4_ANILINE,G4_ANTHRACENE,G4_B_100_BONE,G4_BAKELITE,G4_BARIUM_FLUORIDE,G4_BARIUM_SULFATE,G4_BENZENE,G4_BERYLLIUM_OXIDE,G4_BGO,G4_BLOOD_ICRP,G4_BONE_COMPACT_ICRU,G4_BONE_CORTICAL_ICRP,G4_BORON_CARBIDE,G4_BORON_OXIDE,G4_BRAIN_ICRP,G4_BUTANE,G4_N_BUTYL_ALCOHOL,G4_C_552,+152 more]
FEATURE [App::DocumentObjectGroupPython] H_element113  label="H_element : 062"  # scripted group (container) (typed FeaturePython)
  n = 1
  ref = H_element
FEATURE [App::DocumentObjectGroupPython] G4_H  # scripted group (container) (typed FeaturePython)
  Dunit = g/cm3
  Dvalue = 8.3748e-05
  Group = -> [H_element113]
  conduct = 2
  density = 1
  expand = 3
  formula = H
  name = G4_H
  specific = 4
FEATURE [App::DocumentObjectGroupPython] He_element001  label="He_element : 1"  # scripted group (container) (typed FeaturePython)
  n = 1
  ref = He_element
FEATURE [App::DocumentObjectGroupPython] G4_He  # scripted group (container) (typed FeaturePython)
  Dunit = g/cm3
  Dvalue = 0.000166322
  Group = -> [He_element001]
  conduct = 2
  density = 1
  expand = 3
  formula = He
  name = G4_He
  specific = 4
FEATURE [App::DocumentObjectGroupPython] Li_element008  label="Li_element : 008"  # scripted group (container) (typed FeaturePython)
  n = 1
  ref = Li_element
FEATURE [App::DocumentObjectGroupPython] G4_Li  # scripted group (container) (typed FeaturePython)
  Dunit = g/cm3
  Dvalue = 0.534
  Group = -> [Li_element008]
  conduct = 2
  density = 1
  expand = 3
  formula = Li
  name = G4_Li
  specific = 4
FEATURE [App::DocumentObjectGroupPython] Be_element002  label="Be_element : 002"  # scripted group (container) (typed FeaturePython)
  n = 1
  ref = Be_element
FEATURE [App::DocumentObjectGroupPython] G4_Be  # scripted group (container) (typed FeaturePython)
  Dunit = g/cm3
  Dvalue = 1.848
  Group = -> [Be_element002]
  conduct = 2
  density = 1
  expand = 3
  formula = Be
  name = G4_Be
  specific = 4
FEATURE [App::DocumentObjectGroupPython] B_element007  label="B_element : 007"  # scripted group (container) (typed FeaturePython)
  n = 1
  ref = B_element
FEATURE [App::DocumentObjectGroupPython] G4_B  # scripted group (container) (typed FeaturePython)
  Dunit = g/cm3
  Dvalue = 2.37
  Group = -> [B_element007]
  conduct = 2
  density = 1
  expand = 3
  formula = B
  name = G4_B
  specific = 4
FEATURE [App::DocumentObjectGroupPython] C_element124  label="C_element : 070"  # scripted group (container) (typed FeaturePython)
  n = 1
  ref = C_element
FEATURE [App::DocumentObjectGroupPython] G4_C  # scripted group (container) (typed FeaturePython)
  Dunit = g/cm3
  Dvalue = 2
  Group = -> [C_element124]
  conduct = 2
  density = 1
  expand = 3
  formula = C
  name = G4_C
  specific = 4
FEATURE [App::DocumentObjectGroupPython] N_element048  label="N_element : 021"  # scripted group (container) (typed FeaturePython)
  n = 1
  ref = N_element
FEATURE [App::DocumentObjectGroupPython] G4_N  # scripted group (container) (typed FeaturePython)
  Dunit = g/cm3
  Dvalue = 0.0011652
  Group = -> [N_element048]
  conduct = 2
  density = 1
  expand = 3
  formula = N
  name = G4_N
  specific = 4
FEATURE [App::DocumentObjectGroupPython] O_element105  label="O_element : 059"  # scripted group (container) (typed FeaturePython)
  n = 1
  ref = O_element
FEATURE [App::DocumentObjectGroupPython] G4_O  # scripted group (container) (typed FeaturePython)
  Dunit = g/cm3
  Dvalue = 0.00133151
  Group = -> [O_element105]
  conduct = 2
  density = 1
  expand = 3
  formula = O
  name = G4_O
  specific = 4
FEATURE [App::DocumentObjectGroupPython] F_element019  label="F_element : 008"  # scripted group (container) (typed FeaturePython)
  n = 1
  ref = F_element
FEATURE [App::DocumentObjectGroupPython] G4_F  # scripted group (container) (typed FeaturePython)
  Dunit = g/cm3
  Dvalue = 0.00158029
  Group = -> [F_element019]
  conduct = 2
  density = 1
  expand = 3
  formula = F
  name = G4_F
  specific = 4
FEATURE [App::DocumentObjectGroupPython] Ne_element001  label="Ne_element : 1"  # scripted group (container) (typed FeaturePython)
  n = 1
  ref = Ne_element
FEATURE [App::DocumentObjectGroupPython] G4_Ne  # scripted group (container) (typed FeaturePython)
  Dunit = g/cm3
  Dvalue = 0.000838505
  Group = -> [Ne_element001]
  conduct = 2
  density = 1
  expand = 3
  formula = Ne
  name = G4_Ne
  specific = 4
FEATURE [App::DocumentObjectGroupPython] Na_element020  label="Na_element : 005"  # scripted group (container) (typed FeaturePython)
  n = 1
  ref = Na_element
FEATURE [App::DocumentObjectGroupPython] G4_Na  # scripted group (container) (typed FeaturePython)
  Dunit = g/cm3
  Dvalue = 0.971
  Group = -> [Na_element020]
  conduct = 2
  density = 1
  expand = 3
  formula = Na
  name = G4_Na
  specific = 4
FEATURE [App::DocumentObjectGroupPython] Mg_element011  label="Mg_element : 005"  # scripted group (container) (typed FeaturePython)
  n = 1
  ref = Mg_element
FEATURE [App::DocumentObjectGroupPython] G4_Mg  # scripted group (container) (typed FeaturePython)
  Dunit = g/cm3
  Dvalue = 1.74
  Group = -> [Mg_element011]
  conduct = 2
  density = 1
  expand = 3
  formula = Mg
  name = G4_Mg
  specific = 4
FEATURE [App::DocumentObjectGroupPython] Al_element004  label="Al_element : 1"  # scripted group (container) (typed FeaturePython)
  n = 1
  ref = Al_element
FEATURE [App::DocumentObjectGroupPython] G4_Al  # scripted group (container) (typed FeaturePython)
  Dunit = g/cm3
  Dvalue = 2.699
  Group = -> [Al_element004]
  conduct = 2
  density = 1
  expand = 3
  formula = Al
  name = G4_Al
  specific = 4
FEATURE [App::DocumentObjectGroupPython] Si_element007  label="Si_element : 002"  # scripted group (container) (typed FeaturePython)
  n = 1
  ref = Si_element
FEATURE [App::DocumentObjectGroupPython] G4_Si  # scripted group (container) (typed FeaturePython)
  Dunit = g/cm3
  Dvalue = 2.33
  Group = -> [Si_element007]
  conduct = 2
  density = 1
  expand = 3
  formula = Si
  name = G4_Si
  specific = 4
FEATURE [App::DocumentObjectGroupPython] P_element013  label="P_element : 002"  # scripted group (container) (typed FeaturePython)
  n = 1
  ref = P_element
FEATURE [App::DocumentObjectGroupPython] G4_P  # scripted group (container) (typed FeaturePython)
  Dunit = g/cm3
  Dvalue = 2.2
  Group = -> [P_element013]
  conduct = 2
  density = 1
  expand = 3
  formula = P
  name = G4_P
  specific = 4
FEATURE [App::DocumentObjectGroupPython] S_element023  label="S_element : 007"  # scripted group (container) (typed FeaturePython)
  n = 1
  ref = S_element
FEATURE [App::DocumentObjectGroupPython] G4_S  # scripted group (container) (typed FeaturePython)
  Dunit = g/cm3
  Dvalue = 2
  Group = -> [S_element023]
  conduct = 2
  density = 1
  expand = 3
  formula = S
  name = G4_S
  specific = 4
FEATURE [App::DocumentObjectGroupPython] Cl_element029  label="Cl_element : 015"  # scripted group (container) (typed FeaturePython)
  n = 1
  ref = Cl_element
FEATURE [App::DocumentObjectGroupPython] G4_Cl  # scripted group (container) (typed FeaturePython)
  Dunit = g/cm3
  Dvalue = 0.00299473
  Group = -> [Cl_element029]
  conduct = 2
  density = 1
  expand = 3
  formula = Cl
  name = G4_Cl
  specific = 4
FEATURE [App::DocumentObjectGroupPython] Ar_element002  label="Ar_element : 1"  # scripted group (container) (typed FeaturePython)
  n = 1
  ref = Ar_element
FEATURE [App::DocumentObjectGroupPython] G4_Ar  # scripted group (container) (typed FeaturePython)
  Dunit = g/cm3
  Dvalue = 0.00166201
  Group = -> [Ar_element002]
  conduct = 2
  density = 1
  expand = 3
  formula = Ar
  name = G4_Ar
  specific = 4
FEATURE [App::DocumentObjectGroupPython] K_element013  label="K_element : 003"  # scripted group (container) (typed FeaturePython)
  n = 1
  ref = K_element
FEATURE [App::DocumentObjectGroupPython] G4_K  # scripted group (container) (typed FeaturePython)
  Dunit = g/cm3
  Dvalue = 0.862
  Group = -> [K_element013]
  conduct = 2
  density = 1
  expand = 3
  formula = K
  name = G4_K
  specific = 4
FEATURE [App::DocumentObjectGroupPython] Ca_element014  label="Ca_element : 007"  # scripted group (container) (typed FeaturePython)
  n = 1
  ref = Ca_element
FEATURE [App::DocumentObjectGroupPython] G4_Ca  # scripted group (container) (typed FeaturePython)
  Dunit = g/cm3
  Dvalue = 1.55
  Group = -> [Ca_element014]
  conduct = 2
  density = 1
  expand = 3
  formula = Ca
  name = G4_Ca
  specific = 4
FEATURE [App::DocumentObjectGroupPython] Sc_element001  label="Sc_element : 1"  # scripted group (container) (typed FeaturePython)
  n = 1
  ref = Sc_element
FEATURE [App::DocumentObjectGroupPython] G4_Sc  # scripted group (container) (typed FeaturePython)
  Dunit = g/cm3
  Dvalue = 2.989
  Group = -> [Sc_element001]
  conduct = 2
  density = 1
  expand = 3
  formula = Sc
  name = G4_Sc
  specific = 4
FEATURE [App::DocumentObjectGroupPython] Ti_element004  label="Ti_element : 002"  # scripted group (container) (typed FeaturePython)
  n = 1
  ref = Ti_element
FEATURE [App::DocumentObjectGroupPython] G4_Ti  # scripted group (container) (typed FeaturePython)
  Dunit = g/cm3
  Dvalue = 4.54
  Group = -> [Ti_element004]
  conduct = 2
  density = 1
  expand = 3
  formula = Ti
  name = G4_Ti
  specific = 4
FEATURE [App::DocumentObjectGroupPython] V_element001  label="V_element : 1"  # scripted group (container) (typed FeaturePython)
  n = 1
  ref = V_element
FEATURE [App::DocumentObjectGroupPython] G4_V  # scripted group (container) (typed FeaturePython)
  Dunit = g/cm3
  Dvalue = 6.11
  Group = -> [V_element001]
  conduct = 2
  density = 1
  expand = 3
  formula = V
  name = G4_V
  specific = 4
FEATURE [App::DocumentObjectGroupPython] Cr_element001  label="Cr_element : 1"  # scripted group (container) (typed FeaturePython)
  n = 1
  ref = Cr_element
FEATURE [App::DocumentObjectGroupPython] G4_Cr  # scripted group (container) (typed FeaturePython)
  Dunit = g/cm3
  Dvalue = 7.18
  Group = -> [Cr_element001]
  conduct = 2
  density = 1
  expand = 3
  formula = Cr
  name = G4_Cr
  specific = 4
FEATURE [App::DocumentObjectGroupPython] Mn_element001  label="Mn_element : 1"  # scripted group (container) (typed FeaturePython)
  n = 1
  ref = Mn_element
FEATURE [App::DocumentObjectGroupPython] G4_Mn  # scripted group (container) (typed FeaturePython)
  Dunit = g/cm3
  Dvalue = 7.44
  Group = -> [Mn_element001]
  conduct = 2
  density = 1
  expand = 3
  formula = Mn
  name = G4_Mn
  specific = 4
FEATURE [App::DocumentObjectGroupPython] Fe_element007  label="Fe_element : 004"  # scripted group (container) (typed FeaturePython)
  n = 1
  ref = Fe_element
FEATURE [App::DocumentObjectGroupPython] G4_Fe  # scripted group (container) (typed FeaturePython)
  Dunit = g/cm3
  Dvalue = 7.874
  Group = -> [Fe_element007]
  conduct = 2
  density = 1
  expand = 3
  formula = Fe
  name = G4_Fe
  specific = 4
FEATURE [App::DocumentObjectGroupPython] Co_element001  label="Co_element : 1"  # scripted group (container) (typed FeaturePython)
  n = 1
  ref = Co_element
FEATURE [App::DocumentObjectGroupPython] G4_Co  # scripted group (container) (typed FeaturePython)
  Dunit = g/cm3
  Dvalue = 8.9
  Group = -> [Co_element001]
  conduct = 2
  density = 1
  expand = 3
  formula = Co
  name = G4_Co
  specific = 4
FEATURE [App::DocumentObjectGroupPython] Ni_element001  label="Ni_element : 1"  # scripted group (container) (typed FeaturePython)
  n = 1
  ref = Ni_element
FEATURE [App::DocumentObjectGroupPython] G4_Ni  # scripted group (container) (typed FeaturePython)
  Dunit = g/cm3
  Dvalue = 8.902
  Group = -> [Ni_element001]
  conduct = 2
  density = 1
  expand = 3
  formula = Ni
  name = G4_Ni
  specific = 4
FEATURE [App::DocumentObjectGroupPython] Cu_element001  label="Cu_element : 1"  # scripted group (container) (typed FeaturePython)
  n = 1
  ref = Cu_element
FEATURE [App::DocumentObjectGroupPython] G4_Cu  # scripted group (container) (typed FeaturePython)
  Dunit = g/cm3
  Dvalue = 8.96
  Group = -> [Cu_element001]
  conduct = 2
  density = 1
  expand = 3
  formula = Cu
  name = G4_Cu
  specific = 4
FEATURE [App::DocumentObjectGroupPython] Zn_element001  label="Zn_element : 1"  # scripted group (container) (typed FeaturePython)
  n = 1
  ref = Zn_element
FEATURE [App::DocumentObjectGroupPython] G4_Zn  # scripted group (container) (typed FeaturePython)
  Dunit = g/cm3
  Dvalue = 7.133
  Group = -> [Zn_element001]
  conduct = 2
  density = 1
  expand = 3
  formula = Zn
  name = G4_Zn
  specific = 4
FEATURE [App::DocumentObjectGroupPython] Ga_element002  label="Ga_element : 002"  # scripted group (container) (typed FeaturePython)
  n = 1
  ref = Ga_element
FEATURE [App::DocumentObjectGroupPython] G4_Ga  # scripted group (container) (typed FeaturePython)
  Dunit = g/cm3
  Dvalue = 5.904
  Group = -> [Ga_element002]
  conduct = 2
  density = 1
  expand = 3
  formula = Ga
  name = G4_Ga
  specific = 4
FEATURE [App::DocumentObjectGroupPython] Ge_element002  label="Ge_element : 1"  # scripted group (container) (typed FeaturePython)
  n = 1
  ref = Ge_element
FEATURE [App::DocumentObjectGroupPython] G4_Ge  # scripted group (container) (typed FeaturePython)
  Dunit = g/cm3
  Dvalue = 5.323
  Group = -> [Ge_element002]
  conduct = 2
  density = 1
  expand = 3
  formula = Ge
  name = G4_Ge
  specific = 4
FEATURE [App::DocumentObjectGroupPython] As_element003  label="As_element : 002"  # scripted group (container) (typed FeaturePython)
  n = 1
  ref = As_element
FEATURE [App::DocumentObjectGroupPython] G4_As  # scripted group (container) (typed FeaturePython)
  Dunit = g/cm3
  Dvalue = 5.73
  Group = -> [As_element003]
  conduct = 2
  density = 1
  expand = 3
  formula = As
  name = G4_As
  specific = 4
FEATURE [App::DocumentObjectGroupPython] Se_element001  label="Se_element : 1"  # scripted group (container) (typed FeaturePython)
  n = 1
  ref = Se_element
FEATURE [App::DocumentObjectGroupPython] G4_Se  # scripted group (container) (typed FeaturePython)
  Dunit = g/cm3
  Dvalue = 4.5
  Group = -> [Se_element001]
  conduct = 2
  density = 1
  expand = 3
  formula = Se
  name = G4_Se
  specific = 4
FEATURE [App::DocumentObjectGroupPython] Br_element007  label="Br_element : 004"  # scripted group (container) (typed FeaturePython)
  n = 1
  ref = Br_element
FEATURE [App::DocumentObjectGroupPython] G4_Br  # scripted group (container) (typed FeaturePython)
  Dunit = g/cm3
  Dvalue = 0.0070721
  Group = -> [Br_element007]
  conduct = 2
  density = 1
  expand = 3
  formula = Br
  name = G4_Br
  specific = 4
FEATURE [App::DocumentObjectGroupPython] Kr_element001  label="Kr_element : 1"  # scripted group (container) (typed FeaturePython)
  n = 1
  ref = Kr_element
FEATURE [App::DocumentObjectGroupPython] G4_Kr  # scripted group (container) (typed FeaturePython)
  Dunit = g/cm3
  Dvalue = 0.00347832
  Group = -> [Kr_element001]
  conduct = 2
  density = 1
  expand = 3
  formula = Kr
  name = G4_Kr
  specific = 4
FEATURE [App::DocumentObjectGroupPython] Rb_element001  label="Rb_element : 1"  # scripted group (container) (typed FeaturePython)
  n = 1
  ref = Rb_element
FEATURE [App::DocumentObjectGroupPython] G4_Rb  # scripted group (container) (typed FeaturePython)
  Dunit = g/cm3
  Dvalue = 1.532
  Group = -> [Rb_element001]
  conduct = 2
  density = 1
  expand = 3
  formula = Rb
  name = G4_Rb
  specific = 4
FEATURE [App::DocumentObjectGroupPython] Sr_element001  label="Sr_element : 1"  # scripted group (container) (typed FeaturePython)
  n = 1
  ref = Sr_element
FEATURE [App::DocumentObjectGroupPython] G4_Sr  # scripted group (container) (typed FeaturePython)
  Dunit = g/cm3
  Dvalue = 2.54
  Group = -> [Sr_element001]
  conduct = 2
  density = 1
  expand = 3
  formula = Sr
  name = G4_Sr
  specific = 4
FEATURE [App::DocumentObjectGroupPython] Y_element001  label="Y_element : 1"  # scripted group (container) (typed FeaturePython)
  n = 1
  ref = Y_element
FEATURE [App::DocumentObjectGroupPython] G4_Y  # scripted group (container) (typed FeaturePython)
  Dunit = g/cm3
  Dvalue = 4.469
  Group = -> [Y_element001]
  conduct = 2
  density = 1
  expand = 3
  formula = Y
  name = G4_Y
  specific = 4
FEATURE [App::DocumentObjectGroupPython] Zr_element001  label="Zr_element : 1"  # scripted group (container) (typed FeaturePython)
  n = 1
  ref = Zr_element
FEATURE [App::DocumentObjectGroupPython] G4_Zr  # scripted group (container) (typed FeaturePython)
  Dunit = g/cm3
  Dvalue = 6.506
  Group = -> [Zr_element001]
  conduct = 2
  density = 1
  expand = 3
  formula = Zr
  name = G4_Zr
  specific = 4
FEATURE [App::DocumentObjectGroupPython] Nb_element001  label="Nb_element : 1"  # scripted group (container) (typed FeaturePython)
  n = 1
  ref = Nb_element
FEATURE [App::DocumentObjectGroupPython] G4_Nb  # scripted group (container) (typed FeaturePython)
  Dunit = g/cm3
  Dvalue = 8.57
  Group = -> [Nb_element001]
  conduct = 2
  density = 1
  expand = 3
  formula = Nb
  name = G4_Nb
  specific = 4
FEATURE [App::DocumentObjectGroupPython] Mo_element001  label="Mo_element : 1"  # scripted group (container) (typed FeaturePython)
  n = 1
  ref = Mo_element
FEATURE [App::DocumentObjectGroupPython] G4_Mo  # scripted group (container) (typed FeaturePython)
  Dunit = g/cm3
  Dvalue = 10.22
  Group = -> [Mo_element001]
  conduct = 2
  density = 1
  expand = 3
  formula = Mo
  name = G4_Mo
  specific = 4
FEATURE [App::DocumentObjectGroupPython] Tc_element001  label="Tc_element : 1"  # scripted group (container) (typed FeaturePython)
  n = 1
  ref = Tc_element
FEATURE [App::DocumentObjectGroupPython] G4_Tc  # scripted group (container) (typed FeaturePython)
  Dunit = g/cm3
  Dvalue = 11.5
  Group = -> [Tc_element001]
  conduct = 2
  density = 1
  expand = 3
  formula = Tc
  name = G4_Tc
  specific = 4
FEATURE [App::DocumentObjectGroupPython] Ru_element001  label="Ru_element : 1"  # scripted group (container) (typed FeaturePython)
  n = 1
  ref = Ru_element
FEATURE [App::DocumentObjectGroupPython] G4_Ru  # scripted group (container) (typed FeaturePython)
  Dunit = g/cm3
  Dvalue = 12.41
  Group = -> [Ru_element001]
  conduct = 2
  density = 1
  expand = 3
  formula = Ru
  name = G4_Ru
  specific = 4
FEATURE [App::DocumentObjectGroupPython] Rh_element001  label="Rh_element : 1"  # scripted group (container) (typed FeaturePython)
  n = 1
  ref = Rh_element
FEATURE [App::DocumentObjectGroupPython] G4_Rh  # scripted group (container) (typed FeaturePython)
  Dunit = g/cm3
  Dvalue = 12.41
  Group = -> [Rh_element001]
  conduct = 2
  density = 1
  expand = 3
  formula = Rh
  name = G4_Rh
  specific = 4
FEATURE [App::DocumentObjectGroupPython] Pd_element001  label="Pd_element : 1"  # scripted group (container) (typed FeaturePython)
  n = 1
  ref = Pd_element
FEATURE [App::DocumentObjectGroupPython] G4_Pd  # scripted group (container) (typed FeaturePython)
  Dunit = g/cm3
  Dvalue = 12.02
  Group = -> [Pd_element001]
  conduct = 2
  density = 1
  expand = 3
  formula = Pd
  name = G4_Pd
  specific = 4
FEATURE [App::DocumentObjectGroupPython] Ag_element006  label="Ag_element : 004"  # scripted group (container) (typed FeaturePython)
  n = 1
  ref = Ag_element
FEATURE [App::DocumentObjectGroupPython] G4_Ag  # scripted group (container) (typed FeaturePython)
  Dunit = g/cm3
  Dvalue = 10.5
  Group = -> [Ag_element006]
  conduct = 2
  density = 1
  expand = 3
  formula = Ag
  name = G4_Ag
  specific = 4
FEATURE [App::DocumentObjectGroupPython] Cd_element003  label="Cd_element : 003"  # scripted group (container) (typed FeaturePython)
  n = 1
  ref = Cd_element
FEATURE [App::DocumentObjectGroupPython] G4_Cd  # scripted group (container) (typed FeaturePython)
  Dunit = g/cm3
  Dvalue = 8.65
  Group = -> [Cd_element003]
  conduct = 2
  density = 1
  expand = 3
  formula = Cd
  name = G4_Cd
  specific = 4
FEATURE [App::DocumentObjectGroupPython] In_element001  label="In_element : 1"  # scripted group (container) (typed FeaturePython)
  n = 1
  ref = In_element
FEATURE [App::DocumentObjectGroupPython] G4_In  # scripted group (container) (typed FeaturePython)
  Dunit = g/cm3
  Dvalue = 7.31
  Group = -> [In_element001]
  conduct = 2
  density = 1
  expand = 3
  formula = In
  name = G4_In
  specific = 4
FEATURE [App::DocumentObjectGroupPython] Sn_element001  label="Sn_element : 1"  # scripted group (container) (typed FeaturePython)
  n = 1
  ref = Sn_element
FEATURE [App::DocumentObjectGroupPython] G4_Sn  # scripted group (container) (typed FeaturePython)
  Dunit = g/cm3
  Dvalue = 7.31
  Group = -> [Sn_element001]
  conduct = 2
  density = 1
  expand = 3
  formula = Sn
  name = G4_Sn
  specific = 4
FEATURE [App::DocumentObjectGroupPython] Sb_element001  label="Sb_element : 1"  # scripted group (container) (typed FeaturePython)
  n = 1
  ref = Sb_element
FEATURE [App::DocumentObjectGroupPython] G4_Sb  # scripted group (container) (typed FeaturePython)
  Dunit = g/cm3
  Dvalue = 6.691
  Group = -> [Sb_element001]
  conduct = 2
  density = 1
  expand = 3
  formula = Sb
  name = G4_Sb
  specific = 4
FEATURE [App::DocumentObjectGroupPython] Te_element002  label="Te_element : 002"  # scripted group (container) (typed FeaturePython)
  n = 1
  ref = Te_element
FEATURE [App::DocumentObjectGroupPython] G4_Te  # scripted group (container) (typed FeaturePython)
  Dunit = g/cm3
  Dvalue = 6.24
  Group = -> [Te_element002]
  conduct = 2
  density = 1
  expand = 3
  formula = Te
  name = G4_Te
  specific = 4
FEATURE [App::DocumentObjectGroupPython] I_element010  label="I_element : 006"  # scripted group (container) (typed FeaturePython)
  n = 1
  ref = I_element
FEATURE [App::DocumentObjectGroupPython] G4_I  # scripted group (container) (typed FeaturePython)
  Dunit = g/cm3
  Dvalue = 4.93
  Group = -> [I_element010]
  conduct = 2
  density = 1
  expand = 3
  formula = I
  name = G4_I
  specific = 4
FEATURE [App::DocumentObjectGroupPython] Xe_element001  label="Xe_element : 1"  # scripted group (container) (typed FeaturePython)
  n = 1
  ref = Xe_element
FEATURE [App::DocumentObjectGroupPython] G4_Xe  # scripted group (container) (typed FeaturePython)
  Dunit = g/cm3
  Dvalue = 0.00548536
  Group = -> [Xe_element001]
  conduct = 2
  density = 1
  expand = 3
  formula = Xe
  name = G4_Xe
  specific = 4
FEATURE [App::DocumentObjectGroupPython] Cs_element003  label="Cs_element : 003"  # scripted group (container) (typed FeaturePython)
  n = 1
  ref = Cs_element
FEATURE [App::DocumentObjectGroupPython] G4_Cs  # scripted group (container) (typed FeaturePython)
  Dunit = g/cm3
  Dvalue = 1.873
  Group = -> [Cs_element003]
  conduct = 2
  density = 1
  expand = 3
  formula = Cs
  name = G4_Cs
  specific = 4
FEATURE [App::DocumentObjectGroupPython] Ba_element003  label="Ba_element : 003"  # scripted group (container) (typed FeaturePython)
  n = 1
  ref = Ba_element
FEATURE [App::DocumentObjectGroupPython] G4_Ba  # scripted group (container) (typed FeaturePython)
  Dunit = g/cm3
  Dvalue = 3.5
  Group = -> [Ba_element003]
  conduct = 2
  density = 1
  expand = 3
  formula = Ba
  name = G4_Ba
  specific = 4
FEATURE [App::DocumentObjectGroupPython] La_element003  label="La_element : 003"  # scripted group (container) (typed FeaturePython)
  n = 1
  ref = La_element
FEATURE [App::DocumentObjectGroupPython] G4_La  # scripted group (container) (typed FeaturePython)
  Dunit = g/cm3
  Dvalue = 6.154
  Group = -> [La_element003]
  conduct = 2
  density = 1
  expand = 3
  formula = La
  name = G4_La
  specific = 4
FEATURE [App::DocumentObjectGroupPython] Ce_element002  label="Ce_element : 1"  # scripted group (container) (typed FeaturePython)
  n = 1
  ref = Ce_element
FEATURE [App::DocumentObjectGroupPython] G4_Ce  # scripted group (container) (typed FeaturePython)
  Dunit = g/cm3
  Dvalue = 6.657
  Group = -> [Ce_element002]
  conduct = 2
  density = 1
  expand = 3
  formula = Ce
  name = G4_Ce
  specific = 4
FEATURE [App::DocumentObjectGroupPython] Pr_element001  label="Pr_element : 1"  # scripted group (container) (typed FeaturePython)
  n = 1
  ref = Pr_element
FEATURE [App::DocumentObjectGroupPython] G4_Pr  # scripted group (container) (typed FeaturePython)
  Dunit = g/cm3
  Dvalue = 6.71
  Group = -> [Pr_element001]
  conduct = 2
  density = 1
  expand = 3
  formula = Pr
  name = G4_Pr
  specific = 4
FEATURE [App::DocumentObjectGroupPython] Nd_element001  label="Nd_element : 1"  # scripted group (container) (typed FeaturePython)
  n = 1
  ref = Nd_element
FEATURE [App::DocumentObjectGroupPython] G4_Nd  # scripted group (container) (typed FeaturePython)
  Dunit = g/cm3
  Dvalue = 6.9
  Group = -> [Nd_element001]
  conduct = 2
  density = 1
  expand = 3
  formula = Nd
  name = G4_Nd
  specific = 4
FEATURE [App::DocumentObjectGroupPython] Pm_element001  label="Pm_element : 1"  # scripted group (container) (typed FeaturePython)
  n = 1
  ref = Pm_element
FEATURE [App::DocumentObjectGroupPython] G4_Pm  # scripted group (container) (typed FeaturePython)
  Dunit = g/cm3
  Dvalue = 7.22
  Group = -> [Pm_element001]
  conduct = 2
  density = 1
  expand = 3
  formula = Pm
  name = G4_Pm
  specific = 4
FEATURE [App::DocumentObjectGroupPython] Sm_element001  label="Sm_element : 1"  # scripted group (container) (typed FeaturePython)
  n = 1
  ref = Sm_element
FEATURE [App::DocumentObjectGroupPython] G4_Sm  # scripted group (container) (typed FeaturePython)
  Dunit = g/cm3
  Dvalue = 7.46
  Group = -> [Sm_element001]
  conduct = 2
  density = 1
  expand = 3
  formula = Sm
  name = G4_Sm
  specific = 4
FEATURE [App::DocumentObjectGroupPython] Eu_element001  label="Eu_element : 1"  # scripted group (container) (typed FeaturePython)
  n = 1
  ref = Eu_element
FEATURE [App::DocumentObjectGroupPython] G4_Eu  # scripted group (container) (typed FeaturePython)
  Dunit = g/cm3
  Dvalue = 5.243
  Group = -> [Eu_element001]
  conduct = 2
  density = 1
  expand = 3
  formula = Eu
  name = G4_Eu
  specific = 4
FEATURE [App::DocumentObjectGroupPython] Gd_element002  label="Gd_element : 1"  # scripted group (container) (typed FeaturePython)
  n = 1
  ref = Gd_element
FEATURE [App::DocumentObjectGroupPython] G4_Gd  # scripted group (container) (typed FeaturePython)
  Dunit = g/cm3
  Dvalue = 7.9004
  Group = -> [Gd_element002]
  conduct = 2
  density = 1
  expand = 3
  formula = Gd
  name = G4_Gd
  specific = 4
FEATURE [App::DocumentObjectGroupPython] Tb_element001  label="Tb_element : 1"  # scripted group (container) (typed FeaturePython)
  n = 1
  ref = Tb_element
FEATURE [App::DocumentObjectGroupPython] G4_Tb  # scripted group (container) (typed FeaturePython)
  Dunit = g/cm3
  Dvalue = 8.229
  Group = -> [Tb_element001]
  conduct = 2
  density = 1
  expand = 3
  formula = Tb
  name = G4_Tb
  specific = 4
FEATURE [App::DocumentObjectGroupPython] Dy_element001  label="Dy_element : 1"  # scripted group (container) (typed FeaturePython)
  n = 1
  ref = Dy_element
FEATURE [App::DocumentObjectGroupPython] G4_Dy  # scripted group (container) (typed FeaturePython)
  Dunit = g/cm3
  Dvalue = 8.55
  Group = -> [Dy_element001]
  conduct = 2
  density = 1
  expand = 3
  formula = Dy
  name = G4_Dy
  specific = 4
FEATURE [App::DocumentObjectGroupPython] Ho_element001  label="Ho_element : 1"  # scripted group (container) (typed FeaturePython)
  n = 1
  ref = Ho_element
FEATURE [App::DocumentObjectGroupPython] G4_Ho  # scripted group (container) (typed FeaturePython)
  Dunit = g/cm3
  Dvalue = 8.795
  Group = -> [Ho_element001]
  conduct = 2
  density = 1
  expand = 3
  formula = Ho
  name = G4_Ho
  specific = 4
FEATURE [App::DocumentObjectGroupPython] Er_element001  label="Er_element : 1"  # scripted group (container) (typed FeaturePython)
  n = 1
  ref = Er_element
FEATURE [App::DocumentObjectGroupPython] G4_Er  # scripted group (container) (typed FeaturePython)
  Dunit = g/cm3
  Dvalue = 9.066
  Group = -> [Er_element001]
  conduct = 2
  density = 1
  expand = 3
  formula = Er
  name = G4_Er
  specific = 4
FEATURE [App::DocumentObjectGroupPython] Tm_element001  label="Tm_element : 1"  # scripted group (container) (typed FeaturePython)
  n = 1
  ref = Tm_element
FEATURE [App::DocumentObjectGroupPython] G4_Tm  # scripted group (container) (typed FeaturePython)
  Dunit = g/cm3
  Dvalue = 9.321
  Group = -> [Tm_element001]
  conduct = 2
  density = 1
  expand = 3
  formula = Tm
  name = G4_Tm
  specific = 4
FEATURE [App::DocumentObjectGroupPython] Yb_element001  label="Yb_element : 1"  # scripted group (container) (typed FeaturePython)
  n = 1
  ref = Yb_element
FEATURE [App::DocumentObjectGroupPython] G4_Yb  # scripted group (container) (typed FeaturePython)
  Dunit = g/cm3
  Dvalue = 6.73
  Group = -> [Yb_element001]
  conduct = 2
  density = 1
  expand = 3
  formula = Yb
  name = G4_Yb
  specific = 4
FEATURE [App::DocumentObjectGroupPython] Lu_element001  label="Lu_element : 1"  # scripted group (container) (typed FeaturePython)
  n = 1
  ref = Lu_element
FEATURE [App::DocumentObjectGroupPython] G4_Lu  # scripted group (container) (typed FeaturePython)
  Dunit = g/cm3
  Dvalue = 9.84
  Group = -> [Lu_element001]
  conduct = 2
  density = 1
  expand = 3
  formula = Lu
  name = G4_Lu
  specific = 4
FEATURE [App::DocumentObjectGroupPython] Hf_element001  label="Hf_element : 1"  # scripted group (container) (typed FeaturePython)
  n = 1
  ref = Hf_element
FEATURE [App::DocumentObjectGroupPython] G4_Hf  # scripted group (container) (typed FeaturePython)
  Dunit = g/cm3
  Dvalue = 13.31
  Group = -> [Hf_element001]
  conduct = 2
  density = 1
  expand = 3
  formula = Hf
  name = G4_Hf
  specific = 4
FEATURE [App::DocumentObjectGroupPython] Ta_element001  label="Ta_element : 1"  # scripted group (container) (typed FeaturePython)
  n = 1
  ref = Ta_element
FEATURE [App::DocumentObjectGroupPython] G4_Ta  # scripted group (container) (typed FeaturePython)
  Dunit = g/cm3
  Dvalue = 16.654
  Group = -> [Ta_element001]
  conduct = 2
  density = 1
  expand = 3
  formula = Ta
  name = G4_Ta
  specific = 4
FEATURE [App::DocumentObjectGroupPython] W_element004  label="W_element : 004"  # scripted group (container) (typed FeaturePython)
  n = 1
  ref = W_element
FEATURE [App::DocumentObjectGroupPython] G4_W  # scripted group (container) (typed FeaturePython)
  Dunit = g/cm3
  Dvalue = 19.3
  Group = -> [W_element004]
  conduct = 2
  density = 1
  expand = 3
  formula = W
  name = G4_W
  specific = 4
FEATURE [App::DocumentObjectGroupPython] Re_element001  label="Re_element : 1"  # scripted group (container) (typed FeaturePython)
  n = 1
  ref = Re_element
FEATURE [App::DocumentObjectGroupPython] G4_Re  # scripted group (container) (typed FeaturePython)
  Dunit = g/cm3
  Dvalue = 21.02
  Group = -> [Re_element001]
  conduct = 2
  density = 1
  expand = 3
  formula = Re
  name = G4_Re
  specific = 4
FEATURE [App::DocumentObjectGroupPython] Os_element001  label="Os_element : 1"  # scripted group (container) (typed FeaturePython)
  n = 1
  ref = Os_element
FEATURE [App::DocumentObjectGroupPython] G4_Os  # scripted group (container) (typed FeaturePython)
  Dunit = g/cm3
  Dvalue = 22.57
  Group = -> [Os_element001]
  conduct = 2
  density = 1
  expand = 3
  formula = Os
  name = G4_Os
  specific = 4
FEATURE [App::DocumentObjectGroupPython] Ir_element001  label="Ir_element : 1"  # scripted group (container) (typed FeaturePython)
  n = 1
  ref = Ir_element
FEATURE [App::DocumentObjectGroupPython] G4_Ir  # scripted group (container) (typed FeaturePython)
  Dunit = g/cm3
  Dvalue = 22.42
  Group = -> [Ir_element001]
  conduct = 2
  density = 1
  expand = 3
  formula = Ir
  name = G4_Ir
  specific = 4
FEATURE [App::DocumentObjectGroupPython] Pt_element001  label="Pt_element : 1"  # scripted group (container) (typed FeaturePython)
  n = 1
  ref = Pt_element
FEATURE [App::DocumentObjectGroupPython] G4_Pt  # scripted group (container) (typed FeaturePython)
  Dunit = g/cm3
  Dvalue = 21.45
  Group = -> [Pt_element001]
  conduct = 2
  density = 1
  expand = 3
  formula = Pt
  name = G4_Pt
  specific = 4
FEATURE [App::DocumentObjectGroupPython] Au_element001  label="Au_element : 1"  # scripted group (container) (typed FeaturePython)
  n = 1
  ref = Au_element
FEATURE [App::DocumentObjectGroupPython] G4_Au  # scripted group (container) (typed FeaturePython)
  Dunit = g/cm3
  Dvalue = 19.32
  Group = -> [Au_element001]
  conduct = 2
  density = 1
  expand = 3
  formula = Au
  name = G4_Au
  specific = 4
FEATURE [App::DocumentObjectGroupPython] Hg_element002  label="Hg_element : 002"  # scripted group (container) (typed FeaturePython)
  n = 1
  ref = Hg_element
FEATURE [App::DocumentObjectGroupPython] G4_Hg  # scripted group (container) (typed FeaturePython)
  Dunit = g/cm3
  Dvalue = 13.546
  Group = -> [Hg_element002]
  conduct = 2
  density = 1
  expand = 3
  formula = Hg
  name = G4_Hg
  specific = 4
FEATURE [App::DocumentObjectGroupPython] Tl_element002  label="Tl_element : 002"  # scripted group (container) (typed FeaturePython)
  n = 1
  ref = Tl_element
FEATURE [App::DocumentObjectGroupPython] G4_Tl  # scripted group (container) (typed FeaturePython)
  Dunit = g/cm3
  Dvalue = 11.72
  Group = -> [Tl_element002]
  conduct = 2
  density = 1
  expand = 3
  formula = Tl
  name = G4_Tl
  specific = 4
FEATURE [App::DocumentObjectGroupPython] Pb_element003  label="Pb_element : 1"  # scripted group (container) (typed FeaturePython)
  n = 1
  ref = Pb_element
FEATURE [App::DocumentObjectGroupPython] G4_Pb  # scripted group (container) (typed FeaturePython)
  Dunit = g/cm3
  Dvalue = 11.35
  Group = -> [Pb_element003]
  conduct = 2
  density = 1
  expand = 3
  formula = Pb
  name = G4_Pb
  specific = 4
FEATURE [App::DocumentObjectGroupPython] Bi_element002  label="Bi_element : 1"  # scripted group (container) (typed FeaturePython)
  n = 1
  ref = Bi_element
FEATURE [App::DocumentObjectGroupPython] G4_Bi  # scripted group (container) (typed FeaturePython)
  Dunit = g/cm3
  Dvalue = 9.747
  Group = -> [Bi_element002]
  conduct = 2
  density = 1
  expand = 3
  formula = Bi
  name = G4_Bi
  specific = 4
FEATURE [App::DocumentObjectGroupPython] Po_element001  label="Po_element : 1"  # scripted group (container) (typed FeaturePython)
  n = 1
  ref = Po_element
FEATURE [App::DocumentObjectGroupPython] G4_Po  # scripted group (container) (typed FeaturePython)
  Dunit = g/cm3
  Dvalue = 9.32
  Group = -> [Po_element001]
  conduct = 2
  density = 1
  expand = 3
  formula = Po
  name = G4_Po
  specific = 4
FEATURE [App::DocumentObjectGroupPython] At_element001  label="At_element : 1"  # scripted group (container) (typed FeaturePython)
  n = 1
  ref = At_element
FEATURE [App::DocumentObjectGroupPython] G4_At  # scripted group (container) (typed FeaturePython)
  Dunit = g/cm3
  Dvalue = 9.32
  Group = -> [At_element001]
  conduct = 2
  density = 1
  expand = 3
  formula = At
  name = G4_At
  specific = 4
FEATURE [App::DocumentObjectGroupPython] Rn_element001  label="Rn_element : 1"  # scripted group (container) (typed FeaturePython)
  n = 1
  ref = Rn_element
FEATURE [App::DocumentObjectGroupPython] G4_Rn  # scripted group (container) (typed FeaturePython)
  Dunit = g/cm3
  Dvalue = 0.00900662
  Group = -> [Rn_element001]
  conduct = 2
  density = 1
  expand = 3
  formula = Rn
  name = G4_Rn
  specific = 4
FEATURE [App::DocumentObjectGroupPython] Fr_element001  label="Fr_element : 1"  # scripted group (container) (typed FeaturePython)
  n = 1
  ref = Fr_element
FEATURE [App::DocumentObjectGroupPython] G4_Fr  # scripted group (container) (typed FeaturePython)
  Dunit = g/cm3
  Dvalue = 1
  Group = -> [Fr_element001]
  conduct = 2
  density = 1
  expand = 3
  formula = Fr
  name = G4_Fr
  specific = 4
FEATURE [App::DocumentObjectGroupPython] Ra_element001  label="Ra_element : 1"  # scripted group (container) (typed FeaturePython)
  n = 1
  ref = Ra_element
FEATURE [App::DocumentObjectGroupPython] G4_Ra  # scripted group (container) (typed FeaturePython)
  Dunit = g/cm3
  Dvalue = 5
  Group = -> [Ra_element001]
  conduct = 2
  density = 1
  expand = 3
  formula = Ra
  name = G4_Ra
  specific = 4
FEATURE [App::DocumentObjectGroupPython] Ac_element001  label="Ac_element : 1"  # scripted group (container) (typed FeaturePython)
  n = 1
  ref = Ac_element
FEATURE [App::DocumentObjectGroupPython] G4_Ac  # scripted group (container) (typed FeaturePython)
  Dunit = g/cm3
  Dvalue = 10.07
  Group = -> [Ac_element001]
  conduct = 2
  density = 1
  expand = 3
  formula = Ac
  name = G4_Ac
  specific = 4
FEATURE [App::DocumentObjectGroupPython] Th_element001  label="Th_element : 1"  # scripted group (container) (typed FeaturePython)
  n = 1
  ref = Th_element
FEATURE [App::DocumentObjectGroupPython] G4_Th  # scripted group (container) (typed FeaturePython)
  Dunit = g/cm3
  Dvalue = 11.72
  Group = -> [Th_element001]
  conduct = 2
  density = 1
  expand = 3
  formula = Th
  name = G4_Th
  specific = 4
FEATURE [App::DocumentObjectGroupPython] Pa_element001  label="Pa_element : 1"  # scripted group (container) (typed FeaturePython)
  n = 1
  ref = Pa_element
FEATURE [App::DocumentObjectGroupPython] G4_Pa  # scripted group (container) (typed FeaturePython)
  Dunit = g/cm3
  Dvalue = 15.37
  Group = -> [Pa_element001]
  conduct = 2
  density = 1
  expand = 3
  formula = Pa
  name = G4_Pa
  specific = 4
FEATURE [App::DocumentObjectGroupPython] U_element004  label="U_element : 004"  # scripted group (container) (typed FeaturePython)
  n = 1
  ref = U_element
FEATURE [App::DocumentObjectGroupPython] G4_U  # scripted group (container) (typed FeaturePython)
  Dunit = g/cm3
  Dvalue = 18.95
  Group = -> [U_element004]
  conduct = 2
  density = 1
  expand = 3
  formula = U
  name = G4_U
  specific = 4
FEATURE [App::DocumentObjectGroupPython] Np_element001  label="Np_element : 1"  # scripted group (container) (typed FeaturePython)
  n = 1
  ref = Np_element
FEATURE [App::DocumentObjectGroupPython] G4_Np  # scripted group (container) (typed FeaturePython)
  Dunit = g/cm3
  Dvalue = 20.25
  Group = -> [Np_element001]
  conduct = 2
  density = 1
  expand = 3
  formula = Np
  name = G4_Np
  specific = 4
FEATURE [App::DocumentObjectGroupPython] Pu_element002  label="Pu_element : 002"  # scripted group (container) (typed FeaturePython)
  n = 1
  ref = Pu_element
FEATURE [App::DocumentObjectGroupPython] G4_Pu  # scripted group (container) (typed FeaturePython)
  Dunit = g/cm3
  Dvalue = 19.84
  Group = -> [Pu_element002]
  conduct = 2
  density = 1
  expand = 3
  formula = Pu
  name = G4_Pu
  specific = 4
FEATURE [App::DocumentObjectGroupPython] Am_element001  label="Am_element : 1"  # scripted group (container) (typed FeaturePython)
  n = 1
  ref = Am_element
FEATURE [App::DocumentObjectGroupPython] G4_Am  # scripted group (container) (typed FeaturePython)
  Dunit = g/cm3
  Dvalue = 13.67
  Group = -> [Am_element001]
  conduct = 2
  density = 1
  expand = 3
  formula = Am
  name = G4_Am
  specific = 4
FEATURE [App::DocumentObjectGroupPython] Cm_element001  label="Cm_element : 1"  # scripted group (container) (typed FeaturePython)
  n = 1
  ref = Cm_element
FEATURE [App::DocumentObjectGroupPython] G4_Cm  # scripted group (container) (typed FeaturePython)
  Dunit = g/cm3
  Dvalue = 13.51
  Group = -> [Cm_element001]
  conduct = 2
  density = 1
  expand = 3
  formula = Cm
  name = G4_Cm
  specific = 4
FEATURE [App::DocumentObjectGroupPython] Bk_element001  label="Bk_element : 1"  # scripted group (container) (typed FeaturePython)
  n = 1
  ref = Bk_element
FEATURE [App::DocumentObjectGroupPython] G4_Bk  # scripted group (container) (typed FeaturePython)
  Dunit = g/cm3
  Dvalue = 14
  Group = -> [Bk_element001]
  conduct = 2
  density = 1
  expand = 3
  formula = Bk
  name = G4_Bk
  specific = 4
FEATURE [App::DocumentObjectGroupPython] Cf_element001  label="Cf_element : 1"  # scripted group (container) (typed FeaturePython)
  n = 1
  ref = Cf_element
FEATURE [App::DocumentObjectGroupPython] G4_Cf  # scripted group (container) (typed FeaturePython)
  Dunit = g/cm3
  Dvalue = 10
  Group = -> [Cf_element001]
  conduct = 2
  density = 1
  expand = 3
  formula = Cf
  name = G4_Cf
  specific = 4
FEATURE [App::DocumentObjectGroupPython] Element  # scripted group (container) (typed FeaturePython)
  Group = -> [G4_H,G4_He,G4_Li,G4_Be,G4_B,G4_C,G4_N,G4_O,G4_F,G4_Ne,G4_Na,G4_Mg,G4_Al,G4_Si,G4_P,G4_S,G4_Cl,G4_Ar,G4_K,G4_Ca,G4_Sc,G4_Ti,G4_V,G4_Cr,G4_Mn,G4_Fe,G4_Co,G4_Ni,G4_Cu,G4_Zn,G4_Ga,G4_Ge,G4_As,G4_Se,G4_Br,G4_Kr,G4_Rb,G4_Sr,G4_Y,G4_Zr,G4_Nb,G4_Mo,G4_Tc,G4_Ru,G4_Rh,G4_Pd,G4_Ag,G4_Cd,G4_In,G4_Sn,G4_Sb,G4_Te,G4_I,G4_Xe,G4_Cs,G4_Ba,G4_La,G4_Ce,G4_Pr,G4_Nd,G4_Pm,G4_Sm,G4_Eu,G4_Gd,G4_Tb,G4_Dy,G4_Ho,G4_Er,+30 more]
FEATURE [App::DocumentObjectGroupPython] H_element114  label="H_element : 063"  # scripted group (container) (typed FeaturePython)
  n = 2
  ref = H_element
FEATURE [App::DocumentObjectGroupPython] G4_lH2  # scripted group (container) (typed FeaturePython)
  Dunit = g/cm3
  Dvalue = 0.0708
  Group = -> [H_element114]
  conduct = 2
  density = 1
  expand = 3
  formula = G4_lH2
  name = G4_lH2
  specific = 4
FEATURE [App::DocumentObjectGroupPython] N_element049  label="N_element : 022"  # scripted group (container) (typed FeaturePython)
  n = 2
  ref = N_element
FEATURE [App::DocumentObjectGroupPython] G4_lN2  # scripted group (container) (typed FeaturePython)
  Dunit = g/cm3
  Dvalue = 0.807
  Group = -> [N_element049]
  conduct = 2
  density = 1
  expand = 3
  formula = G4_lN2
  name = G4_lN2
  specific = 4
FEATURE [App::DocumentObjectGroupPython] O_element106  label="O_element : 060"  # scripted group (container) (typed FeaturePython)
  n = 2
  ref = O_element
FEATURE [App::DocumentObjectGroupPython] G4_lO2  # scripted group (container) (typed FeaturePython)
  Dunit = g/cm3
  Dvalue = 1.141
  Group = -> [O_element106]
  conduct = 2
  density = 1
  expand = 3
  formula = G4_lO2
  name = G4_lO2
  specific = 4
FEATURE [App::DocumentObjectGroupPython] Ar_element003  label="Ar_element : 002"  # scripted group (container) (typed FeaturePython)
  n = 1
  ref = Ar_element
FEATURE [App::DocumentObjectGroupPython] G4_lAr  # scripted group (container) (typed FeaturePython)
  Dunit = g/cm3
  Dvalue = 1.396
  Group = -> [Ar_element003]
  conduct = 2
  density = 1
  expand = 3
  formula = G4_lAr
  name = G4_lAr
  specific = 4
FEATURE [App::DocumentObjectGroupPython] Br_element008  label="Br_element : 005"  # scripted group (container) (typed FeaturePython)
  n = 1
  ref = Br_element
FEATURE [App::DocumentObjectGroupPython] G4_lBr  # scripted group (container) (typed FeaturePython)
  Dunit = g/cm3
  Dvalue = 3.1028
  Group = -> [Br_element008]
  conduct = 2
  density = 1
  expand = 3
  formula = G4_lBr
  name = G4_lBr
  specific = 4
FEATURE [App::DocumentObjectGroupPython] Kr_element002  label="Kr_element : 002"  # scripted group (container) (typed FeaturePython)
  n = 1
  ref = Kr_element
FEATURE [App::DocumentObjectGroupPython] G4_lKr  # scripted group (container) (typed FeaturePython)
  Dunit = g/cm3
  Dvalue = 2.418
  Group = -> [Kr_element002]
  conduct = 2
  density = 1
  expand = 3
  formula = G4_lKr
  name = G4_lKr
  specific = 4
FEATURE [App::DocumentObjectGroupPython] Xe_element002  label="Xe_element : 002"  # scripted group (container) (typed FeaturePython)
  n = 1
  ref = Xe_element
FEATURE [App::DocumentObjectGroupPython] G4_lXe  # scripted group (container) (typed FeaturePython)
  Dunit = g/cm3
  Dvalue = 2.953
  Group = -> [Xe_element002]
  conduct = 2
  density = 1
  expand = 3
  formula = G4_lXe
  name = G4_lXe
  specific = 4
FEATURE [App::DocumentObjectGroupPython] O_element107  label="O_element : 061"  # scripted group (container) (typed FeaturePython)
  n = 4
  ref = O_element
FEATURE [App::DocumentObjectGroupPython] Pb_element004  label="Pb_element : 002"  # scripted group (container) (typed FeaturePython)
  n = 1
  ref = Pb_element
FEATURE [App::DocumentObjectGroupPython] W_element005  label="W_element : 005"  # scripted group (container) (typed FeaturePython)
  n = 1
  ref = W_element
FEATURE [App::DocumentObjectGroupPython] G4_PbWO4  # scripted group (container) (typed FeaturePython)
  Dunit = g/cm3
  Dvalue = 8.28
  Group = -> [O_element107,Pb_element004,W_element005]
  conduct = 2
  density = 1
  expand = 3
  formula = G4_PbWO4
  name = G4_PbWO4
  specific = 4
FEATURE [App::DocumentObjectGroupPython] H_element115  label="H_element : 064"  # scripted group (container) (typed FeaturePython)
  n = 1
  ref = H_element
FEATURE [App::DocumentObjectGroupPython] G4_Galactic  # scripted group (container) (typed FeaturePython)
  Dunit = g/cm3
  Dvalue = 0
  Group = -> [H_element115]
  conduct = 2
  density = 1
  expand = 3
  formula = G4_Galactic
  name = G4_Galactic
  specific = 4
FEATURE [App::DocumentObjectGroupPython] C_element125  label="C_element : 071"  # scripted group (container) (typed FeaturePython)
  n = 1
  ref = C_element
FEATURE [App::DocumentObjectGroupPython] G4_GRAPHITE_POROUS  # scripted group (container) (typed FeaturePython)
  Dunit = g/cm3
  Dvalue = 1.7
  Group = -> [C_element125]
  conduct = 2
  density = 1
  expand = 3
  formula = G4_GRAPHITE_POROUS
  name = G4_GRAPHITE_POROUS
  specific = 4
FEATURE [App::DocumentObjectGroupPython] H_element116  label="H_element : 0.150"  # scripted group (container) (typed FeaturePython)
  n = 0.080538
FEATURE [App::DocumentObjectGroupPython] C_element126  label="C_element : 0.600"  # scripted group (container) (typed FeaturePython)
  n = 0.599848
FEATURE [App::DocumentObjectGroupPython] O_element108  label="O_element : 0.320"  # scripted group (container) (typed FeaturePython)
  n = 0.319614
FEATURE [App::DocumentObjectGroupPython] G4_LUCITE  # scripted group (container) (typed FeaturePython)
  Dunit = g/cm3
  Dvalue = 1.19
  Group = -> [H_element116,C_element126,O_element108]
  conduct = 2
  density = 1
  expand = 3
  formula = G4_LUCITE
  name = G4_LUCITE
  specific = 4
FEATURE [App::DocumentObjectGroupPython] Cu_element002  label="Cu_element : 62"  # scripted group (container) (typed FeaturePython)
  n = 62
  ref = Cu_element
FEATURE [App::DocumentObjectGroupPython] Zn_element002  label="Zn_element : 35"  # scripted group (container) (typed FeaturePython)
  n = 35
  ref = Zn_element
FEATURE [App::DocumentObjectGroupPython] Pb_element005  label="Pb_element : 3"  # scripted group (container) (typed FeaturePython)
  n = 3
  ref = Pb_element
FEATURE [App::DocumentObjectGroupPython] G4_BRASS  # scripted group (container) (typed FeaturePython)
  Dunit = g/cm3
  Dvalue = 8.52
  Group = -> [Cu_element002,Zn_element002,Pb_element005]
  conduct = 2
  density = 1
  expand = 3
  formula = G4_BRASS
  name = G4_BRASS
  specific = 4
FEATURE [App::DocumentObjectGroupPython] Cu_element003  label="Cu_element : 89"  # scripted group (container) (typed FeaturePython)
  n = 89
  ref = Cu_element
FEATURE [App::DocumentObjectGroupPython] Zn_element003  label="Zn_element : 9"  # scripted group (container) (typed FeaturePython)
  n = 9
  ref = Zn_element
FEATURE [App::DocumentObjectGroupPython] Pb_element006  label="Pb_element : 2"  # scripted group (container) (typed FeaturePython)
  n = 2
  ref = Pb_element
FEATURE [App::DocumentObjectGroupPython] G4_BRONZE  # scripted group (container) (typed FeaturePython)
  Dunit = g/cm3
  Dvalue = 8.82
  Group = -> [Cu_element003,Zn_element003,Pb_element006]
  conduct = 2
  density = 1
  expand = 3
  formula = G4_BRONZE
  name = G4_BRONZE
  specific = 4
FEATURE [App::DocumentObjectGroupPython] Fe_element008  label="Fe_element : 74"  # scripted group (container) (typed FeaturePython)
  n = 74
  ref = Fe_element
FEATURE [App::DocumentObjectGroupPython] Cr_element002  label="Cr_element : 18"  # scripted group (container) (typed FeaturePython)
  n = 18
  ref = Cr_element
FEATURE [App::DocumentObjectGroupPython] Ni_element002  label="Ni_element : 8"  # scripted group (container) (typed FeaturePython)
  n = 8
  ref = Ni_element
FEATURE [App::DocumentObjectGroupPython] G4_STAINLESS_STEEL  label="G4_STAINLESS-STEEL"  # scripted group (container) (typed FeaturePython)
  Dunit = g/cm3
  Dvalue = 8
  Group = -> [Fe_element008,Cr_element002,Ni_element002]
  conduct = 2
  density = 1
  expand = 3
  formula = G4_STAINLESS-STEEL
  name = G4_STAINLESS-STEEL
  specific = 4
FEATURE [App::DocumentObjectGroupPython] H_element117  label="H_element : 065"  # scripted group (container) (typed FeaturePython)
  n = 18
  ref = H_element
FEATURE [App::DocumentObjectGroupPython] C_element127  label="C_element : 072"  # scripted group (container) (typed FeaturePython)
  n = 12
  ref = C_element
FEATURE [App::DocumentObjectGroupPython] O_element109  label="O_element : 062"  # scripted group (container) (typed FeaturePython)
  n = 7
  ref = O_element
FEATURE [App::DocumentObjectGroupPython] G4_CR39  # scripted group (container) (typed FeaturePython)
  Dunit = g/cm3
  Dvalue = 1.32
  Group = -> [H_element117,C_element127,O_element109]
  conduct = 2
  density = 1
  expand = 3
  formula = G4_CR39
  name = G4_CR39
  specific = 4
FEATURE [App::DocumentObjectGroupPython] H_element118  label="H_element : 38"  # scripted group (container) (typed FeaturePython)
  n = 38
  ref = H_element
FEATURE [App::DocumentObjectGroupPython] C_element128  label="C_element : 073"  # scripted group (container) (typed FeaturePython)
  n = 18
  ref = C_element
FEATURE [App::DocumentObjectGroupPython] O_element110  label="O_element : 063"  # scripted group (container) (typed FeaturePython)
  n = 1
  ref = O_element
FEATURE [App::DocumentObjectGroupPython] G4_OCTADECANOL  # scripted group (container) (typed FeaturePython)
  Dunit = g/cm3
  Dvalue = 0.812
  Group = -> [H_element118,C_element128,O_element110]
  conduct = 2
  density = 1
  expand = 3
  formula = G4_OCTADECANOL
  name = G4_OCTADECANOL
  specific = 4
FEATURE [App::DocumentObjectGroupPython] HEP  # scripted group (container) (typed FeaturePython)
  Group = -> [G4_lH2,G4_lN2,G4_lO2,G4_lAr,G4_lBr,G4_lKr,G4_lXe,G4_PbWO4,G4_Galactic,G4_GRAPHITE_POROUS,G4_LUCITE,G4_BRASS,G4_BRONZE,G4_STAINLESS_STEEL,G4_CR39,G4_OCTADECANOL]
FEATURE [App::DocumentObjectGroupPython] C_element129  label="C_element : 074"  # scripted group (container) (typed FeaturePython)
  n = 14
  ref = C_element
FEATURE [App::DocumentObjectGroupPython] H_element119  label="H_element : 066"  # scripted group (container) (typed FeaturePython)
  n = 10
  ref = H_element
FEATURE [App::DocumentObjectGroupPython] O_element111  label="O_element : 064"  # scripted group (container) (typed FeaturePython)
  n = 2
  ref = O_element
FEATURE [App::DocumentObjectGroupPython] N_element050  label="N_element : 023"  # scripted group (container) (typed FeaturePython)
  n = 2
  ref = N_element
FEATURE [App::DocumentObjectGroupPython] G4_KEVLAR  # scripted group (container) (typed FeaturePython)
  Dunit = g/cm3
  Dvalue = 1.44
  Group = -> [C_element129,H_element119,O_element111,N_element050]
  conduct = 2
  density = 1
  expand = 3
  formula = G4_KEVLAR
  name = G4_KEVLAR
  specific = 4
FEATURE [App::DocumentObjectGroupPython] C_element130  label="C_element : 075"  # scripted group (container) (typed FeaturePython)
  n = 10
  ref = C_element
FEATURE [App::DocumentObjectGroupPython] H_element120  label="H_element : 067"  # scripted group (container) (typed FeaturePython)
  n = 8
  ref = H_element
FEATURE [App::DocumentObjectGroupPython] O_element112  label="O_element : 065"  # scripted group (container) (typed FeaturePython)
  n = 4
  ref = O_element
FEATURE [App::DocumentObjectGroupPython] G4_DACRON  # scripted group (container) (typed FeaturePython)
  Dunit = g/cm3
  Dvalue = 1.4
  Group = -> [C_element130,H_element120,O_element112]
  conduct = 2
  density = 1
  expand = 3
  formula = G4_DACRON
  name = G4_DACRON
  specific = 4
FEATURE [App::DocumentObjectGroupPython] C_element131  label="C_element : 076"  # scripted group (container) (typed FeaturePython)
  n = 4
  ref = C_element
FEATURE [App::DocumentObjectGroupPython] H_element121  label="H_element : 068"  # scripted group (container) (typed FeaturePython)
  n = 5
  ref = H_element
FEATURE [App::DocumentObjectGroupPython] Cl_element030  label="Cl_element : 016"  # scripted group (container) (typed FeaturePython)
  n = 1
  ref = Cl_element
FEATURE [App::DocumentObjectGroupPython] G4_NEOPRENE  # scripted group (container) (typed FeaturePython)
  Dunit = g/cm3
  Dvalue = 1.23
  Group = -> [C_element131,H_element121,Cl_element030]
  conduct = 2
  density = 1
  expand = 3
  formula = G4_NEOPRENE
  name = G4_NEOPRENE
  specific = 4
FEATURE [App::DocumentObjectGroupPython] Space  # scripted group (container) (typed FeaturePython)
  Group = -> [G4_KEVLAR,G4_DACRON,G4_NEOPRENE]
FEATURE [App::DocumentObjectGroupPython] H_element122  label="H_element : 069"  # scripted group (container) (typed FeaturePython)
  n = 5
  ref = H_element
FEATURE [App::DocumentObjectGroupPython] C_element132  label="C_element : 077"  # scripted group (container) (typed FeaturePython)
  n = 4
  ref = C_element
FEATURE [App::DocumentObjectGroupPython] N_element051  label="N_element : 3"  # scripted group (container) (typed FeaturePython)
  n = 3
  ref = N_element
FEATURE [App::DocumentObjectGroupPython] O_element113  label="O_element : 066"  # scripted group (container) (typed FeaturePython)
  n = 1
  ref = O_element
FEATURE [App::DocumentObjectGroupPython] G4_CYTOSINE  # scripted group (container) (typed FeaturePython)
  Dunit = g/cm3
  Dvalue = 1.55
  Group = -> [H_element122,C_element132,N_element051,O_element113]
  conduct = 2
  density = 1
  expand = 3
  formula = G4_CYTOSINE
  name = G4_CYTOSINE
  specific = 4
FEATURE [App::DocumentObjectGroupPython] H_element123  label="H_element : 070"  # scripted group (container) (typed FeaturePython)
  n = 6
  ref = H_element
FEATURE [App::DocumentObjectGroupPython] C_element133  label="C_element : 078"  # scripted group (container) (typed FeaturePython)
  n = 5
  ref = C_element
FEATURE [App::DocumentObjectGroupPython] N_element052  label="N_element : 024"  # scripted group (container) (typed FeaturePython)
  n = 2
  ref = N_element
FEATURE [App::DocumentObjectGroupPython] O_element114  label="O_element : 067"  # scripted group (container) (typed FeaturePython)
  n = 2
  ref = O_element
FEATURE [App::DocumentObjectGroupPython] G4_THYMINE  # scripted group (container) (typed FeaturePython)
  Dunit = g/cm3
  Dvalue = 1.23
  Group = -> [H_element123,C_element133,N_element052,O_element114]
  conduct = 2
  density = 1
  expand = 3
  formula = G4_THYMINE
  name = G4_THYMINE
  specific = 4
FEATURE [App::DocumentObjectGroupPython] H_element124  label="H_element : 071"  # scripted group (container) (typed FeaturePython)
  n = 4
  ref = H_element
FEATURE [App::DocumentObjectGroupPython] C_element134  label="C_element : 079"  # scripted group (container) (typed FeaturePython)
  n = 4
  ref = C_element
FEATURE [App::DocumentObjectGroupPython] N_element053  label="N_element : 025"  # scripted group (container) (typed FeaturePython)
  n = 2
  ref = N_element
FEATURE [App::DocumentObjectGroupPython] O_element115  label="O_element : 068"  # scripted group (container) (typed FeaturePython)
  n = 2
  ref = O_element
FEATURE [App::DocumentObjectGroupPython] G4_URACIL  # scripted group (container) (typed FeaturePython)
  Dunit = g/cm3
  Dvalue = 1.32
  Group = -> [H_element124,C_element134,N_element053,O_element115]
  conduct = 2
  density = 1
  expand = 3
  formula = G4_URACIL
  name = G4_URACIL
  specific = 4
FEATURE [App::DocumentObjectGroupPython] H_element125  label="H_element : 072"  # scripted group (container) (typed FeaturePython)
  n = 4
  ref = H_element
FEATURE [App::DocumentObjectGroupPython] C_element135  label="C_element : 080"  # scripted group (container) (typed FeaturePython)
  n = 5
  ref = C_element
FEATURE [App::DocumentObjectGroupPython] N_element054  label="N_element : 026"  # scripted group (container) (typed FeaturePython)
  n = 5
  ref = N_element
FEATURE [App::DocumentObjectGroupPython] G4_DNA_ADENINE  # scripted group (container) (typed FeaturePython)
  Dunit = g/cm3
  Dvalue = 1
  Group = -> [H_element125,C_element135,N_element054]
  conduct = 2
  density = 1
  expand = 3
  formula = G4_DNA_ADENINE
  name = G4_DNA_ADENINE
  specific = 4
FEATURE [App::DocumentObjectGroupPython] H_element126  label="H_element : 073"  # scripted group (container) (typed FeaturePython)
  n = 4
  ref = H_element
FEATURE [App::DocumentObjectGroupPython] C_element136  label="C_element : 081"  # scripted group (container) (typed FeaturePython)
  n = 5
  ref = C_element
FEATURE [App::DocumentObjectGroupPython] N_element055  label="N_element : 027"  # scripted group (container) (typed FeaturePython)
  n = 5
  ref = N_element
FEATURE [App::DocumentObjectGroupPython] O_element116  label="O_element : 069"  # scripted group (container) (typed FeaturePython)
  n = 1
  ref = O_element
FEATURE [App::DocumentObjectGroupPython] G4_DNA_GUANINE  # scripted group (container) (typed FeaturePython)
  Dunit = g/cm3
  Dvalue = 1
  Group = -> [H_element126,C_element136,N_element055,O_element116]
  conduct = 2
  density = 1
  expand = 3
  formula = G4_DNA_GUANINE
  name = G4_DNA_GUANINE
  specific = 4
FEATURE [App::DocumentObjectGroupPython] H_element127  label="H_element : 074"  # scripted group (container) (typed FeaturePython)
  n = 4
  ref = H_element
FEATURE [App::DocumentObjectGroupPython] C_element137  label="C_element : 082"  # scripted group (container) (typed FeaturePython)
  n = 4
  ref = C_element
FEATURE [App::DocumentObjectGroupPython] N_element056  label="N_element : 028"  # scripted group (container) (typed FeaturePython)
  n = 3
  ref = N_element
FEATURE [App::DocumentObjectGroupPython] O_element117  label="O_element : 070"  # scripted group (container) (typed FeaturePython)
  n = 1
  ref = O_element
FEATURE [App::DocumentObjectGroupPython] G4_DNA_CYTOSINE  # scripted group (container) (typed FeaturePython)
  Dunit = g/cm3
  Dvalue = 1
  Group = -> [H_element127,C_element137,N_element056,O_element117]
  conduct = 2
  density = 1
  expand = 3
  formula = G4_DNA_CYTOSINE
  name = G4_DNA_CYTOSINE
  specific = 4
FEATURE [App::DocumentObjectGroupPython] H_element128  label="H_element : 075"  # scripted group (container) (typed FeaturePython)
  n = 5
  ref = H_element
FEATURE [App::DocumentObjectGroupPython] C_element138  label="C_element : 083"  # scripted group (container) (typed FeaturePython)
  n = 5
  ref = C_element
FEATURE [App::DocumentObjectGroupPython] N_element057  label="N_element : 029"  # scripted group (container) (typed FeaturePython)
  n = 2
  ref = N_element
FEATURE [App::DocumentObjectGroupPython] O_element118  label="O_element : 071"  # scripted group (container) (typed FeaturePython)
  n = 2
  ref = O_element
FEATURE [App::DocumentObjectGroupPython] G4_DNA_THYMINE  # scripted group (container) (typed FeaturePython)
  Dunit = g/cm3
  Dvalue = 1
  Group = -> [H_element128,C_element138,N_element057,O_element118]
  conduct = 2
  density = 1
  expand = 3
  formula = G4_DNA_THYMINE
  name = G4_DNA_THYMINE
  specific = 4
FEATURE [App::DocumentObjectGroupPython] H_element129  label="H_element : 076"  # scripted group (container) (typed FeaturePython)
  n = 3
  ref = H_element
FEATURE [App::DocumentObjectGroupPython] C_element139  label="C_element : 084"  # scripted group (container) (typed FeaturePython)
  n = 4
  ref = C_element
FEATURE [App::DocumentObjectGroupPython] N_element058  label="N_element : 030"  # scripted group (container) (typed FeaturePython)
  n = 2
  ref = N_element
FEATURE [App::DocumentObjectGroupPython] O_element119  label="O_element : 072"  # scripted group (container) (typed FeaturePython)
  n = 2
  ref = O_element
FEATURE [App::DocumentObjectGroupPython] G4_DNA_URACIL  # scripted group (container) (typed FeaturePython)
  Dunit = g/cm3
  Dvalue = 1
  Group = -> [H_element129,C_element139,N_element058,O_element119]
  conduct = 2
  density = 1
  expand = 3
  formula = G4_DNA_URACIL
  name = G4_DNA_URACIL
  specific = 4
FEATURE [App::DocumentObjectGroupPython] H_element130  label="H_element : 077"  # scripted group (container) (typed FeaturePython)
  n = 10
  ref = H_element
FEATURE [App::DocumentObjectGroupPython] C_element140  label="C_element : 085"  # scripted group (container) (typed FeaturePython)
  n = 10
  ref = C_element
FEATURE [App::DocumentObjectGroupPython] N_element059  label="N_element : 031"  # scripted group (container) (typed FeaturePython)
  n = 5
  ref = N_element
FEATURE [App::DocumentObjectGroupPython] O_element120  label="O_element : 073"  # scripted group (container) (typed FeaturePython)
  n = 4
  ref = O_element
FEATURE [App::DocumentObjectGroupPython] G4_DNA_ADENOSINE  # scripted group (container) (typed FeaturePython)
  Dunit = g/cm3
  Dvalue = 1
  Group = -> [H_element130,C_element140,N_element059,O_element120]
  conduct = 2
  density = 1
  expand = 3
  formula = G4_DNA_ADENOSINE
  name = G4_DNA_ADENOSINE
  specific = 4
FEATURE [App::DocumentObjectGroupPython] H_element131  label="H_element : 078"  # scripted group (container) (typed FeaturePython)
  n = 10
  ref = H_element
FEATURE [App::DocumentObjectGroupPython] C_element141  label="C_element : 086"  # scripted group (container) (typed FeaturePython)
  n = 10
  ref = C_element
FEATURE [App::DocumentObjectGroupPython] N_element060  label="N_element : 032"  # scripted group (container) (typed FeaturePython)
  n = 5
  ref = N_element
FEATURE [App::DocumentObjectGroupPython] O_element121  label="O_element : 074"  # scripted group (container) (typed FeaturePython)
  n = 5
  ref = O_element
FEATURE [App::DocumentObjectGroupPython] G4_DNA_GUANOSINE  # scripted group (container) (typed FeaturePython)
  Dunit = g/cm3
  Dvalue = 1
  Group = -> [H_element131,C_element141,N_element060,O_element121]
  conduct = 2
  density = 1
  expand = 3
  formula = G4_DNA_GUANOSINE
  name = G4_DNA_GUANOSINE
  specific = 4
FEATURE [App::DocumentObjectGroupPython] H_element132  label="H_element : 079"  # scripted group (container) (typed FeaturePython)
  n = 10
  ref = H_element
FEATURE [App::DocumentObjectGroupPython] C_element142  label="C_element : 087"  # scripted group (container) (typed FeaturePython)
  n = 9
  ref = C_element
FEATURE [App::DocumentObjectGroupPython] N_element061  label="N_element : 033"  # scripted group (container) (typed FeaturePython)
  n = 3
  ref = N_element
FEATURE [App::DocumentObjectGroupPython] O_element122  label="O_element : 075"  # scripted group (container) (typed FeaturePython)
  n = 5
  ref = O_element
FEATURE [App::DocumentObjectGroupPython] G4_DNA_CYTIDINE  # scripted group (container) (typed FeaturePython)
  Dunit = g/cm3
  Dvalue = 1
  Group = -> [H_element132,C_element142,N_element061,O_element122]
  conduct = 2
  density = 1
  expand = 3
  formula = G4_DNA_CYTIDINE
  name = G4_DNA_CYTIDINE
  specific = 4
FEATURE [App::DocumentObjectGroupPython] H_element133  label="H_element : 080"  # scripted group (container) (typed FeaturePython)
  n = 9
  ref = H_element
FEATURE [App::DocumentObjectGroupPython] C_element143  label="C_element : 088"  # scripted group (container) (typed FeaturePython)
  n = 9
  ref = C_element
FEATURE [App::DocumentObjectGroupPython] N_element062  label="N_element : 034"  # scripted group (container) (typed FeaturePython)
  n = 2
  ref = N_element
FEATURE [App::DocumentObjectGroupPython] O_element123  label="O_element : 076"  # scripted group (container) (typed FeaturePython)
  n = 6
  ref = O_element
FEATURE [App::DocumentObjectGroupPython] G4_DNA_URIDINE  # scripted group (container) (typed FeaturePython)
  Dunit = g/cm3
  Dvalue = 1
  Group = -> [H_element133,C_element143,N_element062,O_element123]
  conduct = 2
  density = 1
  expand = 3
  formula = G4_DNA_URIDINE
  name = G4_DNA_URIDINE
  specific = 4
FEATURE [App::DocumentObjectGroupPython] H_element134  label="H_element : 081"  # scripted group (container) (typed FeaturePython)
  n = 11
  ref = H_element
FEATURE [App::DocumentObjectGroupPython] C_element144  label="C_element : 089"  # scripted group (container) (typed FeaturePython)
  n = 10
  ref = C_element
FEATURE [App::DocumentObjectGroupPython] N_element063  label="N_element : 035"  # scripted group (container) (typed FeaturePython)
  n = 2
  ref = N_element
FEATURE [App::DocumentObjectGroupPython] O_element124  label="O_element : 077"  # scripted group (container) (typed FeaturePython)
  n = 6
  ref = O_element
FEATURE [App::DocumentObjectGroupPython] G4_DNA_METHYLURIDINE  # scripted group (container) (typed FeaturePython)
  Dunit = g/cm3
  Dvalue = 1
  Group = -> [H_element134,C_element144,N_element063,O_element124]
  conduct = 2
  density = 1
  expand = 3
  formula = G4_DNA_METHYLURIDINE
  name = G4_DNA_METHYLURIDINE
  specific = 4
FEATURE [App::DocumentObjectGroupPython] P_element014  label="P_element : 003"  # scripted group (container) (typed FeaturePython)
  n = 1
  ref = P_element
FEATURE [App::DocumentObjectGroupPython] O_element125  label="O_element : 078"  # scripted group (container) (typed FeaturePython)
  n = 3
  ref = O_element
FEATURE [App::DocumentObjectGroupPython] G4_DNA_MONOPHOSPHATE  # scripted group (container) (typed FeaturePython)
  Dunit = g/cm3
  Dvalue = 1
  Group = -> [P_element014,O_element125]
  conduct = 2
  density = 1
  expand = 3
  formula = G4_DNA_MONOPHOSPHATE
  name = G4_DNA_MONOPHOSPHATE
  specific = 4
FEATURE [App::DocumentObjectGroupPython] H_element135  label="H_element : 082"  # scripted group (container) (typed FeaturePython)
  n = 10
  ref = H_element
FEATURE [App::DocumentObjectGroupPython] C_element145  label="C_element : 090"  # scripted group (container) (typed FeaturePython)
  n = 10
  ref = C_element
FEATURE [App::DocumentObjectGroupPython] N_element064  label="N_element : 036"  # scripted group (container) (typed FeaturePython)
  n = 5
  ref = N_element
FEATURE [App::DocumentObjectGroupPython] O_element126  label="O_element : 079"  # scripted group (container) (typed FeaturePython)
  n = 7
  ref = O_element
FEATURE [App::DocumentObjectGroupPython] P_element015  label="P_element : 004"  # scripted group (container) (typed FeaturePython)
  n = 1
  ref = P_element
FEATURE [App::DocumentObjectGroupPython] G4_DNA_A  # scripted group (container) (typed FeaturePython)
  Dunit = g/cm3
  Dvalue = 1
  Group = -> [H_element135,C_element145,N_element064,O_element126,P_element015]
  conduct = 2
  density = 1
  expand = 3
  formula = G4_DNA_A
  name = G4_DNA_A
  specific = 4
FEATURE [App::DocumentObjectGroupPython] H_element136  label="H_element : 083"  # scripted group (container) (typed FeaturePython)
  n = 10
  ref = H_element
FEATURE [App::DocumentObjectGroupPython] C_element146  label="C_element : 091"  # scripted group (container) (typed FeaturePython)
  n = 10
  ref = C_element
FEATURE [App::DocumentObjectGroupPython] N_element065  label="N_element : 037"  # scripted group (container) (typed FeaturePython)
  n = 5
  ref = N_element
FEATURE [App::DocumentObjectGroupPython] O_element127  label="O_element : 8"  # scripted group (container) (typed FeaturePython)
  n = 8
  ref = O_element
FEATURE [App::DocumentObjectGroupPython] P_element016  label="P_element : 005"  # scripted group (container) (typed FeaturePython)
  n = 1
  ref = P_element
FEATURE [App::DocumentObjectGroupPython] G4_DNA_G  # scripted group (container) (typed FeaturePython)
  Dunit = g/cm3
  Dvalue = 1
  Group = -> [H_element136,C_element146,N_element065,O_element127,P_element016]
  conduct = 2
  density = 1
  expand = 3
  formula = G4_DNA_G
  name = G4_DNA_G
  specific = 4
FEATURE [App::DocumentObjectGroupPython] H_element137  label="H_element : 084"  # scripted group (container) (typed FeaturePython)
  n = 10
  ref = H_element
FEATURE [App::DocumentObjectGroupPython] C_element147  label="C_element : 092"  # scripted group (container) (typed FeaturePython)
  n = 9
  ref = C_element
FEATURE [App::DocumentObjectGroupPython] N_element066  label="N_element : 038"  # scripted group (container) (typed FeaturePython)
  n = 3
  ref = N_element
FEATURE [App::DocumentObjectGroupPython] O_element128  label="O_element : 080"  # scripted group (container) (typed FeaturePython)
  n = 8
  ref = O_element
FEATURE [App::DocumentObjectGroupPython] P_element017  label="P_element : 006"  # scripted group (container) (typed FeaturePython)
  n = 1
  ref = P_element
FEATURE [App::DocumentObjectGroupPython] G4_DNA_C  # scripted group (container) (typed FeaturePython)
  Dunit = g/cm3
  Dvalue = 1
  Group = -> [H_element137,C_element147,N_element066,O_element128,P_element017]
  conduct = 2
  density = 1
  expand = 3
  formula = G4_DNA_C
  name = G4_DNA_C
  specific = 4
FEATURE [App::DocumentObjectGroupPython] H_element138  label="H_element : 085"  # scripted group (container) (typed FeaturePython)
  n = 9
  ref = H_element
FEATURE [App::DocumentObjectGroupPython] C_element148  label="C_element : 093"  # scripted group (container) (typed FeaturePython)
  n = 9
  ref = C_element
FEATURE [App::DocumentObjectGroupPython] N_element067  label="N_element : 039"  # scripted group (container) (typed FeaturePython)
  n = 2
  ref = N_element
FEATURE [App::DocumentObjectGroupPython] O_element129  label="O_element : 9"  # scripted group (container) (typed FeaturePython)
  n = 9
  ref = O_element
FEATURE [App::DocumentObjectGroupPython] P_element018  label="P_element : 007"  # scripted group (container) (typed FeaturePython)
  n = 1
  ref = P_element
FEATURE [App::DocumentObjectGroupPython] G4_DNA_U  # scripted group (container) (typed FeaturePython)
  Dunit = g/cm3
  Dvalue = 1
  Group = -> [H_element138,C_element148,N_element067,O_element129,P_element018]
  conduct = 2
  density = 1
  expand = 3
  formula = G4_DNA_U
  name = G4_DNA_U
  specific = 4
FEATURE [App::DocumentObjectGroupPython] H_element139  label="H_element : 086"  # scripted group (container) (typed FeaturePython)
  n = 11
  ref = H_element
FEATURE [App::DocumentObjectGroupPython] C_element149  label="C_element : 094"  # scripted group (container) (typed FeaturePython)
  n = 10
  ref = C_element
FEATURE [App::DocumentObjectGroupPython] N_element068  label="N_element : 040"  # scripted group (container) (typed FeaturePython)
  n = 2
  ref = N_element
FEATURE [App::DocumentObjectGroupPython] O_element130  label="O_element : 081"  # scripted group (container) (typed FeaturePython)
  n = 9
  ref = O_element
FEATURE [App::DocumentObjectGroupPython] P_element019  label="P_element : 008"  # scripted group (container) (typed FeaturePython)
  n = 1
  ref = P_element
FEATURE [App::DocumentObjectGroupPython] G4_DNA_MU  # scripted group (container) (typed FeaturePython)
  Dunit = g/cm3
  Dvalue = 1
  Group = -> [H_element139,C_element149,N_element068,O_element130,P_element019]
  conduct = 2
  density = 1
  expand = 3
  formula = G4_DNA_MU
  name = G4_DNA_MU
  specific = 4
FEATURE [App::DocumentObjectGroupPython] BioChemical  # scripted group (container) (typed FeaturePython)
  Group = -> [G4_CYTOSINE,G4_THYMINE,G4_URACIL,G4_DNA_ADENINE,G4_DNA_GUANINE,G4_DNA_CYTOSINE,G4_DNA_THYMINE,G4_DNA_URACIL,G4_DNA_ADENOSINE,G4_DNA_GUANOSINE,G4_DNA_CYTIDINE,G4_DNA_URIDINE,G4_DNA_METHYLURIDINE,G4_DNA_MONOPHOSPHATE,G4_DNA_A,G4_DNA_G,G4_DNA_C,G4_DNA_U,G4_DNA_MU]
FEATURE [App::DocumentObjectGroupPython] G4Materials  # scripted group (container) (typed FeaturePython)
  Group = -> [NIST,Element,HEP,Space,BioChemical]
  version = 1
FEATURE [App::DocumentObjectGroupPython] Geant4  # scripted group (container) (typed FeaturePython)
  Group = -> [G4Isotopes,G4Elements,G4Materials]
FEATURE [App::DocumentObjectGroupPython] Materials  # scripted group (container) (typed FeaturePython)
  Group = -> [Geant4]
FEATURE [Part::FeaturePython] GDMLBox_WorldBox  # WARN: FeaturePython — macro-defined, semantics opaque (R4)
  lunit = 2
  material = 5
  x = 100
  y = 100
  z = 100
FEATURE [Part::FeaturePython] GDMLBox_Box  # WARN: FeaturePython — macro-defined, semantics opaque (R4)
  Placement = pos=(0,0,-5) rot=(0,0,1;0.523599rad)
  lunit = 2
  material = 0
  x = 10
  y = 10
  z = 10
FEATURE [Part::FeaturePython] GDMLTube  # WARN: FeaturePython — macro-defined, semantics opaque (R4)
  Placement = pos=(0,0,5) rot=(0,1,0;-0.523599rad)
  aunit = 1
  deltaphi = 360
  lunit = 2
  material = 0
  rmax = 3
  rmin = 0
  startphi = 0
  z = 20
FEATURE [Part::Fuse] Fuse
  Base = -> GDMLBox_Box
  Placement = pos=(-1.1021,1.1021,0.645598) rot=(0.678598,0.281085,0.678598;1.09606rad)
  Tool = -> GDMLTube
FEATURE [App::Part] Bool_Fuse
  Group = -> [GDMLBox_Box,GDMLTube,Fuse]
  Origin = -> Origin003
  Placement = pos=(20,0,6) rot=(1,0,0;1.5708rad)
FEATURE [App::Part] worldVOL
  Group = -> [GDMLBox_WorldBox,Bool_Fuse]
  Origin = -> Origin
